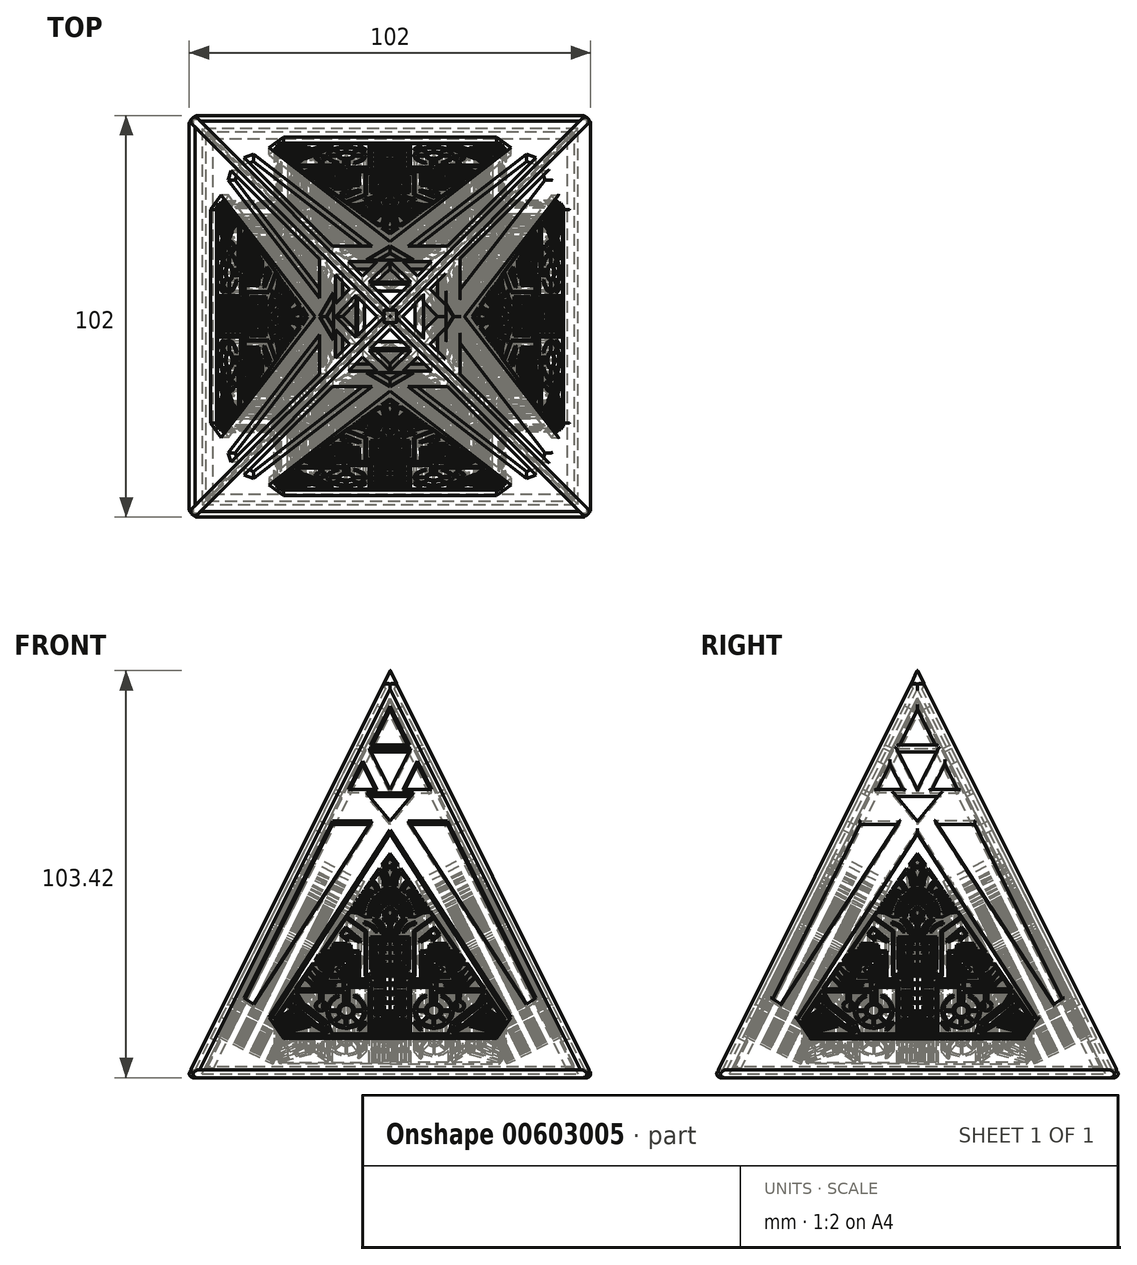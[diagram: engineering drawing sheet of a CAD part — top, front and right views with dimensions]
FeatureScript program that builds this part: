
annotation { "Feature Type Name" : "Feature", "Feature Type Description" : "" }
export const myFeature = defineFeature(function(context is Context, id is Id, definition is map)
    precondition{}
    {
        {
            var Q0;
            Q0=qCreatedBy(makeId("Front.planeOp"),FACE);
            var sketch = newSketch(context, id + "F0", { "sketchPlane" : qUnion([Q0])});
            skLineSegment(sketch, "E0", {"start": v(-50, 0) * mm, "end": v(50, 0) * mm});
            skLineSegment(sketch, "E1", {"start": v(50, 0) * mm, "end": v(0, 100) * mm});
            skLineSegment(sketch, "E2", {"start": v(0, 100) * mm, "end": v(-50, 0) * mm});
            skLineSegment(sketch, "E3", {"start": v(0, 0) * mm, "end": v(0, 112.42) * mm, "construction": true});
            skSolve(sketch);
        }
        {
            var Q0;
            Q0=qCreatedBy(makeId("Right.planeOp"),FACE);
            cPlane(context, id + "F1", {"entities" : qUnion([Q0]), "cplaneType" : CPlaneType.OFFSET, "offset" : 50 * mm, "width" : 150 * mm, "height" : 150 * mm});
        }
        {
            var Q0;
            Q0=qCreatedBy(id+"F1.planeOp",FACE);
            var Q1;
            Q1=sQuery(id+"F0.wireOp",EDGE,"E1");
            cPlane(context, id + "F2", {"entities" : qUnion([Q0, Q1]), "cplaneType" : CPlaneType.LINE_ANGLE, "offset" : 25 * mm, "angle" : 0 * degree, "width" : 150 * mm, "height" : 150 * mm});
        }
        {
            var Q0;
            Q0=qCreatedBy(id+"F2.planeOp",FACE);
            var sketch = newSketch(context, id + "F3", { "sketchPlane" : qUnion([Q0])});
            skPoint(sketch, "E4.0", {"position": v(0, -22.36) * mm});
            skPoint(sketch, "E5.0", {"position": v(0, 89.44) * mm});
            skLineSegment(sketch, "E6", {"start": v(50, -22.36) * mm, "end": v(-50, -22.36) * mm});
            skLineSegment(sketch, "E7", {"start": v(-50, -22.36) * mm, "end": v(0, 89.44) * mm});
            skLineSegment(sketch, "E8", {"start": v(50, -22.36) * mm, "end": v(0, 89.44) * mm});
            skLineSegment(sketch, "E9", {"start": v(35.98, 49.44) * mm, "end": v(-47.97, 49.44) * mm, "construction": true});
            skLineSegment(sketch, "E10", {"start": v(46.71, -22.36) * mm, "end": v(-5.35, 94.05) * mm, "construction": true});
            skLineSegment(sketch, "E11", {"start": v(89.5, -12.36) * mm, "end": v(-110.17, -12.36) * mm, "construction": true});
            skLineSegment(sketch, "E12", {"start": v(0, 89.44) * mm, "end": v(0, 132.78) * mm, "construction": true});
            skLineSegment(sketch, "E13", {"start": v(-1.46, 49.44) * mm, "end": v(40, -22.36) * mm, "construction": true});
            skCircle(sketch, "E14", {"center": v(50, -22.36) * mm, "radius": 25 * mm, "construction": true});
            skLineSegment(sketch, "E15.MirrorCS", {"start": v(-46.71, -22.36) * mm, "end": v(5.35, 94.05) * mm, "construction": true});
            skLineSegment(sketch, "E16.MirrorCS", {"start": v(1.46, 49.44) * mm, "end": v(-40, -22.36) * mm, "construction": true});
            skLineSegment(sketch, "E17", {"start": v(-14.6, 49.44) * mm, "end": v(-4.6, 49.44) * mm});
            skCircle(sketch, "E18.MirrorC", {"center": v(-50, -22.36) * mm, "radius": 25 * mm, "construction": true});
            skLineSegment(sketch, "E19", {"start": v(-4.6, 49.44) * mm, "end": v(-34.66, -2.62) * mm});
            skLineSegment(sketch, "E20", {"start": v(-34.66, -2.62) * mm, "end": v(-37.05, -0.76) * mm});
            skLineSegment(sketch, "E21", {"start": v(-37.05, -0.76) * mm, "end": v(-14.6, 49.44) * mm});
            skLineSegment(sketch, "E22.MirrorCS", {"start": v(4.6, 49.44) * mm, "end": v(34.66, -2.62) * mm});
            skLineSegment(sketch, "E23.MirrorCS", {"start": v(37.05, -0.76) * mm, "end": v(14.6, 49.44) * mm});
            skLineSegment(sketch, "E24.MirrorCS", {"start": v(34.66, -2.62) * mm, "end": v(37.05, -0.76) * mm});
            skLineSegment(sketch, "E25.MirrorCS", {"start": v(14.6, 49.44) * mm, "end": v(4.6, 49.44) * mm});
            skLineSegment(sketch, "E26", {"start": v(0, 46.92) * mm, "end": v(30.77, -6.38) * mm});
            skLineSegment(sketch, "E27", {"start": v(-27.09, -12.36) * mm, "end": v(-30.77, -6.38) * mm});
            skLineSegment(sketch, "E28", {"start": v(-30.77, -6.38) * mm, "end": v(0, 46.92) * mm});
            skLineSegment(sketch, "E29", {"start": v(30.77, -6.38) * mm, "end": v(27.09, -12.36) * mm});
            skLineSegment(sketch, "E30", {"start": v(27.09, -12.36) * mm, "end": v(-27.09, -12.36) * mm});
            skLineSegment(sketch, "E31", {"start": v(23.46, 57.44) * mm, "end": v(-27.6, 57.44) * mm, "construction": true});
            skLineSegment(sketch, "E32", {"start": v(6, 57.44) * mm, "end": v(0, 49.44) * mm});
            skLineSegment(sketch, "E33", {"start": v(0, 49.44) * mm, "end": v(-6, 57.44) * mm});
            skLineSegment(sketch, "E34", {"start": v(-6, 57.44) * mm, "end": v(6, 57.44) * mm});
            skLineSegment(sketch, "E35", {"start": v(12.53, 58.44) * mm, "end": v(-20.65, 58.44) * mm, "construction": true});
            skLineSegment(sketch, "E36", {"start": v(0, 82.1) * mm, "end": v(4.92, 71.1) * mm});
            skLineSegment(sketch, "E37", {"start": v(4.92, 71.1) * mm, "end": v(-4.92, 71.1) * mm});
            skLineSegment(sketch, "E38", {"start": v(-4.92, 71.1) * mm, "end": v(0, 82.1) * mm});
            skLineSegment(sketch, "E39", {"start": v(14.36, 70.1) * mm, "end": v(-15.5, 70.1) * mm, "construction": true});
            skLineSegment(sketch, "E40", {"start": v(5.37, 70.1) * mm, "end": v(0, 58.44) * mm});
            skLineSegment(sketch, "E41", {"start": v(0, 58.44) * mm, "end": v(-5.37, 70.1) * mm});
            skLineSegment(sketch, "E42", {"start": v(-5.37, 70.1) * mm, "end": v(5.37, 70.1) * mm});
            skLineSegment(sketch, "E43", {"start": v(10.58, 58.44) * mm, "end": v(7, 66.46) * mm});
            skLineSegment(sketch, "E44", {"start": v(7, 66.46) * mm, "end": v(3.3, 58.44) * mm});
            skLineSegment(sketch, "E45", {"start": v(3.3, 58.44) * mm, "end": v(10.58, 58.44) * mm});
            skLineSegment(sketch, "E46.MirrorCS", {"start": v(-7, 66.46) * mm, "end": v(-3.3, 58.44) * mm});
            skLineSegment(sketch, "E47.MirrorCS", {"start": v(-3.3, 58.44) * mm, "end": v(-10.58, 58.44) * mm});
            skLineSegment(sketch, "E48.MirrorCS", {"start": v(-10.58, 58.44) * mm, "end": v(-7, 66.46) * mm});
            skSolve(sketch);
        }
        {
            var Q0;
            Q0=makeQuery(id+"F3.imprint","IMPRINT",FACE,{"disambiguationData":[TD([[makeQuery(id+"F3.imprint","IMPRINT",EDGE,{"derivedFrom":sQuery(id+"F3.wireOp",EDGE,"E6")}),-1.0]])]});
            extrude(context, id + "F4", {"entities" : qUnion([Q0]), "depth" : 2 * mm, "offsetDistance" : 25 * mm});
        }
        {
            var Q0;
            Q0=makeQuery(id+"F4.opExtrude","SWEPT_BODY",BODY,{"disambiguationData":[OSD([sQuery(id+"F3.wireOp",EDGE,"E6"),sQuery(id+"F3.wireOp",EDGE,"E7"),sQuery(id+"F3.wireOp",EDGE,"E8")])]});
            var Q1;
            Q1=sQuery(id+"F0.wireOp",EDGE,"E3");
            circularPattern(context, id + "F5", {"entities" : qUnion([Q0]), "axis" : qUnion([Q1]), "angle" : 360 * degree, "instanceCount" : 4, "equalSpace" : true});
        }
        {
            var Q0;
            Q0=qCreatedBy(makeId("Right.planeOp"),FACE);
            var sketch = newSketch(context, id + "F6", { "sketchPlane" : qUnion([Q0])});
            skPoint(sketch, "E49.0", {"position": v(0, 100) * mm});
            skLineSegment(sketch, "E50.0", {"start": v(50, 0) * mm, "end": v(0, 100) * mm, "construction": true});
            skLineSegment(sketch, "E51", {"start": v(0, 100) * mm, "end": v(3.76, 100) * mm});
            skLineSegment(sketch, "E52", {"start": v(3.76, 100) * mm, "end": v(2.28, 95.44) * mm});
            skLineSegment(sketch, "E53", {"start": v(2.28, 95.44) * mm, "end": v(0, 100) * mm});
            skLineSegment(sketch, "E54", {"start": v(0, 100) * mm, "end": v(0, 104.73) * mm, "construction": true});
            skLineSegment(sketch, "E55.MirrorCS", {"start": v(0, 100) * mm, "end": v(-3.76, 100) * mm});
            skLineSegment(sketch, "E56.MirrorCS", {"start": v(-3.76, 100) * mm, "end": v(-2.28, 95.44) * mm});
            skLineSegment(sketch, "E57.MirrorCS", {"start": v(-2.28, 95.44) * mm, "end": v(0, 100) * mm});
            skSolve(sketch);
        }
        {
            var Q0;
            Q0 = qSketchRegion(id + "F6", true);
            extrude(context, id + "F7", {"entities" : qUnion([Q0]), "operationType" : NewBodyOperationType.REMOVE, "endBound" : BoundingType.SYMMETRIC, "oppositeDirection" : true, "depth" : 25 * mm, "offsetDistance" : 25 * mm});
        }
        {
            var Q0;
            Q0=qCreatedBy(makeId("Front.planeOp"),FACE);
            var sketch = newSketch(context, id + "F8", { "sketchPlane" : qUnion([Q0])});
            skPoint(sketch, "E58.0", {"position": v(0, 100) * mm});
            skLineSegment(sketch, "E59.0", {"start": v(50, 0) * mm, "end": v(0, 100) * mm, "construction": true});
            skLineSegment(sketch, "E60", {"start": v(0, 100) * mm, "end": v(1.68, 96.63) * mm});
            skLineSegment(sketch, "E61", {"start": v(1.68, 96.63) * mm, "end": v(3.16, 99.58) * mm});
            skLineSegment(sketch, "E62", {"start": v(3.16, 99.58) * mm, "end": v(0, 100) * mm});
            skLineSegment(sketch, "E63", {"start": v(0, 100) * mm, "end": v(0, 101.09) * mm, "construction": true});
            skLineSegment(sketch, "E64.MirrorCS", {"start": v(-3.16, 99.58) * mm, "end": v(0, 100) * mm});
            skLineSegment(sketch, "E65.MirrorCS", {"start": v(0, 100) * mm, "end": v(-1.68, 96.63) * mm});
            skLineSegment(sketch, "E66.MirrorCS", {"start": v(-1.68, 96.63) * mm, "end": v(-3.16, 99.58) * mm});
            skSolve(sketch);
        }
        {
            var Q0;
            Q0=makeQuery(id+"F8.imprint","IMPRINT",FACE,{"disambiguationData":[TD([[makeQuery(id+"F8.imprint","IMPRINT",EDGE,{"derivedFrom":sQuery(id+"F8.wireOp",EDGE,"E60")}),1.0]])]});
            var Q1;
            Q1=makeQuery(id+"F8.imprint","IMPRINT",FACE,{"disambiguationData":[TD([[makeQuery(id+"F8.imprint","IMPRINT",EDGE,{"derivedFrom":sQuery(id+"F8.wireOp",EDGE,"E64.MirrorCS")}),-1.0]])]});
            extrude(context, id + "F9", {"entities" : qUnion([Q0, Q1]), "operationType" : NewBodyOperationType.REMOVE, "endBound" : BoundingType.SYMMETRIC, "oppositeDirection" : true, "depth" : 25 * mm, "offsetDistance" : 25 * mm});
        }
        {
            var Q0;
            Q0=qCreatedBy(makeId("Top.planeOp"),FACE);
            var sketch = newSketch(context, id + "F10", { "sketchPlane" : qUnion([Q0])});
            skLineSegment(sketch, "E67.0", {"start": v(50, 50) * mm, "end": v(-50, 50) * mm});
            skLineSegment(sketch, "E68.0", {"start": v(50, -50) * mm, "end": v(50, 50) * mm});
            skLineSegment(sketch, "E69.0", {"start": v(-50, -50) * mm, "end": v(50, -50) * mm});
            skLineSegment(sketch, "E70.0", {"start": v(-50, 50) * mm, "end": v(-50, -50) * mm});
            skSolve(sketch);
        }
        {
            var Q0;
            Q0 = qSketchRegion(id + "F10", true);
            extrude(context, id + "F11", {"entities" : qUnion([Q0]), "operationType" : NewBodyOperationType.ADD, "oppositeDirection" : true, "depth" : 1 * mm, "offsetDistance" : 25 * mm});
        }
        {
            var Q0;
            Q0=qCreatedBy(id+"F2.planeOp",FACE);
            cPlane(context, id + "F12", {"entities" : qUnion([Q0]), "cplaneType" : CPlaneType.OFFSET, "offset" : 2 * mm, "width" : 150 * mm, "height" : 150 * mm});
        }
        {
            var Q0;
            Q0=qCreatedBy(id+"F12.planeOp",FACE);
            var sketch = newSketch(context, id + "F13", { "sketchPlane" : qUnion([Q0])});
            skLineSegment(sketch, "E71.0", {"start": v(50, -22.36) * mm, "end": v(0, 89.44) * mm, "construction": true});
            skLineSegment(sketch, "E72.0", {"start": v(-50, -22.36) * mm, "end": v(0, 89.44) * mm, "construction": true});
            skLineSegment(sketch, "E73.0", {"start": v(50, -22.36) * mm, "end": v(-50, -22.36) * mm, "construction": true});
            skLineSegment(sketch, "E74", {"start": v(46.47, -19.36) * mm, "end": v(-46.47, -19.36) * mm});
            skLineSegment(sketch, "E75", {"start": v(-46.47, -19.36) * mm, "end": v(0, 84.54) * mm});
            skLineSegment(sketch, "E76", {"start": v(0, 84.54) * mm, "end": v(46.47, -19.36) * mm});
            skSolve(sketch);
        }
        {
            var Q0;
            Q0 = qSketchRegion(id + "F13", true);
            extrude(context, id + "F14", {"entities" : qUnion([Q0]), "depth" : 2 * mm, "offsetDistance" : 25 * mm});
        }
        {
            var Q0;
            Q0=makeQuery(id+"F14.opExtrude","SWEPT_BODY",BODY,{"disambiguationData":[OSD([sQuery(id+"F13.wireOp",EDGE,"E74"),sQuery(id+"F13.wireOp",EDGE,"E75"),sQuery(id+"F13.wireOp",EDGE,"E76")])]});
            var Q1;
            Q1=sQuery(id+"F0.wireOp",EDGE,"E3");
            circularPattern(context, id + "F15", {"operationType" : NewBodyOperationType.ADD, "entities" : qUnion([Q0]), "axis" : qUnion([Q1]), "angle" : 360 * degree, "instanceCount" : 4, "equalSpace" : true});
        }
        {
            var Q0;
            Q0=qCreatedBy(id+"F2.planeOp",FACE);
            var sketch = newSketch(context, id + "F16", { "sketchPlane" : qUnion([Q0])});
            skLineSegment(sketch, "E77.0", {"start": v(-50, -22.36) * mm, "end": v(0, 89.44) * mm, "construction": true});
            skLineSegment(sketch, "E78", {"start": v(0.5, 88.12) * mm, "end": v(-48.68, -21.86) * mm});
            skArc(sketch, "E79", {"start": v(-50, -22.36) * mm, "mid": v(-49.23, -22.38) * mm, "end": v(-48.68, -21.86) * mm});
            skArc(sketch, "E80", {"start": v(0.5, 88.12) * mm, "mid": v(0.53, 88.89) * mm, "end": v(0, 89.44) * mm});
            skLineSegment(sketch, "E81", {"start": v(0, 89.44) * mm, "end": v(-50, -22.36) * mm});
            skSolve(sketch);
        }
        {
            var Q0;
            Q0 = qSketchRegion(id + "F16", true);
            var Q1;
            Q1=sQuery(id+"F16.wireOp",EDGE,"E81");
            revolve(context, id + "F17", {"entities" : qUnion([Q0]), "axis" : qUnion([Q1]), "revolveType" : RevolveType.FULL});
        }
        {
            var Q0;
            Q0=makeQuery(id+"F17.opRevolve","SWEPT_BODY",BODY,{"disambiguationData":[OSD([sQuery(id+"F16.wireOp",EDGE,"E78"),sQuery(id+"F16.wireOp",EDGE,"E79"),sQuery(id+"F16.wireOp",EDGE,"E80"),sQuery(id+"F16.wireOp",EDGE,"E81")])]});
            var Q1;
            Q1=sQuery(id+"F0.wireOp",EDGE,"E3");
            circularPattern(context, id + "F18", {"operationType" : NewBodyOperationType.ADD, "entities" : qUnion([Q0]), "axis" : qUnion([Q1]), "angle" : 360 * degree, "instanceCount" : 4, "equalSpace" : true});
        }
        {
            var Q0;
            Q0=qCreatedBy(id+"F2.planeOp",FACE);
            var sketch = newSketch(context, id + "F19", { "sketchPlane" : qUnion([Q0])});
            skLineSegment(sketch, "E82.0", {"start": v(50, -22.36) * mm, "end": v(-50, -22.36) * mm, "construction": true});
            skLineSegment(sketch, "E83", {"start": v(49, -21.36) * mm, "end": v(-49, -21.36) * mm});
            skArc(sketch, "E84", {"start": v(-49, -21.36) * mm, "mid": v(-49.7, -21.65) * mm, "end": v(-50, -22.36) * mm});
            skArc(sketch, "E85", {"start": v(50, -22.36) * mm, "mid": v(49.7, -21.65) * mm, "end": v(49, -21.36) * mm});
            skLineSegment(sketch, "E86", {"start": v(-50, -22.36) * mm, "end": v(50, -22.36) * mm});
            skSolve(sketch);
        }
        {
            var Q0;
            Q0 = qSketchRegion(id + "F19", true);
            var Q1;
            Q1=sQuery(id+"F19.wireOp",EDGE,"E86");
            revolve(context, id + "F20", {"entities" : qUnion([Q0]), "axis" : qUnion([Q1]), "revolveType" : RevolveType.FULL});
        }
        {
            var Q0;
            Q0=makeQuery(id+"F20.opRevolve","SWEPT_BODY",BODY,{"disambiguationData":[OSD([sQuery(id+"F19.wireOp",EDGE,"E83"),sQuery(id+"F19.wireOp",EDGE,"E84"),sQuery(id+"F19.wireOp",EDGE,"E85"),sQuery(id+"F19.wireOp",EDGE,"E86")])]});
            var Q1;
            Q1=sQuery(id+"F0.wireOp",EDGE,"E3");
            circularPattern(context, id + "F21", {"operationType" : NewBodyOperationType.ADD, "entities" : qUnion([Q0]), "axis" : qUnion([Q1]), "angle" : 360 * degree, "instanceCount" : 4, "equalSpace" : true});
        }
        {
            var Q0;
            Q0=qCreatedBy(makeId("Top.planeOp"),FACE);
            cPlane(context, id + "F22", {"entities" : qUnion([Q0]), "cplaneType" : CPlaneType.OFFSET, "offset" : 99 * mm, "width" : 150 * mm, "height" : 150 * mm});
        }
        {
            var Q0;
            Q0=qCreatedBy(id+"F22.planeOp",FACE);
            var sketch = newSketch(context, id + "F23", { "sketchPlane" : qUnion([Q0])});
            skLineSegment(sketch, "E87.bottom", {"start": v(-1.6, 1.66) * mm, "end": v(1.72, 1.66) * mm});
            skLineSegment(sketch, "E87.top", {"start": v(-1.6, -1.66) * mm, "end": v(1.72, -1.66) * mm});
            skLineSegment(sketch, "E87.left", {"start": v(-1.6, 1.66) * mm, "end": v(-1.6, -1.66) * mm});
            skLineSegment(sketch, "E87.right", {"start": v(1.72, 1.66) * mm, "end": v(1.72, -1.66) * mm});
            skSolve(sketch);
        }
        {
            var Q0;
            Q0=makeQuery(id+"F23.imprint","IMPRINT",FACE,{"disambiguationData":[TD([[makeQuery(id+"F23.imprint","IMPRINT",EDGE,{"derivedFrom":sQuery(id+"F23.wireOp",EDGE,"E87.bottom")}),-1.0]])]});
            extrude(context, id + "F24", {"entities" : qUnion([Q0]), "operationType" : NewBodyOperationType.ADD, "depth" : 25 * mm, "offsetDistance" : 25 * mm, "hasDraft" : true, "draftAngle" : 25 * degree, "draftPullDirection" : true});
        }
        {
            var Q0;
            Q0=makeQuery(id+"F24.opExtrude","SWEPT_EDGE",EDGE,{"disambiguationData":[OSD([sQuery(id+"F23.wireOp",EDGE,"E87.top"),sQuery(id+"F23.wireOp",EDGE,"E87.left")])]});
            var Q1;
            Q1=makeQuery(id+"F24.opExtrude","CAP_EDGE",EDGE,{"disambiguationData":[OSD([sQuery(id+"F23.wireOp",EDGE,"E87.top")])],"isStart":true});
            var Q2;
            Q2=makeQuery(id+"F24.opExtrude","SWEPT_EDGE",EDGE,{"disambiguationData":[OSD([sQuery(id+"F23.wireOp",EDGE,"E87.top"),sQuery(id+"F23.wireOp",EDGE,"E87.right")])]});
            var Q3;
            Q3=makeQuery(id+"F24.opExtrude","SWEPT_EDGE",EDGE,{"disambiguationData":[OSD([sQuery(id+"F23.wireOp",EDGE,"E87.bottom"),sQuery(id+"F23.wireOp",EDGE,"E87.right")])]});
            var Q4;
            Q4=makeQuery(id+"F24.opExtrude","CAP_EDGE",EDGE,{"disambiguationData":[OSD([sQuery(id+"F23.wireOp",EDGE,"E87.right")])],"isStart":true});
            var Q5;
            {var subQ0=sQuery(id+"F23.wireOp",EDGE,"E87.top");var subQ1=sQuery(id+"F23.wireOp",EDGE,"E87.left");Q5=makeQuery(id+"F24.boolean.opBoolean","SPLIT",EDGE,{"disambiguationData":[TD([makeQuery(id+"F18.opPattern","COPY",FACE,{"derivedFrom":makeQuery(id+"F17.opRevolve","SWEPT_FACE",FACE,{"disambiguationData":[OSD([sQuery(id+"F16.wireOp",EDGE,"E78")])]}),"instanceName":"2"}),makeQuery(id+"F24.opExtrude","CAP_FACE",FACE,{"disambiguationData":[OSD([sQuery(id+"F23.wireOp",EDGE,"E87.bottom"),subQ0,subQ1,sQuery(id+"F23.wireOp",EDGE,"E87.right")])],"isStart":true}),makeQuery(id+"F24.opExtrude","SWEPT_FACE",FACE,{"disambiguationData":[OSD([subQ0])]}),makeQuery(id+"F24.opExtrude","SWEPT_FACE",FACE,{"disambiguationData":[OSD([subQ1])]})])],"derivedFrom":makeQuery(id+"F24.opExtrude","CAP_EDGE",EDGE,{"disambiguationData":[OSD([subQ1])],"isStart":true})});}
            var Q6;
            {var subQ0=makeQuery(id+"F17.opRevolve","SWEPT_FACE",FACE,{"disambiguationData":[OSD([sQuery(id+"F16.wireOp",EDGE,"E78")])]});var subQ1=sQuery(id+"F23.wireOp",EDGE,"E87.left");Q6=makeQuery(id+"F24.boolean.opBoolean","SPLIT",EDGE,{"disambiguationData":[TD([makeQuery(id+"F18.opPattern","COPY",FACE,{"derivedFrom":subQ0,"instanceName":"1"}),makeQuery(id+"F18.opPattern","COPY",FACE,{"derivedFrom":subQ0,"instanceName":"2"}),makeQuery(id+"F24.opExtrude","CAP_FACE",FACE,{"disambiguationData":[OSD([sQuery(id+"F23.wireOp",EDGE,"E87.bottom"),sQuery(id+"F23.wireOp",EDGE,"E87.top"),subQ1,sQuery(id+"F23.wireOp",EDGE,"E87.right")])],"isStart":true}),makeQuery(id+"F24.opExtrude","SWEPT_FACE",FACE,{"disambiguationData":[OSD([subQ1])]})])],"derivedFrom":makeQuery(id+"F24.opExtrude","CAP_EDGE",EDGE,{"disambiguationData":[OSD([subQ1])],"isStart":true})});}
            var Q7;
            {var subQ0=sQuery(id+"F23.wireOp",EDGE,"E87.bottom");var subQ1=sQuery(id+"F23.wireOp",EDGE,"E87.left");Q7=makeQuery(id+"F24.boolean.opBoolean","SPLIT",EDGE,{"disambiguationData":[TD([makeQuery(id+"F18.opPattern","COPY",FACE,{"derivedFrom":makeQuery(id+"F17.opRevolve","SWEPT_FACE",FACE,{"disambiguationData":[OSD([sQuery(id+"F16.wireOp",EDGE,"E78")])]}),"instanceName":"1"}),makeQuery(id+"F24.opExtrude","SWEPT_FACE",FACE,{"disambiguationData":[OSD([subQ0])]}),makeQuery(id+"F24.opExtrude","CAP_FACE",FACE,{"disambiguationData":[OSD([subQ0,sQuery(id+"F23.wireOp",EDGE,"E87.top"),subQ1,sQuery(id+"F23.wireOp",EDGE,"E87.right")])],"isStart":true}),makeQuery(id+"F24.opExtrude","SWEPT_FACE",FACE,{"disambiguationData":[OSD([subQ1])]})])],"derivedFrom":makeQuery(id+"F24.opExtrude","CAP_EDGE",EDGE,{"disambiguationData":[OSD([subQ1])],"isStart":true})});}
            var Q8;
            Q8=makeQuery(id+"F24.opExtrude","SWEPT_EDGE",EDGE,{"disambiguationData":[OSD([sQuery(id+"F23.wireOp",EDGE,"E87.bottom"),sQuery(id+"F23.wireOp",EDGE,"E87.left")])]});
            var Q9;
            Q9=makeQuery(id+"F24.opExtrude","CAP_EDGE",EDGE,{"disambiguationData":[OSD([sQuery(id+"F23.wireOp",EDGE,"E87.bottom")])],"isStart":true});
            fillet(context, id + "F25", {"entities" : qUnion([Q0, Q1, Q2, Q3, Q4, Q5, Q6, Q7, Q8, Q9]), "radius" : .1 * mm, "tangentPropagation" : true, "allowEdgeOverflow" : false});
        }
        {
            var Q0;
            Q0=makeQuery(id+"F14.opExtrude","CAP_FACE",FACE,{"disambiguationData":[OSD([sQuery(id+"F13.wireOp",EDGE,"E74"),sQuery(id+"F13.wireOp",EDGE,"E75"),sQuery(id+"F13.wireOp",EDGE,"E76")])],"isStart":true});
            var sketch = newSketch(context, id + "F26", { "sketchPlane" : qUnion([Q0])});
            skLineSegment(sketch, "E88", {"start": v(0, 47.8) * mm, "end": v(0, -17.25) * mm, "construction": true});
            skLineSegment(sketch, "E89.0", {"start": v(30.77, -6.38) * mm, "end": v(0, 46.92) * mm, "construction": true});
            skLineSegment(sketch, "E90.0", {"start": v(27.09, -12.36) * mm, "end": v(30.77, -6.38) * mm, "construction": true});
            skLineSegment(sketch, "E91.0", {"start": v(-27.09, -12.36) * mm, "end": v(27.09, -12.36) * mm, "construction": true});
            skCircle(sketch, "E92", {"center": v(11.12, -3.94) * mm, "radius": 1.62 * mm});
            skArc(sketch, "E93", {"start": v(8.97, -4.1) * mm, "mid": v(9.14, -4.8) * mm, "end": v(9.54, -5.4) * mm});
            skArc(sketch, "E94", {"start": v(8.98, 0.55) * mm, "mid": v(11.12, -8.92) * mm, "end": v(13.26, 0.55) * mm});
            skArc(sketch, "E95", {"start": v(9.32, 0.06) * mm, "mid": v(7.5, -1.47) * mm, "end": v(6.74, -3.71) * mm});
            skLineSegment(sketch, "E96", {"start": v(8.98, 0.55) * mm, "end": v(9.32, 0.06) * mm});
            skLineSegment(sketch, "E97", {"start": v(12.93, 0.06) * mm, "end": v(13.26, 0.55) * mm});
            skLineSegment(sketch, "E98", {"start": v(6.74, -3.71) * mm, "end": v(8.98, -3.71) * mm});
            skLineSegment(sketch, "E99", {"start": v(6.73, -4.1) * mm, "end": v(8.97, -4.1) * mm});
            skLineSegment(sketch, "E100", {"start": v(13.26, -3.66) * mm, "end": v(15.5, -3.66) * mm});
            skLineSegment(sketch, "E101", {"start": v(13.27, -4.1) * mm, "end": v(15.5, -4.1) * mm});
            skLineSegment(sketch, "E102", {"start": v(9.54, -5.4) * mm, "end": v(8.04, -7.07) * mm});
            skLineSegment(sketch, "E103", {"start": v(9.82, -5.67) * mm, "end": v(8.33, -7.33) * mm});
            skLineSegment(sketch, "E104", {"start": v(10.94, -6.1) * mm, "end": v(10.94, -8.33) * mm});
            skLineSegment(sketch, "E105", {"start": v(11.36, -6.09) * mm, "end": v(11.36, -8.33) * mm});
            skLineSegment(sketch, "E106", {"start": v(12.43, -5.65) * mm, "end": v(13.98, -7.28) * mm});
            skLineSegment(sketch, "E107", {"start": v(12.77, -5.33) * mm, "end": v(14.35, -6.92) * mm});
            skArc(sketch, "E108.trimOffspring", {"start": v(6.73, -4.1) * mm, "mid": v(7.1, -5.71) * mm, "end": v(8.04, -7.07) * mm});
            skArc(sketch, "E109.trimOffspring", {"start": v(9.82, -5.67) * mm, "mid": v(10.35, -5.96) * mm, "end": v(10.94, -6.1) * mm});
            skArc(sketch, "E110.trimOffspring", {"start": v(8.33, -7.33) * mm, "mid": v(9.55, -8.04) * mm, "end": v(10.94, -8.33) * mm});
            skArc(sketch, "E111.trimOffspring", {"start": v(11.36, -8.33) * mm, "mid": v(12.76, -8.02) * mm, "end": v(13.98, -7.28) * mm});
            skArc(sketch, "E112.trimOffspring", {"start": v(11.36, -6.09) * mm, "mid": v(11.93, -5.94) * mm, "end": v(12.43, -5.65) * mm});
            skArc(sketch, "E113.trimOffspring", {"start": v(12.77, -5.33) * mm, "mid": v(13.12, -4.76) * mm, "end": v(13.27, -4.1) * mm});
            skArc(sketch, "E114.trimOffspring", {"start": v(14.35, -6.92) * mm, "mid": v(15.18, -5.61) * mm, "end": v(15.5, -4.1) * mm});
            skArc(sketch, "E115.trimOffspring", {"start": v(15.5, -3.66) * mm, "mid": v(14.73, -1.44) * mm, "end": v(12.93, 0.06) * mm});
            skArc(sketch, "E116.trimOffspring", {"start": v(13.26, -3.66) * mm, "mid": v(12.8, -2.58) * mm, "end": v(11.84, -1.91) * mm});
            skLineSegment(sketch, "E117", {"start": v(0, -11.13) * mm, "end": v(27.85, -11.13) * mm});
            skLineSegment(sketch, "E118", {"start": v(27.85, -11.13) * mm, "end": v(28.3, -10.39) * mm});
            skLineSegment(sketch, "E119", {"start": v(28.3, -10.39) * mm, "end": v(21.26, -8.04) * mm});
            skLineSegment(sketch, "E120", {"start": v(21.26, -8.04) * mm, "end": v(21.39, -7.66) * mm});
            skLineSegment(sketch, "E121", {"start": v(21.39, -7.66) * mm, "end": v(28.52, -10.04) * mm});
            skLineSegment(sketch, "E122", {"start": v(28.52, -10.04) * mm, "end": v(28.75, -9.66) * mm});
            skLineSegment(sketch, "E123", {"start": v(28.75, -9.66) * mm, "end": v(22.67, -6.78) * mm});
            skLineSegment(sketch, "E124", {"start": v(22.67, -6.78) * mm, "end": v(22.76, -6.58) * mm});
            skLineSegment(sketch, "E125", {"start": v(22.76, -6.58) * mm, "end": v(28.7, -9.16) * mm});
            skLineSegment(sketch, "E126", {"start": v(28.7, -9.16) * mm, "end": v(28.97, -8.55) * mm});
            skLineSegment(sketch, "E127", {"start": v(28.97, -8.55) * mm, "end": v(23.78, -5.73) * mm});
            skLineSegment(sketch, "E128", {"start": v(23.78, -5.73) * mm, "end": v(23.91, -5.5) * mm});
            skLineSegment(sketch, "E129", {"start": v(23.91, -5.5) * mm, "end": v(28.87, -8.2) * mm});
            skLineSegment(sketch, "E130", {"start": v(28.87, -8.2) * mm, "end": v(29.44, -7.27) * mm});
            skLineSegment(sketch, "E131", {"start": v(29.44, -7.27) * mm, "end": v(25.07, -4.57) * mm});
            skLineSegment(sketch, "E132", {"start": v(25.07, -4.57) * mm, "end": v(25.07, -4.38) * mm});
            skLineSegment(sketch, "E133", {"start": v(25.07, -4.38) * mm, "end": v(29.18, -6.91) * mm});
            skLineSegment(sketch, "E134", {"start": v(29.18, -6.91) * mm, "end": v(29.4, -6.56) * mm});
            skLineSegment(sketch, "E135", {"start": v(29.4, -6.56) * mm, "end": v(24.27, 1.83) * mm});
            skLineSegment(sketch, "E136", {"start": v(24.27, 1.83) * mm, "end": v(11.53, 1.55) * mm});
            skLineSegment(sketch, "E137", {"start": v(11.53, 1.55) * mm, "end": v(11.53, -1.57) * mm});
            skLineSegment(sketch, "E138", {"start": v(11.53, -1.57) * mm, "end": v(11.53, -1.82) * mm});
            skLineSegment(sketch, "E139", {"start": v(11.84, -1.91) * mm, "end": v(11.84, 1.14) * mm});
            skLineSegment(sketch, "E140", {"start": v(11.84, 1.14) * mm, "end": v(23.89, 1.43) * mm});
            skLineSegment(sketch, "E141", {"start": v(24.42, 0.56) * mm, "end": v(24.67, 0.15) * mm});
            skLineSegment(sketch, "E142", {"start": v(28.5, -6.11) * mm, "end": v(25.16, -3.84) * mm});
            skLineSegment(sketch, "E143", {"start": v(25.16, -3.84) * mm, "end": v(24.47, -4.53) * mm});
            skLineSegment(sketch, "E144", {"start": v(24.47, -4.53) * mm, "end": v(28.98, -7.38) * mm});
            skLineSegment(sketch, "E145", {"start": v(28.98, -7.38) * mm, "end": v(28.87, -7.66) * mm});
            skLineSegment(sketch, "E146", {"start": v(28.87, -7.66) * mm, "end": v(23.87, -5.03) * mm});
            skLineSegment(sketch, "E147", {"start": v(23.87, -5.03) * mm, "end": v(23.16, -5.74) * mm});
            skLineSegment(sketch, "E148", {"start": v(23.16, -5.74) * mm, "end": v(28.09, -8.49) * mm});
            skLineSegment(sketch, "E149", {"start": v(28.09, -8.49) * mm, "end": v(22.7, -6.12) * mm});
            skLineSegment(sketch, "E150", {"start": v(22.7, -6.12) * mm, "end": v(22.05, -6.75) * mm});
            skLineSegment(sketch, "E151", {"start": v(22.05, -6.75) * mm, "end": v(26, -8.82) * mm});
            skLineSegment(sketch, "E152", {"start": v(26, -8.82) * mm, "end": v(21.54, -7.27) * mm});
            skLineSegment(sketch, "E153", {"start": v(21.54, -7.27) * mm, "end": v(20.2, -8.36) * mm});
            skLineSegment(sketch, "E154", {"start": v(20.2, -8.36) * mm, "end": v(27.53, -10.57) * mm});
            skLineSegment(sketch, "E155", {"start": v(27.53, -10.57) * mm, "end": v(15.81, -10.57) * mm});
            skLineSegment(sketch, "E156", {"start": v(0, -10.57) * mm, "end": v(0, -11.13) * mm});
            skArc(sketch, "E157.trimOffspring", {"start": v(11.53, -1.82) * mm, "mid": v(9.84, -2.2) * mm, "end": v(8.98, -3.71) * mm});
            skLineSegment(sketch, "E158", {"start": v(23.89, 1.43) * mm, "end": v(21.88, -2.28) * mm});
            skLineSegment(sketch, "E159", {"start": v(21.88, -2.28) * mm, "end": v(21.39, -2.28) * mm});
            skLineSegment(sketch, "E160", {"start": v(21.39, -2.28) * mm, "end": v(15.2, -7.77) * mm});
            skLineSegment(sketch, "E161", {"start": v(15.2, -7.77) * mm, "end": v(15.49, -8.09) * mm});
            skLineSegment(sketch, "E162", {"start": v(15.49, -8.09) * mm, "end": v(14.72, -10.57) * mm});
            skLineSegment(sketch, "E163", {"start": v(15.34, -10.14) * mm, "end": v(15.97, -8.1) * mm});
            skLineSegment(sketch, "E164", {"start": v(15.97, -8.1) * mm, "end": v(16.85, -7.55) * mm});
            skLineSegment(sketch, "E165", {"start": v(16.85, -7.55) * mm, "end": v(22.59, -2.55) * mm});
            skLineSegment(sketch, "E166", {"start": v(22.59, -2.55) * mm, "end": v(22.34, -2.27) * mm});
            skLineSegment(sketch, "E167", {"start": v(22.34, -2.27) * mm, "end": v(23.98, 0.6) * mm});
            skLineSegment(sketch, "E168", {"start": v(23.98, 0.6) * mm, "end": v(23.63, -2.2) * mm});
            skLineSegment(sketch, "E169", {"start": v(23.63, -2.2) * mm, "end": v(23.17, -2.42) * mm});
            skLineSegment(sketch, "E170", {"start": v(23.17, -2.42) * mm, "end": v(17.36, -7.46) * mm});
            skLineSegment(sketch, "E171", {"start": v(17.36, -7.46) * mm, "end": v(17.36, -8.08) * mm});
            skLineSegment(sketch, "E172", {"start": v(17.36, -8.08) * mm, "end": v(15.34, -10.14) * mm});
            skLineSegment(sketch, "E173", {"start": v(15.81, -10.57) * mm, "end": v(19.67, -8) * mm});
            skLineSegment(sketch, "E174", {"start": v(19.67, -8) * mm, "end": v(20.18, -8) * mm});
            skLineSegment(sketch, "E175", {"start": v(20.18, -8) * mm, "end": v(26.03, -2.59) * mm});
            skLineSegment(sketch, "E176", {"start": v(26.03, -2.59) * mm, "end": v(25.73, -2.3) * mm});
            skLineSegment(sketch, "E177", {"start": v(25.73, -2.3) * mm, "end": v(25.16, -0.66) * mm});
            skLineSegment(sketch, "E178", {"start": v(24.42, 0.56) * mm, "end": v(24.05, -2.22) * mm});
            skLineSegment(sketch, "E179", {"start": v(24.05, -2.22) * mm, "end": v(24.35, -2.47) * mm});
            skLineSegment(sketch, "E180", {"start": v(24.35, -2.47) * mm, "end": v(18.36, -7.96) * mm});
            skLineSegment(sketch, "E181", {"start": v(18.36, -7.96) * mm, "end": v(17.77, -7.96) * mm});
            skLineSegment(sketch, "E182", {"start": v(17.77, -7.96) * mm, "end": v(16.57, -9.44) * mm});
            skLineSegment(sketch, "E183", {"start": v(16.57, -9.44) * mm, "end": v(19.14, -7.86) * mm});
            skLineSegment(sketch, "E184", {"start": v(19.14, -7.86) * mm, "end": v(19.27, -7.42) * mm});
            skLineSegment(sketch, "E185", {"start": v(19.27, -7.42) * mm, "end": v(25.02, -2.36) * mm});
            skLineSegment(sketch, "E186", {"start": v(25.02, -2.36) * mm, "end": v(25.28, -2.2) * mm});
            skLineSegment(sketch, "E187", {"start": v(25.28, -2.2) * mm, "end": v(24.67, 0.15) * mm});
            skLineSegment(sketch, "E188.trimOffspring", {"start": v(25.16, -0.66) * mm, "end": v(28.5, -6.11) * mm});
            skLineSegment(sketch, "E189.trimOffspring", {"start": v(14.72, -10.57) * mm, "end": v(5.26, -10.57) * mm});
            skLineSegment(sketch, "E190", {"start": v(21.54, -2.64) * mm, "end": v(16.17, -7.4) * mm});
            skLineSegment(sketch, "E191", {"start": v(16.17, -7.4) * mm, "end": v(16.17, -7.57) * mm});
            skLineSegment(sketch, "E192", {"start": v(16.17, -7.57) * mm, "end": v(21.97, -2.72) * mm});
            skLineSegment(sketch, "E193", {"start": v(21.97, -2.72) * mm, "end": v(21.54, -2.64) * mm});
            skLineSegment(sketch, "E194", {"start": v(23.3, -2.67) * mm, "end": v(17.94, -7.33) * mm});
            skLineSegment(sketch, "E195", {"start": v(17.94, -7.33) * mm, "end": v(18.15, -7.55) * mm});
            skLineSegment(sketch, "E196", {"start": v(18.15, -7.55) * mm, "end": v(23.68, -2.74) * mm});
            skLineSegment(sketch, "E197", {"start": v(23.68, -2.74) * mm, "end": v(23.3, -2.65) * mm});
            skLineSegment(sketch, "E198", {"start": v(25.14, -2.59) * mm, "end": v(19.96, -7.34) * mm});
            skLineSegment(sketch, "E199", {"start": v(19.96, -7.34) * mm, "end": v(20.26, -7.5) * mm});
            skLineSegment(sketch, "E200", {"start": v(20.26, -7.5) * mm, "end": v(25.44, -2.72) * mm});
            skLineSegment(sketch, "E201", {"start": v(25.44, -2.72) * mm, "end": v(25.14, -2.59) * mm});
            skLineSegment(sketch, "E202", {"start": v(5.95, -7.13) * mm, "end": v(6.09, -7.7) * mm});
            skLineSegment(sketch, "E203", {"start": v(6.09, -7.7) * mm, "end": v(7.42, -9.24) * mm});
            skLineSegment(sketch, "E204", {"start": v(7.42, -9.24) * mm, "end": v(7.94, -9.59) * mm});
            skLineSegment(sketch, "E205", {"start": v(7.94, -9.59) * mm, "end": v(8.15, -9.27) * mm});
            skLineSegment(sketch, "E206", {"start": v(8.15, -9.27) * mm, "end": v(7, -7.7) * mm});
            skLineSegment(sketch, "E207", {"start": v(7, -7.7) * mm, "end": v(6.54, -7.24) * mm});
            skLineSegment(sketch, "E208", {"start": v(6.54, -7.24) * mm, "end": v(5.95, -7.13) * mm});
            skLineSegment(sketch, "E209", {"start": v(0.73, -5.95) * mm, "end": v(0.73, -10.05) * mm});
            skLineSegment(sketch, "E210", {"start": v(0.73, -10.05) * mm, "end": v(1.42, -10.05) * mm});
            skLineSegment(sketch, "E211", {"start": v(1.42, -10.05) * mm, "end": v(1.42, -5.95) * mm});
            skLineSegment(sketch, "E212", {"start": v(1.42, -5.95) * mm, "end": v(0.73, -5.95) * mm});
            skLineSegment(sketch, "E213", {"start": v(0.38, -5.6) * mm, "end": v(0.38, -10.36) * mm});
            skLineSegment(sketch, "E214", {"start": v(0.38, -10.36) * mm, "end": v(1.88, -10.36) * mm});
            skLineSegment(sketch, "E215", {"start": v(1.88, -10.36) * mm, "end": v(1.88, -5.64) * mm});
            skLineSegment(sketch, "E216", {"start": v(1.88, -5.64) * mm, "end": v(0.38, -5.6) * mm});
            skLineSegment(sketch, "E217", {"start": v(2.62, -5.89) * mm, "end": v(2.62, -10.32) * mm});
            skLineSegment(sketch, "E218", {"start": v(2.62, -10.32) * mm, "end": v(4.08, -10.32) * mm});
            skLineSegment(sketch, "E219", {"start": v(4.08, -10.32) * mm, "end": v(4.08, -6.24) * mm});
            skLineSegment(sketch, "E220", {"start": v(4.08, -6.24) * mm, "end": v(2.62, -5.89) * mm});
            skLineSegment(sketch, "E221", {"start": v(2.99, -6.4) * mm, "end": v(2.99, -10) * mm});
            skLineSegment(sketch, "E222", {"start": v(2.99, -10) * mm, "end": v(3.69, -10) * mm});
            skLineSegment(sketch, "E223", {"start": v(3.69, -10) * mm, "end": v(3.69, -6.61) * mm});
            skLineSegment(sketch, "E224", {"start": v(3.69, -6.61) * mm, "end": v(2.99, -6.4) * mm});
            skLineSegment(sketch, "E225", {"start": v(0, -5.15) * mm, "end": v(4.08, -5.15) * mm});
            skLineSegment(sketch, "E226", {"start": v(4.08, -5.15) * mm, "end": v(4.08, -3.62) * mm});
            skLineSegment(sketch, "E227", {"start": v(4.08, -3.62) * mm, "end": v(1.33, -3.62) * mm});
            skLineSegment(sketch, "E228", {"start": v(1.33, -3.62) * mm, "end": v(1.33, -2.6) * mm});
            skLineSegment(sketch, "E229", {"start": v(1.33, -2.6) * mm, "end": v(4.08, -2.6) * mm});
            skLineSegment(sketch, "E230", {"start": v(4.08, -2.6) * mm, "end": v(4.08, -1) * mm});
            skLineSegment(sketch, "E231", {"start": v(4.08, -1) * mm, "end": v(1.3, -1) * mm});
            skLineSegment(sketch, "E232", {"start": v(1.3, -1) * mm, "end": v(1.3, 0) * mm});
            skLineSegment(sketch, "E233", {"start": v(1.3, 0) * mm, "end": v(4.08, 0) * mm});
            skLineSegment(sketch, "E234", {"start": v(4.08, 0) * mm, "end": v(4.08, 1.66) * mm});
            skLineSegment(sketch, "E235", {"start": v(4.08, 1.66) * mm, "end": v(1.31, 1.66) * mm});
            skLineSegment(sketch, "E236", {"start": v(1.31, 1.66) * mm, "end": v(1.31, 2.85) * mm});
            skLineSegment(sketch, "E237", {"start": v(1.31, 2.85) * mm, "end": v(4.08, 2.85) * mm});
            skLineSegment(sketch, "E238", {"start": v(4.08, 2.85) * mm, "end": v(4.08, 4.31) * mm});
            skLineSegment(sketch, "E239", {"start": v(4.08, 4.31) * mm, "end": v(1.37, 4.31) * mm});
            skLineSegment(sketch, "E240", {"start": v(1.37, 4.31) * mm, "end": v(1.37, 5.32) * mm});
            skLineSegment(sketch, "E241", {"start": v(1.37, 5.32) * mm, "end": v(4.8, 5.32) * mm});
            skLineSegment(sketch, "E242", {"start": v(4.8, 5.32) * mm, "end": v(5, 5.71) * mm});
            skLineSegment(sketch, "E243", {"start": v(5.03, 6.41) * mm, "end": v(4.76, 6.93) * mm});
            skLineSegment(sketch, "E244", {"start": v(4.76, 6.93) * mm, "end": v(0, 6.93) * mm});
            skLineSegment(sketch, "E245", {"start": v(0, 6.93) * mm, "end": v(0, 6.32) * mm});
            skLineSegment(sketch, "E246", {"start": v(0, 6.32) * mm, "end": v(4.41, 6.32) * mm});
            skLineSegment(sketch, "E247", {"start": v(4.41, 6.32) * mm, "end": v(4.41, 5.87) * mm});
            skLineSegment(sketch, "E248", {"start": v(4.41, 5.87) * mm, "end": v(0, 5.87) * mm});
            skLineSegment(sketch, "E249", {"start": v(0, 5.87) * mm, "end": v(0, 3.95) * mm});
            skLineSegment(sketch, "E250", {"start": v(0, 3.95) * mm, "end": v(3.52, 3.95) * mm});
            skLineSegment(sketch, "E251", {"start": v(3.52, 3.95) * mm, "end": v(3.52, 3.31) * mm});
            skLineSegment(sketch, "E252", {"start": v(3.52, 3.31) * mm, "end": v(0, 3.31) * mm});
            skLineSegment(sketch, "E253", {"start": v(0, 3.31) * mm, "end": v(0, 1.33) * mm});
            skLineSegment(sketch, "E254", {"start": v(0, 1.33) * mm, "end": v(3.54, 1.33) * mm});
            skLineSegment(sketch, "E255", {"start": v(3.54, 1.33) * mm, "end": v(3.6, 0.7) * mm});
            skLineSegment(sketch, "E256", {"start": v(3.6, 0.7) * mm, "end": v(0, 0.7) * mm});
            skLineSegment(sketch, "E257", {"start": v(0, 0.7) * mm, "end": v(0, -1.45) * mm});
            skLineSegment(sketch, "E258", {"start": v(0, -1.45) * mm, "end": v(3.57, -1.45) * mm});
            skLineSegment(sketch, "E259", {"start": v(3.57, -1.45) * mm, "end": v(3.57, -1.94) * mm});
            skLineSegment(sketch, "E260", {"start": v(3.57, -1.94) * mm, "end": v(0, -1.94) * mm});
            skLineSegment(sketch, "E261", {"start": v(0, -1.94) * mm, "end": v(0, -4.04) * mm});
            skLineSegment(sketch, "E262", {"start": v(0, -4.04) * mm, "end": v(3.66, -4.04) * mm});
            skLineSegment(sketch, "E263", {"start": v(3.66, -4.04) * mm, "end": v(3.66, -4.51) * mm});
            skLineSegment(sketch, "E264", {"start": v(3.66, -4.51) * mm, "end": v(0, -4.51) * mm});
            skLineSegment(sketch, "E265", {"start": v(0, -4.51) * mm, "end": v(0, -5.15) * mm});
            skLineSegment(sketch, "E266", {"start": v(5.26, -10.57) * mm, "end": v(5.26, 2.61) * mm});
            skLineSegment(sketch, "E267", {"start": v(5.26, 2.61) * mm, "end": v(10.35, 2.61) * mm});
            skLineSegment(sketch, "E268", {"start": v(10.35, 2.61) * mm, "end": v(10.35, -1.93) * mm});
            skLineSegment(sketch, "E269", {"start": v(10.8, -1.8) * mm, "end": v(10.8, 3.08) * mm});
            skLineSegment(sketch, "E270", {"start": v(10.8, 3.08) * mm, "end": v(5.26, 3.08) * mm});
            skLineSegment(sketch, "E271", {"start": v(5.26, 3.08) * mm, "end": v(5.26, 3.85) * mm});
            skLineSegment(sketch, "E272", {"start": v(5.26, 3.85) * mm, "end": v(10.74, 3.85) * mm});
            skLineSegment(sketch, "E273", {"start": v(10.74, 3.85) * mm, "end": v(10.74, 10.22) * mm});
            skLineSegment(sketch, "E274", {"start": v(10.74, 10.22) * mm, "end": v(19.08, 10.22) * mm});
            skLineSegment(sketch, "E275", {"start": v(19.08, 10.22) * mm, "end": v(18.09, 11.89) * mm});
            skLineSegment(sketch, "E276", {"start": v(18.09, 11.89) * mm, "end": v(9.1, 11.89) * mm});
            skLineSegment(sketch, "E277", {"start": v(9.1, 11.89) * mm, "end": v(9.1, 5.62) * mm});
            skLineSegment(sketch, "E278", {"start": v(9.1, 5.62) * mm, "end": v(8.22, 5.62) * mm});
            skLineSegment(sketch, "E279", {"start": v(8.22, 5.62) * mm, "end": v(8.22, 12.58) * mm});
            skLineSegment(sketch, "E280", {"start": v(8.22, 12.58) * mm, "end": v(17.56, 12.58) * mm});
            skLineSegment(sketch, "E281", {"start": v(17.56, 12.58) * mm, "end": v(10.43, 24.17) * mm});
            skLineSegment(sketch, "E282", {"start": v(10.2, 23.9) * mm, "end": v(10.93, 22.77) * mm});
            skLineSegment(sketch, "E283", {"start": v(10.93, 22.77) * mm, "end": v(6, 18.66) * mm});
            skLineSegment(sketch, "E284", {"start": v(6, 18.66) * mm, "end": v(6, 6.41) * mm});
            skLineSegment(sketch, "E285", {"start": v(6, 6.41) * mm, "end": v(5.03, 6.41) * mm});
            skLineSegment(sketch, "E286", {"start": v(5, 5.71) * mm, "end": v(5.75, 5.71) * mm});
            skLineSegment(sketch, "E287", {"start": v(5.75, 5.71) * mm, "end": v(4.7, 4.16) * mm});
            skLineSegment(sketch, "E288", {"start": v(4.7, 4.16) * mm, "end": v(4.7, -10.57) * mm});
            skLineSegment(sketch, "E289.trimOffspring", {"start": v(4.7, -10.57) * mm, "end": v(0, -10.57) * mm});
            skPoint(sketch, "E290.orphan", {"position": v(5.19, 6.1) * mm});
            skLineSegment(sketch, "E291", {"start": v(5.64, 4.72) * mm, "end": v(5.42, 4.39) * mm});
            skLineSegment(sketch, "E292", {"start": v(5.42, 4.39) * mm, "end": v(10.37, 4.39) * mm});
            skLineSegment(sketch, "E293", {"start": v(10.37, 4.39) * mm, "end": v(10.37, 10.47) * mm});
            skLineSegment(sketch, "E294", {"start": v(10.37, 10.47) * mm, "end": v(18.57, 10.47) * mm});
            skLineSegment(sketch, "E295", {"start": v(18.57, 10.47) * mm, "end": v(18.3, 10.88) * mm});
            skLineSegment(sketch, "E296", {"start": v(18.3, 10.88) * mm, "end": v(9.91, 10.88) * mm});
            skLineSegment(sketch, "E297", {"start": v(9.91, 10.88) * mm, "end": v(9.91, 4.7) * mm});
            skLineSegment(sketch, "E298", {"start": v(9.91, 4.7) * mm, "end": v(5.64, 4.72) * mm});
            skLineSegment(sketch, "E299", {"start": v(5.79, 5.1) * mm, "end": v(9.63, 5.1) * mm});
            skLineSegment(sketch, "E300", {"start": v(9.63, 5.1) * mm, "end": v(9.63, 11.12) * mm});
            skLineSegment(sketch, "E301", {"start": v(9.63, 11.12) * mm, "end": v(18.07, 11.12) * mm});
            skLineSegment(sketch, "E302", {"start": v(18.07, 11.12) * mm, "end": v(17.87, 11.53) * mm});
            skLineSegment(sketch, "E303", {"start": v(17.87, 11.53) * mm, "end": v(9.46, 11.53) * mm});
            skLineSegment(sketch, "E304", {"start": v(9.46, 11.53) * mm, "end": v(9.46, 5.36) * mm});
            skLineSegment(sketch, "E305", {"start": v(9.46, 5.36) * mm, "end": v(7.77, 5.36) * mm});
            skLineSegment(sketch, "E306", {"start": v(7.77, 5.36) * mm, "end": v(7.77, 13.01) * mm});
            skLineSegment(sketch, "E307", {"start": v(7.77, 13.01) * mm, "end": v(16.8, 13.01) * mm});
            skLineSegment(sketch, "E308", {"start": v(16.8, 13.01) * mm, "end": v(11.2, 22.31) * mm});
            skLineSegment(sketch, "E309", {"start": v(11.2, 22.31) * mm, "end": v(6.33, 18.38) * mm});
            skLineSegment(sketch, "E310", {"start": v(6.33, 18.38) * mm, "end": v(6.33, 5.98) * mm});
            skLineSegment(sketch, "E311", {"start": v(6.33, 5.98) * mm, "end": v(5.79, 5.1) * mm});
            skLineSegment(sketch, "E312", {"start": v(11.53, 9.3) * mm, "end": v(11.53, 1.96) * mm});
            skLineSegment(sketch, "E313", {"start": v(11.53, 1.96) * mm, "end": v(24.14, 2.17) * mm});
            skLineSegment(sketch, "E314", {"start": v(24.14, 2.17) * mm, "end": v(19.7, 9.42) * mm});
            skLineSegment(sketch, "E315", {"start": v(19.7, 9.42) * mm, "end": v(11.53, 9.3) * mm});
            skLineSegment(sketch, "E316", {"start": v(11.8, 9.03) * mm, "end": v(17.98, 9.13) * mm});
            skLineSegment(sketch, "E317", {"start": v(17.98, 9.13) * mm, "end": v(17.68, 8.78) * mm});
            skLineSegment(sketch, "E318", {"start": v(18.39, 9.16) * mm, "end": v(19.53, 9.16) * mm});
            skLineSegment(sketch, "E319", {"start": v(19.53, 9.16) * mm, "end": v(19.78, 8.67) * mm});
            skLineSegment(sketch, "E320", {"start": v(19.78, 8.67) * mm, "end": v(18.56, 7.15) * mm});
            skLineSegment(sketch, "E321", {"start": v(18.63, 6.76) * mm, "end": v(19.83, 8.26) * mm});
            skLineSegment(sketch, "E322", {"start": v(19.83, 8.26) * mm, "end": v(20.6, 7.25) * mm});
            skLineSegment(sketch, "E323", {"start": v(20.6, 7.25) * mm, "end": v(19.29, 5.65) * mm});
            skLineSegment(sketch, "E324", {"start": v(11.8, 9.03) * mm, "end": v(11.86, 5.88) * mm});
            skLineSegment(sketch, "E325", {"start": v(11.86, 5.88) * mm, "end": v(12.66, 5.88) * mm});
            skLineSegment(sketch, "E326", {"start": v(12.66, 5.88) * mm, "end": v(12.66, 7.13) * mm});
            skLineSegment(sketch, "E327", {"start": v(16.29, 3.54) * mm, "end": v(15.92, 4.36) * mm});
            skLineSegment(sketch, "E328", {"start": v(15.92, 4.36) * mm, "end": v(11.91, 4.36) * mm});
            skLineSegment(sketch, "E329", {"start": v(11.91, 4.36) * mm, "end": v(11.91, 2.21) * mm});
            skLineSegment(sketch, "E330", {"start": v(11.91, 2.21) * mm, "end": v(23.54, 2.43) * mm});
            skLineSegment(sketch, "E331", {"start": v(23.54, 2.43) * mm, "end": v(21.78, 5.32) * mm});
            skLineSegment(sketch, "E332", {"start": v(21.78, 5.32) * mm, "end": v(20.21, 3.7) * mm});
            skLineSegment(sketch, "E333", {"start": v(19.85, 3.95) * mm, "end": v(21.48, 5.69) * mm});
            skLineSegment(sketch, "E334", {"start": v(21.48, 5.69) * mm, "end": v(20.8, 6.85) * mm});
            skLineSegment(sketch, "E335", {"start": v(20.8, 6.85) * mm, "end": v(19.5, 5.43) * mm});
            skLineSegment(sketch, "E336", {"start": v(18.39, 9.16) * mm, "end": v(18, 8.56) * mm});
            skLineSegment(sketch, "E337.bottom", {"start": v(11.83, 5.56) * mm, "end": v(12.6, 5.56) * mm});
            skLineSegment(sketch, "E337.top", {"start": v(11.83, 5.09) * mm, "end": v(12.6, 5.09) * mm});
            skLineSegment(sketch, "E337.left", {"start": v(11.83, 5.56) * mm, "end": v(11.83, 5.09) * mm});
            skLineSegment(sketch, "E337.right", {"start": v(12.6, 5.56) * mm, "end": v(12.6, 5.09) * mm});
            skLineSegment(sketch, "E338.bottom", {"start": v(13.14, 5.99) * mm, "end": v(15.22, 5.99) * mm});
            skLineSegment(sketch, "E338.top", {"start": v(13.14, 5.54) * mm, "end": v(15.22, 5.54) * mm});
            skLineSegment(sketch, "E338.left", {"start": v(13.14, 5.99) * mm, "end": v(13.14, 5.54) * mm});
            skLineSegment(sketch, "E338.right", {"start": v(15.22, 5.99) * mm, "end": v(15.22, 5.54) * mm});
            skLineSegment(sketch, "E339", {"start": v(13.1, 7.13) * mm, "end": v(13.1, 6.33) * mm});
            skLineSegment(sketch, "E340", {"start": v(13.1, 6.33) * mm, "end": v(15.07, 6.33) * mm});
            skLineSegment(sketch, "E341", {"start": v(15.07, 6.33) * mm, "end": v(14.2, 8.2) * mm});
            skLineSegment(sketch, "E342", {"start": v(14.2, 8.2) * mm, "end": v(14.72, 8.82) * mm});
            skLineSegment(sketch, "E343", {"start": v(14.72, 8.2) * mm, "end": v(16.6, 3.5) * mm});
            skArc(sketch, "E344", {"start": v(14.72, 8.82) * mm, "mid": v(16.2, 8.28) * mm, "end": v(17.68, 8.78) * mm});
            skArc(sketch, "E345", {"start": v(14.85, 8.37) * mm, "mid": v(14.74, 8.32) * mm, "end": v(14.72, 8.2) * mm});
            skArc(sketch, "E346", {"start": v(14.85, 8.37) * mm, "mid": v(16.3, 7.96) * mm, "end": v(17.68, 8.53) * mm});
            skArc(sketch, "E347", {"start": v(15.72, 7.32) * mm, "mid": v(17.12, 7.47) * mm, "end": v(18, 8.56) * mm});
            skArc(sketch, "E348", {"start": v(15.24, 7.73) * mm, "mid": v(16.63, 7.61) * mm, "end": v(17.68, 8.53) * mm});
            skArc(sketch, "E349", {"start": v(15.24, 7.73) * mm, "mid": v(16.43, 6.3) * mm, "end": v(18.21, 6.87) * mm});
            skArc(sketch, "E350", {"start": v(15.72, 7.32) * mm, "mid": v(16.91, 6.53) * mm, "end": v(18.21, 7.12) * mm});
            skArc(sketch, "E351", {"start": v(15.97, 6.06) * mm, "mid": v(17.26, 5.87) * mm, "end": v(18.37, 6.54) * mm});
            skArc(sketch, "E352", {"start": v(16.3, 5.66) * mm, "mid": v(17.6, 5.7) * mm, "end": v(18.64, 6.47) * mm});
            skArc(sketch, "E353", {"start": v(15.97, 6.06) * mm, "mid": v(17.22, 4.76) * mm, "end": v(18.93, 5.28) * mm});
            skArc(sketch, "E354", {"start": v(16.3, 5.66) * mm, "mid": v(17.8, 5.3) * mm, "end": v(19.29, 5.65) * mm});
            skArc(sketch, "E355", {"start": v(17.2, 4.05) * mm, "mid": v(18.48, 4.15) * mm, "end": v(19.47, 4.97) * mm});
            skArc(sketch, "E356", {"start": v(16.71, 4.4) * mm, "mid": v(18, 4.32) * mm, "end": v(19.1, 5) * mm});
            skArc(sketch, "E357", {"start": v(16.71, 4.4) * mm, "mid": v(17.87, 3.04) * mm, "end": v(19.54, 3.62) * mm});
            skArc(sketch, "E358", {"start": v(17.2, 4.05) * mm, "mid": v(18.35, 3.4) * mm, "end": v(19.5, 4.05) * mm});
            skArc(sketch, "E359", {"start": v(16.84, 2.86) * mm, "mid": v(18.54, 2.48) * mm, "end": v(20.05, 3.33) * mm});
            skArc(sketch, "E360", {"start": v(16.88, 3.13) * mm, "mid": v(18.34, 2.67) * mm, "end": v(19.69, 3.4) * mm});
            skArc(sketch, "E361", {"start": v(13.76, 3.4) * mm, "mid": v(15.18, 2.48) * mm, "end": v(16.84, 2.86) * mm});
            skArc(sketch, "E362", {"start": v(14.12, 3.46) * mm, "mid": v(15.43, 2.73) * mm, "end": v(16.88, 3.13) * mm});
            skArc(sketch, "E363", {"start": v(14.12, 3.46) * mm, "mid": v(15.37, 3) * mm, "end": v(16.6, 3.5) * mm});
            skArc(sketch, "E364", {"start": v(14.12, 4.05) * mm, "mid": v(15.1, 3.36) * mm, "end": v(16.29, 3.54) * mm});
            skLineSegment(sketch, "E365", {"start": v(13.76, 3.4) * mm, "end": v(14.12, 4.05) * mm});
            skArc(sketch, "E366", {"start": v(13.1, 7.13) * mm, "mid": v(12.88, 8.36) * mm, "end": v(12.66, 7.13) * mm});
            skLineSegment(sketch, "E367", {"start": v(18.21, 7.12) * mm, "end": v(18.56, 7.15) * mm});
            skLineSegment(sketch, "E368", {"start": v(18.63, 6.76) * mm, "end": v(18.64, 6.47) * mm});
            skLineSegment(sketch, "E369", {"start": v(18.21, 6.87) * mm, "end": v(18.37, 6.54) * mm});
            skLineSegment(sketch, "E370", {"start": v(18.93, 5.28) * mm, "end": v(19.1, 5) * mm});
            skLineSegment(sketch, "E371", {"start": v(19.5, 5.43) * mm, "end": v(19.47, 4.97) * mm});
            skLineSegment(sketch, "E372", {"start": v(19.5, 4.05) * mm, "end": v(19.85, 3.95) * mm});
            skLineSegment(sketch, "E373", {"start": v(19.54, 3.62) * mm, "end": v(19.69, 3.4) * mm});
            skLineSegment(sketch, "E374", {"start": v(20.21, 3.7) * mm, "end": v(20.05, 3.33) * mm});
            skLineSegment(sketch, "E375", {"start": v(17.07, -1.21) * mm, "end": v(17.07, 0.93) * mm});
            skLineSegment(sketch, "E376", {"start": v(17.07, 0.93) * mm, "end": v(17.88, 0.91) * mm});
            skLineSegment(sketch, "E377", {"start": v(17.88, 0.91) * mm, "end": v(17.84, -1.18) * mm});
            skLineSegment(sketch, "E378", {"start": v(17.32, 0.68) * mm, "end": v(17.32, -1.5) * mm});
            skLineSegment(sketch, "E379", {"start": v(17.66, -1.5) * mm, "end": v(17.66, 0.7) * mm});
            skLineSegment(sketch, "E380", {"start": v(17.66, 0.7) * mm, "end": v(17.32, 0.68) * mm});
            skArc(sketch, "E381", {"start": v(17.07, -1.21) * mm, "mid": v(16.61, -1.46) * mm, "end": v(16.27, -1.84) * mm});
            skArc(sketch, "E382", {"start": v(16.38, -3.53) * mm, "mid": v(16.76, -2.66) * mm, "end": v(16.27, -1.84) * mm});
            skArc(sketch, "E383", {"start": v(17.32, -1.5) * mm, "mid": v(17.08, -1.57) * mm, "end": v(16.86, -1.68) * mm});
            skArc(sketch, "E384", {"start": v(16.92, -3.64) * mm, "mid": v(17.19, -2.65) * mm, "end": v(16.86, -1.68) * mm});
            skArc(sketch, "E385.trimOffspring", {"start": v(16.92, -3.64) * mm, "mid": v(18.58, -3.02) * mm, "end": v(17.66, -1.5) * mm});
            skArc(sketch, "E386.trimOffspring", {"start": v(16.38, -3.53) * mm, "mid": v(18.77, -3.39) * mm, "end": v(17.84, -1.18) * mm});
            skLineSegment(sketch, "E387", {"start": v(0, 16.6) * mm, "end": v(0, 17.1) * mm});
            skLineSegment(sketch, "E388", {"start": v(0, 17.1) * mm, "end": v(4.99, 17) * mm});
            skLineSegment(sketch, "E389", {"start": v(4.99, 17) * mm, "end": v(4.99, 7.84) * mm});
            skLineSegment(sketch, "E390", {"start": v(4.99, 7.84) * mm, "end": v(0, 7.84) * mm});
            skLineSegment(sketch, "E391", {"start": v(0, 7.84) * mm, "end": v(0, 8.3) * mm});
            skLineSegment(sketch, "E392", {"start": v(0, 8.3) * mm, "end": v(4.56, 8.3) * mm});
            skLineSegment(sketch, "E393", {"start": v(4.56, 8.3) * mm, "end": v(4.56, 16.6) * mm});
            skLineSegment(sketch, "E394", {"start": v(4.56, 16.6) * mm, "end": v(0, 16.6) * mm});
            skLineSegment(sketch, "E395", {"start": v(0, 15.86) * mm, "end": v(4, 15.86) * mm});
            skLineSegment(sketch, "E396", {"start": v(4, 15.86) * mm, "end": v(4, 9.15) * mm});
            skLineSegment(sketch, "E397", {"start": v(4, 9.15) * mm, "end": v(0, 9.15) * mm});
            skLineSegment(sketch, "E398", {"start": v(0, 9.15) * mm, "end": v(0, 10.88) * mm});
            skLineSegment(sketch, "E399", {"start": v(0, 10.88) * mm, "end": v(2.3, 10.88) * mm});
            skLineSegment(sketch, "E400", {"start": v(2.3, 10.88) * mm, "end": v(2.3, 11.52) * mm});
            skLineSegment(sketch, "E401", {"start": v(2.3, 11.52) * mm, "end": v(0, 11.52) * mm});
            skLineSegment(sketch, "E402", {"start": v(0, 11.52) * mm, "end": v(0, 13.48) * mm});
            skLineSegment(sketch, "E403", {"start": v(0, 13.48) * mm, "end": v(2.38, 13.46) * mm});
            skLineSegment(sketch, "E404", {"start": v(2.38, 13.46) * mm, "end": v(2.4, 13.97) * mm});
            skLineSegment(sketch, "E405", {"start": v(2.4, 13.97) * mm, "end": v(0, 14.03) * mm});
            skLineSegment(sketch, "E406", {"start": v(0, 14.03) * mm, "end": v(0, 15.86) * mm});
            skLineSegment(sketch, "E407", {"start": v(1.25, 15.4) * mm, "end": v(1.03, 14.6) * mm});
            skLineSegment(sketch, "E408", {"start": v(1.03, 14.6) * mm, "end": v(2.8, 14.55) * mm});
            skLineSegment(sketch, "E409", {"start": v(2.8, 14.55) * mm, "end": v(2.8, 12.87) * mm});
            skLineSegment(sketch, "E410", {"start": v(2.8, 12.87) * mm, "end": v(1.34, 12.88) * mm});
            skLineSegment(sketch, "E411", {"start": v(1.34, 12.88) * mm, "end": v(1.3, 12.12) * mm});
            skLineSegment(sketch, "E412", {"start": v(1.3, 12.12) * mm, "end": v(2.82, 12.04) * mm});
            skLineSegment(sketch, "E413", {"start": v(2.82, 12.04) * mm, "end": v(2.86, 10.42) * mm});
            skLineSegment(sketch, "E414", {"start": v(2.86, 10.42) * mm, "end": v(1.31, 10.32) * mm});
            skLineSegment(sketch, "E415", {"start": v(1.31, 10.32) * mm, "end": v(1.33, 9.68) * mm});
            skLineSegment(sketch, "E416", {"start": v(1.33, 9.68) * mm, "end": v(3.42, 9.7) * mm});
            skLineSegment(sketch, "E417", {"start": v(3.42, 9.7) * mm, "end": v(3.57, 15.45) * mm});
            skLineSegment(sketch, "E418", {"start": v(3.57, 15.45) * mm, "end": v(1.25, 15.4) * mm});
            skLineSegment(sketch, "E419.bottom", {"start": v(10.91, 15.1) * mm, "end": v(14.36, 15.1) * mm});
            skLineSegment(sketch, "E419.top", {"start": v(10.91, 14.35) * mm, "end": v(14.36, 14.35) * mm});
            skLineSegment(sketch, "E419.left", {"start": v(10.91, 15.1) * mm, "end": v(10.91, 14.35) * mm});
            skLineSegment(sketch, "E419.right", {"start": v(14.36, 15.1) * mm, "end": v(14.36, 14.35) * mm});
            skLineSegment(sketch, "E420.bottom", {"start": v(13.9, 14.15) * mm, "end": v(14.9, 14.15) * mm});
            skLineSegment(sketch, "E420.top", {"start": v(13.9, 13.46) * mm, "end": v(14.9, 13.46) * mm});
            skLineSegment(sketch, "E420.left", {"start": v(13.9, 14.15) * mm, "end": v(13.9, 13.46) * mm});
            skLineSegment(sketch, "E420.right", {"start": v(14.9, 14.15) * mm, "end": v(14.9, 13.46) * mm});
            skLineSegment(sketch, "E421.bottom", {"start": v(12.43, 14.16) * mm, "end": v(13.55, 14.16) * mm});
            skLineSegment(sketch, "E421.top", {"start": v(12.43, 13.46) * mm, "end": v(13.55, 13.46) * mm});
            skLineSegment(sketch, "E421.left", {"start": v(12.43, 14.16) * mm, "end": v(12.43, 13.46) * mm});
            skLineSegment(sketch, "E421.right", {"start": v(13.55, 14.16) * mm, "end": v(13.55, 13.46) * mm});
            skLineSegment(sketch, "E422.bottom", {"start": v(11, 14) * mm, "end": v(12.02, 14) * mm});
            skLineSegment(sketch, "E422.top", {"start": v(11, 13.4) * mm, "end": v(12.02, 13.4) * mm});
            skLineSegment(sketch, "E422.left", {"start": v(11, 14) * mm, "end": v(11, 13.4) * mm});
            skLineSegment(sketch, "E422.right", {"start": v(12.02, 14) * mm, "end": v(12.02, 13.4) * mm});
            skLineSegment(sketch, "E423.bottom", {"start": v(9.96, 14.79) * mm, "end": v(10.54, 14.79) * mm});
            skLineSegment(sketch, "E423.top", {"start": v(9.96, 13.32) * mm, "end": v(10.54, 13.32) * mm});
            skLineSegment(sketch, "E423.left", {"start": v(9.96, 14.79) * mm, "end": v(9.96, 13.32) * mm});
            skLineSegment(sketch, "E423.right", {"start": v(10.54, 14.79) * mm, "end": v(10.54, 13.32) * mm});
            skLineSegment(sketch, "E424", {"start": v(0, 40.73) * mm, "end": v(2.2, 37.4) * mm});
            skLineSegment(sketch, "E425", {"start": v(2.2, 37.4) * mm, "end": v(0.72, 37.21) * mm});
            skLineSegment(sketch, "E426", {"start": v(0.72, 37.21) * mm, "end": v(0.72, 36.54) * mm});
            skLineSegment(sketch, "E427", {"start": v(0.72, 36.54) * mm, "end": v(1.84, 36.5) * mm});
            skLineSegment(sketch, "E428", {"start": v(1.84, 36.5) * mm, "end": v(0.8, 33.87) * mm});
            skLineSegment(sketch, "E429", {"start": v(0.8, 33.87) * mm, "end": v(0.72, 31.9) * mm});
            skLineSegment(sketch, "E430", {"start": v(0.72, 31.9) * mm, "end": v(1.15, 31.98) * mm});
            skLineSegment(sketch, "E431", {"start": v(1.15, 31.98) * mm, "end": v(1.38, 34.17) * mm});
            skLineSegment(sketch, "E432", {"start": v(1.38, 34.17) * mm, "end": v(2.78, 36.52) * mm});
            skLineSegment(sketch, "E433", {"start": v(2.78, 36.52) * mm, "end": v(4.9, 33.1) * mm});
            skArc(sketch, "E434", {"start": v(4.9, 33.1) * mm, "mid": v(3.73, 31.75) * mm, "end": v(3.22, 30.04) * mm});
            skArc(sketch, "E435", {"start": v(5.09, 32.8) * mm, "mid": v(3.85, 31.63) * mm, "end": v(3.22, 30.04) * mm});
            skLineSegment(sketch, "E436", {"start": v(5.09, 32.8) * mm, "end": v(6.5, 30.53) * mm});
            skLineSegment(sketch, "E437", {"start": v(6.5, 30.53) * mm, "end": v(4.18, 29.27) * mm});
            skLineSegment(sketch, "E438", {"start": v(4.18, 29.27) * mm, "end": v(4.27, 29.05) * mm});
            skLineSegment(sketch, "E439", {"start": v(4.27, 29.05) * mm, "end": v(6.65, 30.22) * mm});
            skLineSegment(sketch, "E440", {"start": v(6.65, 30.22) * mm, "end": v(7.18, 29.39) * mm});
            skLineSegment(sketch, "E441", {"start": v(7.18, 29.39) * mm, "end": v(4.91, 28.3) * mm});
            skLineSegment(sketch, "E442", {"start": v(4.91, 28.3) * mm, "end": v(5.05, 28.04) * mm});
            skLineSegment(sketch, "E443", {"start": v(5.05, 28.04) * mm, "end": v(7.33, 29.05) * mm});
            skLineSegment(sketch, "E444", {"start": v(7.33, 29.05) * mm, "end": v(7.83, 28.26) * mm});
            skLineSegment(sketch, "E445", {"start": v(7.83, 28.26) * mm, "end": v(5.49, 27.25) * mm});
            skLineSegment(sketch, "E446", {"start": v(5.49, 27.25) * mm, "end": v(5.6, 26.93) * mm});
            skLineSegment(sketch, "E447", {"start": v(5.6, 26.93) * mm, "end": v(8.05, 27.92) * mm});
            skLineSegment(sketch, "E448", {"start": v(8.05, 27.92) * mm, "end": v(8.52, 27.16) * mm});
            skLineSegment(sketch, "E449", {"start": v(8.52, 27.16) * mm, "end": v(5.96, 26.04) * mm});
            skLineSegment(sketch, "E450", {"start": v(5.96, 26.04) * mm, "end": v(6.05, 25.83) * mm});
            skLineSegment(sketch, "E451", {"start": v(6.05, 25.83) * mm, "end": v(8.75, 26.76) * mm});
            skLineSegment(sketch, "E452", {"start": v(8.75, 26.76) * mm, "end": v(9.26, 25.9) * mm});
            skLineSegment(sketch, "E453", {"start": v(9.26, 25.9) * mm, "end": v(6.42, 24.93) * mm});
            skLineSegment(sketch, "E454", {"start": v(6.42, 24.93) * mm, "end": v(6.42, 24.67) * mm});
            skLineSegment(sketch, "E455", {"start": v(6.42, 24.67) * mm, "end": v(9.5, 25.5) * mm});
            skLineSegment(sketch, "E456", {"start": v(9.5, 25.5) * mm, "end": v(10.01, 24.7) * mm});
            skLineSegment(sketch, "E457", {"start": v(10.01, 24.7) * mm, "end": v(6.71, 23.82) * mm});
            skLineSegment(sketch, "E458", {"start": v(6.71, 23.82) * mm, "end": v(6.8, 23.6) * mm});
            skLineSegment(sketch, "E459", {"start": v(6.8, 23.6) * mm, "end": v(10.34, 24.35) * mm});
            skLineSegment(sketch, "E460", {"start": v(10.34, 24.35) * mm, "end": v(10.43, 24.17) * mm});
            skLineSegment(sketch, "E461", {"start": v(10.2, 23.9) * mm, "end": v(8.1, 23.63) * mm});
            skLineSegment(sketch, "E462", {"start": v(8.1, 23.63) * mm, "end": v(6.39, 22.7) * mm});
            skLineSegment(sketch, "E463", {"start": v(6.39, 22.7) * mm, "end": v(4.62, 22.7) * mm});
            skArc(sketch, "E464", {"start": v(4.62, 22.7) * mm, "mid": v(3.58, 26.79) * mm, "end": v(0, 29) * mm});
            skLineSegment(sketch, "E465", {"start": v(0, 29) * mm, "end": v(0, 30.76) * mm});
            skArc(sketch, "E466", {"start": v(2.68, 29.86) * mm, "mid": v(1.45, 30.64) * mm, "end": v(0, 30.76) * mm});
            skArc(sketch, "E467", {"start": v(4.27, 33.04) * mm, "mid": v(3.1, 31.63) * mm, "end": v(2.68, 29.86) * mm});
            skLineSegment(sketch, "E468", {"start": v(0.74, 30.22) * mm, "end": v(0.74, 29.43) * mm});
            skArc(sketch, "E469", {"start": v(5, 23.26) * mm, "mid": v(3.87, 27.04) * mm, "end": v(0.74, 29.43) * mm});
            skLineSegment(sketch, "E470", {"start": v(5, 23.26) * mm, "end": v(5.5, 23.26) * mm});
            skArc(sketch, "E471", {"start": v(5.5, 23.26) * mm, "mid": v(4.3, 27.56) * mm, "end": v(0.74, 30.22) * mm});
            skLineSegment(sketch, "E472", {"start": v(4.27, 33.04) * mm, "end": v(2.7, 35.4) * mm});
            skLineSegment(sketch, "E473", {"start": v(2.7, 35.4) * mm, "end": v(1.95, 33.82) * mm});
            skLineSegment(sketch, "E474", {"start": v(1.95, 33.82) * mm, "end": v(1.65, 31.45) * mm});
            skLineSegment(sketch, "E475", {"start": v(1.65, 31.45) * mm, "end": v(0.37, 31.45) * mm});
            skLineSegment(sketch, "E476", {"start": v(0.37, 31.45) * mm, "end": v(0.37, 33.76) * mm});
            skLineSegment(sketch, "E477", {"start": v(0.37, 33.76) * mm, "end": v(1.13, 35.85) * mm});
            skLineSegment(sketch, "E478", {"start": v(1.13, 35.85) * mm, "end": v(0.32, 36.14) * mm});
            skLineSegment(sketch, "E479", {"start": v(0.32, 36.14) * mm, "end": v(0.32, 37.67) * mm});
            skLineSegment(sketch, "E480", {"start": v(0.32, 37.67) * mm, "end": v(1.37, 37.73) * mm});
            skLineSegment(sketch, "E481", {"start": v(1.37, 37.73) * mm, "end": v(0, 39.27) * mm});
            skLineSegment(sketch, "E482", {"start": v(0, 39.27) * mm, "end": v(0, 40.73) * mm});
            skArc(sketch, "E483", {"start": v(4.82, 32.05) * mm, "mid": v(3.84, 30.93) * mm, "end": v(3.58, 29.47) * mm});
            skLineSegment(sketch, "E484", {"start": v(4.82, 32.05) * mm, "end": v(5.8, 30.65) * mm});
            skLineSegment(sketch, "E485", {"start": v(5.8, 30.65) * mm, "end": v(3.58, 29.47) * mm});
            skLineSegment(sketch, "E486", {"start": v(4.4, 28.7) * mm, "end": v(6.53, 29.84) * mm});
            skLineSegment(sketch, "E487", {"start": v(6.53, 29.84) * mm, "end": v(6.66, 29.54) * mm});
            skLineSegment(sketch, "E488", {"start": v(6.66, 29.54) * mm, "end": v(4.46, 28.4) * mm});
            skLineSegment(sketch, "E489", {"start": v(4.46, 28.4) * mm, "end": v(4.4, 28.7) * mm});
            skLineSegment(sketch, "E490", {"start": v(7.1, 28.58) * mm, "end": v(5.16, 27.55) * mm});
            skLineSegment(sketch, "E491", {"start": v(5.16, 27.55) * mm, "end": v(5.23, 27.4) * mm});
            skLineSegment(sketch, "E492", {"start": v(5.23, 27.4) * mm, "end": v(7.2, 28.4) * mm});
            skLineSegment(sketch, "E493", {"start": v(7.2, 28.4) * mm, "end": v(7.1, 28.58) * mm});
            skLineSegment(sketch, "E494", {"start": v(7.68, 27.39) * mm, "end": v(5.66, 26.5) * mm});
            skLineSegment(sketch, "E495", {"start": v(5.66, 26.5) * mm, "end": v(5.65, 26.34) * mm});
            skLineSegment(sketch, "E496", {"start": v(5.65, 26.34) * mm, "end": v(7.8, 27.23) * mm});
            skLineSegment(sketch, "E497", {"start": v(7.8, 27.23) * mm, "end": v(7.68, 27.39) * mm});
            skLineSegment(sketch, "E498", {"start": v(8.49, 26.28) * mm, "end": v(5.96, 25.47) * mm});
            skLineSegment(sketch, "E499", {"start": v(5.96, 25.47) * mm, "end": v(6.03, 25.2) * mm});
            skLineSegment(sketch, "E500", {"start": v(6.03, 25.2) * mm, "end": v(8.62, 26.1) * mm});
            skLineSegment(sketch, "E501", {"start": v(8.62, 26.1) * mm, "end": v(8.49, 26.28) * mm});
            skLineSegment(sketch, "E502", {"start": v(9.26, 25.14) * mm, "end": v(6.3, 24.34) * mm});
            skLineSegment(sketch, "E503", {"start": v(6.3, 24.34) * mm, "end": v(6.4, 23.98) * mm});
            skLineSegment(sketch, "E504", {"start": v(6.4, 23.98) * mm, "end": v(9.49, 24.87) * mm});
            skLineSegment(sketch, "E505", {"start": v(9.49, 24.87) * mm, "end": v(9.26, 25.14) * mm});
            skLineSegment(sketch, "E506", {"start": v(0, 28.18) * mm, "end": v(0, 27.76) * mm});
            skLineSegment(sketch, "E507", {"start": v(0, 26.95) * mm, "end": v(0, 26.45) * mm});
            skLineSegment(sketch, "E508", {"start": v(3, 23.3) * mm, "end": v(3.53, 23.3) * mm});
            skLineSegment(sketch, "E509", {"start": v(2.66, 22.89) * mm, "end": v(3.85, 22.89) * mm});
            skArc(sketch, "E510", {"start": v(3.85, 22.89) * mm, "mid": v(3.03, 26.34) * mm, "end": v(0, 28.18) * mm});
            skArc(sketch, "E511", {"start": v(3.53, 23.3) * mm, "mid": v(2.63, 26.21) * mm, "end": v(0, 27.76) * mm});
            skArc(sketch, "E512", {"start": v(3, 23.3) * mm, "mid": v(2.18, 25.69) * mm, "end": v(0, 26.95) * mm});
            skArc(sketch, "E513", {"start": v(2.66, 22.89) * mm, "mid": v(1.92, 25.12) * mm, "end": v(0, 26.45) * mm});
            skLineSegment(sketch, "E514", {"start": v(0, 17.55) * mm, "end": v(0.37, 17.55) * mm});
            skLineSegment(sketch, "E515", {"start": v(0.37, 17.55) * mm, "end": v(0.37, 20.57) * mm});
            skLineSegment(sketch, "E516", {"start": v(0.37, 20.57) * mm, "end": v(0.6, 20.55) * mm});
            skLineSegment(sketch, "E517", {"start": v(0.6, 20.55) * mm, "end": v(0.61, 21.55) * mm});
            skLineSegment(sketch, "E518", {"start": v(0.61, 21.55) * mm, "end": v(1.64, 21.61) * mm});
            skLineSegment(sketch, "E519", {"start": v(1.64, 21.61) * mm, "end": v(1.64, 22.48) * mm});
            skLineSegment(sketch, "E520", {"start": v(1.64, 22.48) * mm, "end": v(0.53, 22.51) * mm});
            skLineSegment(sketch, "E521", {"start": v(0.53, 22.51) * mm, "end": v(0.53, 22.81) * mm});
            skLineSegment(sketch, "E522", {"start": v(0.53, 22.81) * mm, "end": v(1.7, 22.81) * mm});
            skLineSegment(sketch, "E523", {"start": v(1.7, 22.81) * mm, "end": v(1.7, 23.72) * mm});
            skLineSegment(sketch, "E524", {"start": v(1.7, 23.72) * mm, "end": v(1.27, 24.62) * mm});
            skLineSegment(sketch, "E525", {"start": v(1.27, 24.62) * mm, "end": v(0.75, 24.62) * mm});
            skLineSegment(sketch, "E526", {"start": v(0.75, 24.62) * mm, "end": v(0.42, 25.45) * mm});
            skLineSegment(sketch, "E527", {"start": v(0.42, 25.45) * mm, "end": v(0, 25.77) * mm});
            skLineSegment(sketch, "E528", {"start": v(0, 25.77) * mm, "end": v(0, 25.13) * mm});
            skLineSegment(sketch, "E529", {"start": v(0, 25.13) * mm, "end": v(0.2, 24.9) * mm});
            skLineSegment(sketch, "E530", {"start": v(0.2, 24.9) * mm, "end": v(0.4, 24.39) * mm});
            skLineSegment(sketch, "E531", {"start": v(0.4, 24.39) * mm, "end": v(0.86, 24.16) * mm});
            skLineSegment(sketch, "E532", {"start": v(0.86, 24.16) * mm, "end": v(1.21, 23.34) * mm});
            skLineSegment(sketch, "E533", {"start": v(1.21, 23.34) * mm, "end": v(0.24, 23.25) * mm});
            skLineSegment(sketch, "E534", {"start": v(0.24, 23.25) * mm, "end": v(0.24, 22.26) * mm});
            skLineSegment(sketch, "E535", {"start": v(0.24, 22.26) * mm, "end": v(1.41, 22.26) * mm});
            skLineSegment(sketch, "E536", {"start": v(1.41, 22.26) * mm, "end": v(1.44, 21.86) * mm});
            skLineSegment(sketch, "E537", {"start": v(1.44, 21.86) * mm, "end": v(0, 21.86) * mm});
            skLineSegment(sketch, "E538", {"start": v(0, 21.86) * mm, "end": v(0, 17.55) * mm});
            skArc(sketch, "E539", {"start": v(2.87, 21.88) * mm, "mid": v(1.5, 20.03) * mm, "end": v(0.8, 17.82) * mm});
            skLineSegment(sketch, "E540", {"start": v(2.87, 21.88) * mm, "end": v(4.4, 21.88) * mm});
            skArc(sketch, "E541", {"start": v(4.4, 21.88) * mm, "mid": v(3, 20.02) * mm, "end": v(2.14, 17.86) * mm});
            skLineSegment(sketch, "E542", {"start": v(0.8, 17.82) * mm, "end": v(2.14, 17.86) * mm});
            skArc(sketch, "E543", {"start": v(2.95, 21.58) * mm, "mid": v(1.9, 20.05) * mm, "end": v(1.35, 18.28) * mm});
            skLineSegment(sketch, "E544", {"start": v(2.95, 21.58) * mm, "end": v(3.74, 21.58) * mm});
            skArc(sketch, "E545", {"start": v(3.74, 21.58) * mm, "mid": v(2.6, 20.06) * mm, "end": v(1.92, 18.28) * mm});
            skLineSegment(sketch, "E546", {"start": v(1.92, 18.28) * mm, "end": v(1.35, 18.28) * mm});
            skArc(sketch, "E547", {"start": v(6.97, 21.76) * mm, "mid": v(4.18, 20.6) * mm, "end": v(2.74, 17.94) * mm});
            skLineSegment(sketch, "E548", {"start": v(6.97, 21.76) * mm, "end": v(6.97, 20.2) * mm});
            skArc(sketch, "E549", {"start": v(6.95, 20.18) * mm, "mid": v(5.05, 19.52) * mm, "end": v(3.88, 17.89) * mm});
            skLineSegment(sketch, "E550", {"start": v(3.88, 17.89) * mm, "end": v(2.74, 17.94) * mm});
            skArc(sketch, "E551", {"start": v(6.54, 21.32) * mm, "mid": v(4.42, 20.3) * mm, "end": v(3.11, 18.36) * mm});
            skLineSegment(sketch, "E552", {"start": v(3.11, 18.36) * mm, "end": v(3.78, 18.36) * mm});
            skArc(sketch, "E553", {"start": v(6.5, 20.58) * mm, "mid": v(4.83, 19.84) * mm, "end": v(3.78, 18.36) * mm});
            skLineSegment(sketch, "E554", {"start": v(6.54, 21.32) * mm, "end": v(6.5, 20.58) * mm});
            skLineSegment(sketch, "E555", {"start": v(7.37, 16.14) * mm, "end": v(7.76, 15.39) * mm});
            skLineSegment(sketch, "E556", {"start": v(7.76, 15.39) * mm, "end": v(10.61, 17.1) * mm});
            skLineSegment(sketch, "E557", {"start": v(10.61, 17.1) * mm, "end": v(10.76, 15.8) * mm});
            skLineSegment(sketch, "E558", {"start": v(10.76, 15.8) * mm, "end": v(12.71, 17.66) * mm});
            skLineSegment(sketch, "E559", {"start": v(12.71, 17.66) * mm, "end": v(11.3, 19.89) * mm});
            skLineSegment(sketch, "E560", {"start": v(11.3, 19.89) * mm, "end": v(7.37, 16.14) * mm});
            skLineSegment(sketch, "E561", {"start": v(8.02, 16.37) * mm, "end": v(8.23, 16.14) * mm});
            skLineSegment(sketch, "E562", {"start": v(8.23, 16.14) * mm, "end": v(10.85, 17.64) * mm});
            skLineSegment(sketch, "E563", {"start": v(10.85, 17.64) * mm, "end": v(11, 16.59) * mm});
            skLineSegment(sketch, "E564", {"start": v(11, 16.59) * mm, "end": v(12.22, 17.7) * mm});
            skLineSegment(sketch, "E565", {"start": v(12.22, 17.7) * mm, "end": v(11.34, 19.2) * mm});
            skLineSegment(sketch, "E566", {"start": v(11.34, 19.2) * mm, "end": v(8.02, 16.37) * mm});
            skSolve(sketch);
        }
        {
            var Q0;
            Q0=makeQuery(id+"F26.imprint","IMPRINT",FACE,{"disambiguationData":[TD([[makeQuery(id+"F26.imprint","IMPRINT",EDGE,{"derivedFrom":sQuery(id+"F26.wireOp",EDGE,"E387")}),-1.0]])]});
            var Q1;
            Q1=makeQuery(id+"F26.imprint","IMPRINT",FACE,{"disambiguationData":[TD([[makeQuery(id+"F26.imprint","IMPRINT",EDGE,{"derivedFrom":sQuery(id+"F26.wireOp",EDGE,"E506")}),1.0]])]});
            var Q2;
            Q2=makeQuery(id+"F26.imprint","IMPRINT",FACE,{"disambiguationData":[TD([[makeQuery(id+"F26.imprint","IMPRINT",EDGE,{"derivedFrom":sQuery(id+"F26.wireOp",EDGE,"E514")}),1.0]])]});
            var Q3;
            Q3=makeQuery(id+"F26.imprint","IMPRINT",FACE,{"disambiguationData":[TD([[makeQuery(id+"F26.imprint","IMPRINT",EDGE,{"derivedFrom":sQuery(id+"F26.wireOp",EDGE,"E209")}),-1.0]])]});
            var Q4;
            Q4=makeQuery(id+"F26.imprint","IMPRINT",FACE,{"disambiguationData":[TD([[makeQuery(id+"F26.imprint","IMPRINT",EDGE,{"derivedFrom":sQuery(id+"F26.wireOp",EDGE,"E217")}),1.0]])]});
            var Q5;
            Q5=makeQuery(id+"F26.imprint","IMPRINT",FACE,{"disambiguationData":[TD([[makeQuery(id+"F26.imprint","IMPRINT",EDGE,{"derivedFrom":sQuery(id+"F26.wireOp",EDGE,"E395")}),-1.0]])]});
            var Q6;
            Q6=makeQuery(id+"F26.imprint","IMPRINT",FACE,{"disambiguationData":[TD([[makeQuery(id+"F26.imprint","IMPRINT",EDGE,{"derivedFrom":sQuery(id+"F26.wireOp",EDGE,"E539")}),1.0]])]});
            var Q7;
            Q7=makeQuery(id+"F26.imprint","IMPRINT",FACE,{"disambiguationData":[TD([[makeQuery(id+"F26.imprint","IMPRINT",EDGE,{"derivedFrom":sQuery(id+"F26.wireOp",EDGE,"E312")}),1.0]])]});
            var Q8;
            Q8=makeQuery(id+"F26.imprint","IMPRINT",FACE,{"disambiguationData":[TD([[makeQuery(id+"F26.imprint","IMPRINT",EDGE,{"derivedFrom":sQuery(id+"F26.wireOp",EDGE,"E92")}),-1.0]])]});
            var Q9;
            Q9=makeQuery(id+"F26.imprint","IMPRINT",FACE,{"disambiguationData":[TD([[makeQuery(id+"F26.imprint","IMPRINT",EDGE,{"derivedFrom":sQuery(id+"F26.wireOp",EDGE,"E555")}),1.0]])]});
            var Q10;
            Q10=makeQuery(id+"F26.imprint","IMPRINT",FACE,{"disambiguationData":[TD([[makeQuery(id+"F26.imprint","IMPRINT",EDGE,{"derivedFrom":sQuery(id+"F26.wireOp",EDGE,"E423.bottom")}),-1.0]])]});
            var Q11;
            Q11=makeQuery(id+"F26.imprint","IMPRINT",FACE,{"disambiguationData":[TD([[makeQuery(id+"F26.imprint","IMPRINT",EDGE,{"derivedFrom":sQuery(id+"F26.wireOp",EDGE,"E419.bottom")}),-1.0]])]});
            var Q12;
            Q12=makeQuery(id+"F26.imprint","IMPRINT",FACE,{"disambiguationData":[TD([[makeQuery(id+"F26.imprint","IMPRINT",EDGE,{"derivedFrom":sQuery(id+"F26.wireOp",EDGE,"E422.bottom")}),-1.0]])]});
            var Q13;
            Q13=makeQuery(id+"F26.imprint","IMPRINT",FACE,{"disambiguationData":[TD([[makeQuery(id+"F26.imprint","IMPRINT",EDGE,{"derivedFrom":sQuery(id+"F26.wireOp",EDGE,"E421.bottom")}),-1.0]])]});
            var Q14;
            Q14=makeQuery(id+"F26.imprint","IMPRINT",FACE,{"disambiguationData":[TD([[makeQuery(id+"F26.imprint","IMPRINT",EDGE,{"derivedFrom":sQuery(id+"F26.wireOp",EDGE,"E420.bottom")}),-1.0]])]});
            var Q15;
            Q15=makeQuery(id+"F26.imprint","IMPRINT",FACE,{"disambiguationData":[TD([[makeQuery(id+"F26.imprint","IMPRINT",EDGE,{"derivedFrom":sQuery(id+"F26.wireOp",EDGE,"E551")}),1.0]])]});
            var Q16;
            Q16=makeQuery(id+"F26.imprint","IMPRINT",FACE,{"disambiguationData":[TD([[makeQuery(id+"F26.imprint","IMPRINT",EDGE,{"derivedFrom":sQuery(id+"F26.wireOp",EDGE,"E375")}),-1.0]])]});
            var Q17;
            Q17=makeQuery(id+"F26.imprint","IMPRINT",FACE,{"disambiguationData":[TD([[makeQuery(id+"F26.imprint","IMPRINT",EDGE,{"derivedFrom":sQuery(id+"F26.wireOp",EDGE,"E202")}),1.0]])]});
            extrude(context, id + "F27", {"entities" : qUnion([Q0, Q1, Q2, Q3, Q4, Q5, Q6, Q7, Q8, Q9, Q10, Q11, Q12, Q13, Q14, Q15, Q16, Q17]), "depth" : 1 * mm, "offsetDistance" : 25 * mm, "hasSecondDirection" : true, "secondDirectionOppositeDirection" : true, "secondDirectionDepth" : 15 * mm});
        }
        {
            var Q0;
            Q0=makeQuery(id+"F27.opExtrude","CAP_FACE",FACE,{"disambiguationData":[OSD([sQuery(id+"F26.wireOp",EDGE,"E92"),sQuery(id+"F26.wireOp",EDGE,"E93"),sQuery(id+"F26.wireOp",EDGE,"E94"),sQuery(id+"F26.wireOp",EDGE,"E95"),sQuery(id+"F26.wireOp",EDGE,"E96"),sQuery(id+"F26.wireOp",EDGE,"E97"),sQuery(id+"F26.wireOp",EDGE,"E98"),sQuery(id+"F26.wireOp",EDGE,"E99"),sQuery(id+"F26.wireOp",EDGE,"E100"),sQuery(id+"F26.wireOp",EDGE,"E101"),sQuery(id+"F26.wireOp",EDGE,"E102"),sQuery(id+"F26.wireOp",EDGE,"E103"),sQuery(id+"F26.wireOp",EDGE,"E104"),sQuery(id+"F26.wireOp",EDGE,"E105"),sQuery(id+"F26.wireOp",EDGE,"E106"),sQuery(id+"F26.wireOp",EDGE,"E107"),sQuery(id+"F26.wireOp",EDGE,"E108.trimOffspring"),sQuery(id+"F26.wireOp",EDGE,"E109.trimOffspring"),sQuery(id+"F26.wireOp",EDGE,"E110.trimOffspring"),sQuery(id+"F26.wireOp",EDGE,"E111.trimOffspring"),sQuery(id+"F26.wireOp",EDGE,"E112.trimOffspring"),sQuery(id+"F26.wireOp",EDGE,"E113.trimOffspring"),sQuery(id+"F26.wireOp",EDGE,"E114.trimOffspring"),sQuery(id+"F26.wireOp",EDGE,"E115.trimOffspring"),sQuery(id+"F26.wireOp",EDGE,"E116.trimOffspring"),sQuery(id+"F26.wireOp",EDGE,"E117"),sQuery(id+"F26.wireOp",EDGE,"E118"),sQuery(id+"F26.wireOp",EDGE,"E119"),sQuery(id+"F26.wireOp",EDGE,"E120"),sQuery(id+"F26.wireOp",EDGE,"E121"),sQuery(id+"F26.wireOp",EDGE,"E122"),sQuery(id+"F26.wireOp",EDGE,"E123"),sQuery(id+"F26.wireOp",EDGE,"E124"),sQuery(id+"F26.wireOp",EDGE,"E125"),sQuery(id+"F26.wireOp",EDGE,"E126"),sQuery(id+"F26.wireOp",EDGE,"E127"),sQuery(id+"F26.wireOp",EDGE,"E128"),sQuery(id+"F26.wireOp",EDGE,"E129"),sQuery(id+"F26.wireOp",EDGE,"E130"),sQuery(id+"F26.wireOp",EDGE,"E131"),sQuery(id+"F26.wireOp",EDGE,"E132"),sQuery(id+"F26.wireOp",EDGE,"E133"),sQuery(id+"F26.wireOp",EDGE,"E134"),sQuery(id+"F26.wireOp",EDGE,"E135"),sQuery(id+"F26.wireOp",EDGE,"E136"),sQuery(id+"F26.wireOp",EDGE,"E137"),sQuery(id+"F26.wireOp",EDGE,"E138"),sQuery(id+"F26.wireOp",EDGE,"E139"),sQuery(id+"F26.wireOp",EDGE,"E140"),sQuery(id+"F26.wireOp",EDGE,"E141"),sQuery(id+"F26.wireOp",EDGE,"E142"),sQuery(id+"F26.wireOp",EDGE,"E143"),sQuery(id+"F26.wireOp",EDGE,"E144"),sQuery(id+"F26.wireOp",EDGE,"E145"),sQuery(id+"F26.wireOp",EDGE,"E146"),sQuery(id+"F26.wireOp",EDGE,"E147"),sQuery(id+"F26.wireOp",EDGE,"E148"),sQuery(id+"F26.wireOp",EDGE,"E149"),sQuery(id+"F26.wireOp",EDGE,"E150"),sQuery(id+"F26.wireOp",EDGE,"E151"),sQuery(id+"F26.wireOp",EDGE,"E152"),sQuery(id+"F26.wireOp",EDGE,"E153"),sQuery(id+"F26.wireOp",EDGE,"E154"),sQuery(id+"F26.wireOp",EDGE,"E155"),sQuery(id+"F26.wireOp",EDGE,"E156"),sQuery(id+"F26.wireOp",EDGE,"E157.trimOffspring"),sQuery(id+"F26.wireOp",EDGE,"E158"),sQuery(id+"F26.wireOp",EDGE,"E159"),sQuery(id+"F26.wireOp",EDGE,"E160"),sQuery(id+"F26.wireOp",EDGE,"E161"),sQuery(id+"F26.wireOp",EDGE,"E162"),sQuery(id+"F26.wireOp",EDGE,"E163"),sQuery(id+"F26.wireOp",EDGE,"E164"),sQuery(id+"F26.wireOp",EDGE,"E165"),sQuery(id+"F26.wireOp",EDGE,"E166"),sQuery(id+"F26.wireOp",EDGE,"E167"),sQuery(id+"F26.wireOp",EDGE,"E168"),sQuery(id+"F26.wireOp",EDGE,"E169"),sQuery(id+"F26.wireOp",EDGE,"E170"),sQuery(id+"F26.wireOp",EDGE,"E171"),sQuery(id+"F26.wireOp",EDGE,"E172"),sQuery(id+"F26.wireOp",EDGE,"E173"),sQuery(id+"F26.wireOp",EDGE,"E174"),sQuery(id+"F26.wireOp",EDGE,"E175"),sQuery(id+"F26.wireOp",EDGE,"E176"),sQuery(id+"F26.wireOp",EDGE,"E177"),sQuery(id+"F26.wireOp",EDGE,"E178"),sQuery(id+"F26.wireOp",EDGE,"E179"),sQuery(id+"F26.wireOp",EDGE,"E180"),sQuery(id+"F26.wireOp",EDGE,"E181"),sQuery(id+"F26.wireOp",EDGE,"E182"),sQuery(id+"F26.wireOp",EDGE,"E183"),sQuery(id+"F26.wireOp",EDGE,"E184"),sQuery(id+"F26.wireOp",EDGE,"E185"),sQuery(id+"F26.wireOp",EDGE,"E186"),sQuery(id+"F26.wireOp",EDGE,"E187"),sQuery(id+"F26.wireOp",EDGE,"E188.trimOffspring"),sQuery(id+"F26.wireOp",EDGE,"E189.trimOffspring"),sQuery(id+"F26.wireOp",EDGE,"E190"),sQuery(id+"F26.wireOp",EDGE,"E191"),sQuery(id+"F26.wireOp",EDGE,"E192"),sQuery(id+"F26.wireOp",EDGE,"E193"),sQuery(id+"F26.wireOp",EDGE,"E198"),sQuery(id+"F26.wireOp",EDGE,"E199"),sQuery(id+"F26.wireOp",EDGE,"E200"),sQuery(id+"F26.wireOp",EDGE,"E201"),sQuery(id+"F26.wireOp",EDGE,"E225"),sQuery(id+"F26.wireOp",EDGE,"E226"),sQuery(id+"F26.wireOp",EDGE,"E227"),sQuery(id+"F26.wireOp",EDGE,"E228"),sQuery(id+"F26.wireOp",EDGE,"E229"),sQuery(id+"F26.wireOp",EDGE,"E230"),sQuery(id+"F26.wireOp",EDGE,"E231"),sQuery(id+"F26.wireOp",EDGE,"E232"),sQuery(id+"F26.wireOp",EDGE,"E233"),sQuery(id+"F26.wireOp",EDGE,"E234"),sQuery(id+"F26.wireOp",EDGE,"E235"),sQuery(id+"F26.wireOp",EDGE,"E236"),sQuery(id+"F26.wireOp",EDGE,"E237"),sQuery(id+"F26.wireOp",EDGE,"E238"),sQuery(id+"F26.wireOp",EDGE,"E239"),sQuery(id+"F26.wireOp",EDGE,"E240"),sQuery(id+"F26.wireOp",EDGE,"E241"),sQuery(id+"F26.wireOp",EDGE,"E242"),sQuery(id+"F26.wireOp",EDGE,"E243"),sQuery(id+"F26.wireOp",EDGE,"E244"),sQuery(id+"F26.wireOp",EDGE,"E245"),sQuery(id+"F26.wireOp",EDGE,"E246"),sQuery(id+"F26.wireOp",EDGE,"E247"),sQuery(id+"F26.wireOp",EDGE,"E248"),sQuery(id+"F26.wireOp",EDGE,"E249"),sQuery(id+"F26.wireOp",EDGE,"E250"),sQuery(id+"F26.wireOp",EDGE,"E251"),sQuery(id+"F26.wireOp",EDGE,"E252"),sQuery(id+"F26.wireOp",EDGE,"E253"),sQuery(id+"F26.wireOp",EDGE,"E254"),sQuery(id+"F26.wireOp",EDGE,"E255"),sQuery(id+"F26.wireOp",EDGE,"E256"),sQuery(id+"F26.wireOp",EDGE,"E257"),sQuery(id+"F26.wireOp",EDGE,"E258"),sQuery(id+"F26.wireOp",EDGE,"E259"),sQuery(id+"F26.wireOp",EDGE,"E260"),sQuery(id+"F26.wireOp",EDGE,"E261"),sQuery(id+"F26.wireOp",EDGE,"E262"),sQuery(id+"F26.wireOp",EDGE,"E263"),sQuery(id+"F26.wireOp",EDGE,"E264"),sQuery(id+"F26.wireOp",EDGE,"E265"),sQuery(id+"F26.wireOp",EDGE,"E266"),sQuery(id+"F26.wireOp",EDGE,"E267"),sQuery(id+"F26.wireOp",EDGE,"E268"),sQuery(id+"F26.wireOp",EDGE,"E269"),sQuery(id+"F26.wireOp",EDGE,"E270"),sQuery(id+"F26.wireOp",EDGE,"E271"),sQuery(id+"F26.wireOp",EDGE,"E272"),sQuery(id+"F26.wireOp",EDGE,"E273"),sQuery(id+"F26.wireOp",EDGE,"E274"),sQuery(id+"F26.wireOp",EDGE,"E275"),sQuery(id+"F26.wireOp",EDGE,"E276"),sQuery(id+"F26.wireOp",EDGE,"E277"),sQuery(id+"F26.wireOp",EDGE,"E278"),sQuery(id+"F26.wireOp",EDGE,"E279"),sQuery(id+"F26.wireOp",EDGE,"E280"),sQuery(id+"F26.wireOp",EDGE,"E281"),sQuery(id+"F26.wireOp",EDGE,"E282"),sQuery(id+"F26.wireOp",EDGE,"E283"),sQuery(id+"F26.wireOp",EDGE,"E284"),sQuery(id+"F26.wireOp",EDGE,"E285"),sQuery(id+"F26.wireOp",EDGE,"E286"),sQuery(id+"F26.wireOp",EDGE,"E287"),sQuery(id+"F26.wireOp",EDGE,"E288"),sQuery(id+"F26.wireOp",EDGE,"E289.trimOffspring"),sQuery(id+"F26.wireOp",EDGE,"E291"),sQuery(id+"F26.wireOp",EDGE,"E292"),sQuery(id+"F26.wireOp",EDGE,"E293"),sQuery(id+"F26.wireOp",EDGE,"E294"),sQuery(id+"F26.wireOp",EDGE,"E295"),sQuery(id+"F26.wireOp",EDGE,"E296"),sQuery(id+"F26.wireOp",EDGE,"E297"),sQuery(id+"F26.wireOp",EDGE,"E298"),sQuery(id+"F26.wireOp",EDGE,"E299"),sQuery(id+"F26.wireOp",EDGE,"E300"),sQuery(id+"F26.wireOp",EDGE,"E301"),sQuery(id+"F26.wireOp",EDGE,"E302"),sQuery(id+"F26.wireOp",EDGE,"E303"),sQuery(id+"F26.wireOp",EDGE,"E304"),sQuery(id+"F26.wireOp",EDGE,"E305"),sQuery(id+"F26.wireOp",EDGE,"E306"),sQuery(id+"F26.wireOp",EDGE,"E307"),sQuery(id+"F26.wireOp",EDGE,"E308"),sQuery(id+"F26.wireOp",EDGE,"E309"),sQuery(id+"F26.wireOp",EDGE,"E310"),sQuery(id+"F26.wireOp",EDGE,"E311"),sQuery(id+"F26.wireOp",EDGE,"E424"),sQuery(id+"F26.wireOp",EDGE,"E425"),sQuery(id+"F26.wireOp",EDGE,"E426"),sQuery(id+"F26.wireOp",EDGE,"E427"),sQuery(id+"F26.wireOp",EDGE,"E428"),sQuery(id+"F26.wireOp",EDGE,"E429"),sQuery(id+"F26.wireOp",EDGE,"E430"),sQuery(id+"F26.wireOp",EDGE,"E431"),sQuery(id+"F26.wireOp",EDGE,"E432"),sQuery(id+"F26.wireOp",EDGE,"E433"),sQuery(id+"F26.wireOp",EDGE,"E434"),sQuery(id+"F26.wireOp",EDGE,"E435"),sQuery(id+"F26.wireOp",EDGE,"E436"),sQuery(id+"F26.wireOp",EDGE,"E437"),sQuery(id+"F26.wireOp",EDGE,"E438"),sQuery(id+"F26.wireOp",EDGE,"E439"),sQuery(id+"F26.wireOp",EDGE,"E440"),sQuery(id+"F26.wireOp",EDGE,"E441"),sQuery(id+"F26.wireOp",EDGE,"E442"),sQuery(id+"F26.wireOp",EDGE,"E443"),sQuery(id+"F26.wireOp",EDGE,"E444"),sQuery(id+"F26.wireOp",EDGE,"E445"),sQuery(id+"F26.wireOp",EDGE,"E446"),sQuery(id+"F26.wireOp",EDGE,"E447"),sQuery(id+"F26.wireOp",EDGE,"E448"),sQuery(id+"F26.wireOp",EDGE,"E449"),sQuery(id+"F26.wireOp",EDGE,"E450"),sQuery(id+"F26.wireOp",EDGE,"E451"),sQuery(id+"F26.wireOp",EDGE,"E452"),sQuery(id+"F26.wireOp",EDGE,"E453"),sQuery(id+"F26.wireOp",EDGE,"E454"),sQuery(id+"F26.wireOp",EDGE,"E455"),sQuery(id+"F26.wireOp",EDGE,"E456"),sQuery(id+"F26.wireOp",EDGE,"E457"),sQuery(id+"F26.wireOp",EDGE,"E458"),sQuery(id+"F26.wireOp",EDGE,"E459"),sQuery(id+"F26.wireOp",EDGE,"E460"),sQuery(id+"F26.wireOp",EDGE,"E461"),sQuery(id+"F26.wireOp",EDGE,"E462"),sQuery(id+"F26.wireOp",EDGE,"E463"),sQuery(id+"F26.wireOp",EDGE,"E464"),sQuery(id+"F26.wireOp",EDGE,"E465"),sQuery(id+"F26.wireOp",EDGE,"E466"),sQuery(id+"F26.wireOp",EDGE,"E467"),sQuery(id+"F26.wireOp",EDGE,"E468"),sQuery(id+"F26.wireOp",EDGE,"E469"),sQuery(id+"F26.wireOp",EDGE,"E470"),sQuery(id+"F26.wireOp",EDGE,"E471"),sQuery(id+"F26.wireOp",EDGE,"E472"),sQuery(id+"F26.wireOp",EDGE,"E473"),sQuery(id+"F26.wireOp",EDGE,"E474"),sQuery(id+"F26.wireOp",EDGE,"E475"),sQuery(id+"F26.wireOp",EDGE,"E476"),sQuery(id+"F26.wireOp",EDGE,"E477"),sQuery(id+"F26.wireOp",EDGE,"E478"),sQuery(id+"F26.wireOp",EDGE,"E479"),sQuery(id+"F26.wireOp",EDGE,"E480"),sQuery(id+"F26.wireOp",EDGE,"E481"),sQuery(id+"F26.wireOp",EDGE,"E482"),sQuery(id+"F26.wireOp",EDGE,"E483"),sQuery(id+"F26.wireOp",EDGE,"E484"),sQuery(id+"F26.wireOp",EDGE,"E485"),sQuery(id+"F26.wireOp",EDGE,"E486"),sQuery(id+"F26.wireOp",EDGE,"E487"),sQuery(id+"F26.wireOp",EDGE,"E488"),sQuery(id+"F26.wireOp",EDGE,"E489"),sQuery(id+"F26.wireOp",EDGE,"E490"),sQuery(id+"F26.wireOp",EDGE,"E491"),sQuery(id+"F26.wireOp",EDGE,"E492"),sQuery(id+"F26.wireOp",EDGE,"E493"),sQuery(id+"F26.wireOp",EDGE,"E494"),sQuery(id+"F26.wireOp",EDGE,"E495"),sQuery(id+"F26.wireOp",EDGE,"E496"),sQuery(id+"F26.wireOp",EDGE,"E497"),sQuery(id+"F26.wireOp",EDGE,"E498"),sQuery(id+"F26.wireOp",EDGE,"E499"),sQuery(id+"F26.wireOp",EDGE,"E500"),sQuery(id+"F26.wireOp",EDGE,"E501"),sQuery(id+"F26.wireOp",EDGE,"E502"),sQuery(id+"F26.wireOp",EDGE,"E503"),sQuery(id+"F26.wireOp",EDGE,"E504"),sQuery(id+"F26.wireOp",EDGE,"E505")])],"isStart":true});
            var sketch = newSketch(context, id + "F28", { "sketchPlane" : qUnion([Q0])});
            skLineSegment(sketch, "E567", {"start": v(-5.23, 27.4) * mm, "end": v(-0.95, 24.2) * mm});
            skLineSegment(sketch, "E568", {"start": v(-1.32, 23.84) * mm, "end": v(-5.23, 26.84) * mm});
            skLineSegment(sketch, "E569", {"start": v(-5.23, 26.84) * mm, "end": v(-5.16, 27.55) * mm});
            skLineSegment(sketch, "E570", {"start": v(-4.93, 20.32) * mm, "end": v(-0.53, 21.43) * mm});
            skLineSegment(sketch, "E571", {"start": v(-0.53, 21.43) * mm, "end": v(-1.32, 23.84) * mm});
            skLineSegment(sketch, "E572", {"start": v(-0.95, 24.2) * mm, "end": v(0, 21.43) * mm});
            skLineSegment(sketch, "E573", {"start": v(0, 21.43) * mm, "end": v(-4.34, 19.94) * mm});
            skLineSegment(sketch, "E574", {"start": v(-4.34, 19.94) * mm, "end": v(-0.53, 15.36) * mm});
            skLineSegment(sketch, "E575", {"start": v(-0.53, 15.36) * mm, "end": v(-3.98, 16.8) * mm});
            skLineSegment(sketch, "E576", {"start": v(-3.98, 16.8) * mm, "end": v(-4.66, 19.76) * mm});
            skLineSegment(sketch, "E577", {"start": v(-4.66, 19.76) * mm, "end": v(-10.32, 13.6) * mm});
            skLineSegment(sketch, "E578", {"start": v(-10.32, 13.6) * mm, "end": v(-14.27, 13.6) * mm});
            skLineSegment(sketch, "E579", {"start": v(-14.27, 13.6) * mm, "end": v(-13, 8) * mm});
            skLineSegment(sketch, "E580", {"start": v(-13, 8) * mm, "end": v(-13, 1.17) * mm});
            skLineSegment(sketch, "E581", {"start": v(-13, 1.17) * mm, "end": v(-6.9, -8.05) * mm});
            skLineSegment(sketch, "E582", {"start": v(-6.9, -8.05) * mm, "end": v(-7.4, -8.56) * mm});
            skLineSegment(sketch, "E583", {"start": v(-7.4, -8.56) * mm, "end": v(-13.26, 0) * mm});
            skLineSegment(sketch, "E584", {"start": v(-13.26, 0) * mm, "end": v(-16.62, -1.93) * mm});
            skLineSegment(sketch, "E585", {"start": v(-16.62, -1.93) * mm, "end": v(-17.29, 0) * mm});
            skLineSegment(sketch, "E586", {"start": v(-17.29, 0) * mm, "end": v(-13.6, 0.37) * mm});
            skLineSegment(sketch, "E587", {"start": v(-13.6, 0.37) * mm, "end": v(-13.54, 7.9) * mm});
            skLineSegment(sketch, "E588", {"start": v(-13.54, 7.9) * mm, "end": v(-14.75, 14.03) * mm});
            skLineSegment(sketch, "E589", {"start": v(-14.75, 14.03) * mm, "end": v(-13.57, 15.3) * mm});
            skLineSegment(sketch, "E590", {"start": v(-13.57, 15.3) * mm, "end": v(-10.06, 13.89) * mm});
            skLineSegment(sketch, "E591", {"start": v(-10.06, 13.89) * mm, "end": v(-4.93, 20.32) * mm});
            skSolve(sketch);
        }
        {
            var Q0;
            Q0 = qSketchRegion(id + "F28", true);
            extrude(context, id + "F29", {"entities" : qUnion([Q0]), "operationType" : NewBodyOperationType.ADD, "oppositeDirection" : true, "depth" : 2 * mm, "offsetDistance" : 25 * mm});
        }
        {
            var Q0;
            {var subQ0=sQuery(id+"F28.wireOp",EDGE,"E577");Q0=makeQuery(id+"F29.boolean.opBoolean","MERGE",FACE,{"derivedFrom":[makeQuery(id+"F27.opExtrude","CAP_FACE",FACE,{"disambiguationData":[OSD([sQuery(id+"F26.wireOp",EDGE,"E92"),sQuery(id+"F26.wireOp",EDGE,"E93"),sQuery(id+"F26.wireOp",EDGE,"E94"),sQuery(id+"F26.wireOp",EDGE,"E95"),sQuery(id+"F26.wireOp",EDGE,"E96"),sQuery(id+"F26.wireOp",EDGE,"E97"),sQuery(id+"F26.wireOp",EDGE,"E98"),sQuery(id+"F26.wireOp",EDGE,"E99"),sQuery(id+"F26.wireOp",EDGE,"E100"),sQuery(id+"F26.wireOp",EDGE,"E101"),sQuery(id+"F26.wireOp",EDGE,"E102"),sQuery(id+"F26.wireOp",EDGE,"E103"),sQuery(id+"F26.wireOp",EDGE,"E104"),sQuery(id+"F26.wireOp",EDGE,"E105"),sQuery(id+"F26.wireOp",EDGE,"E106"),sQuery(id+"F26.wireOp",EDGE,"E107"),sQuery(id+"F26.wireOp",EDGE,"E108.trimOffspring"),sQuery(id+"F26.wireOp",EDGE,"E109.trimOffspring"),sQuery(id+"F26.wireOp",EDGE,"E110.trimOffspring"),sQuery(id+"F26.wireOp",EDGE,"E111.trimOffspring"),sQuery(id+"F26.wireOp",EDGE,"E112.trimOffspring"),sQuery(id+"F26.wireOp",EDGE,"E113.trimOffspring"),sQuery(id+"F26.wireOp",EDGE,"E114.trimOffspring"),sQuery(id+"F26.wireOp",EDGE,"E115.trimOffspring"),sQuery(id+"F26.wireOp",EDGE,"E116.trimOffspring"),sQuery(id+"F26.wireOp",EDGE,"E117"),sQuery(id+"F26.wireOp",EDGE,"E118"),sQuery(id+"F26.wireOp",EDGE,"E119"),sQuery(id+"F26.wireOp",EDGE,"E120"),sQuery(id+"F26.wireOp",EDGE,"E121"),sQuery(id+"F26.wireOp",EDGE,"E122"),sQuery(id+"F26.wireOp",EDGE,"E123"),sQuery(id+"F26.wireOp",EDGE,"E124"),sQuery(id+"F26.wireOp",EDGE,"E125"),sQuery(id+"F26.wireOp",EDGE,"E126"),sQuery(id+"F26.wireOp",EDGE,"E127"),sQuery(id+"F26.wireOp",EDGE,"E128"),sQuery(id+"F26.wireOp",EDGE,"E129"),sQuery(id+"F26.wireOp",EDGE,"E130"),sQuery(id+"F26.wireOp",EDGE,"E131"),sQuery(id+"F26.wireOp",EDGE,"E132"),sQuery(id+"F26.wireOp",EDGE,"E133"),sQuery(id+"F26.wireOp",EDGE,"E134"),sQuery(id+"F26.wireOp",EDGE,"E135"),sQuery(id+"F26.wireOp",EDGE,"E136"),sQuery(id+"F26.wireOp",EDGE,"E137"),sQuery(id+"F26.wireOp",EDGE,"E138"),sQuery(id+"F26.wireOp",EDGE,"E139"),sQuery(id+"F26.wireOp",EDGE,"E140"),sQuery(id+"F26.wireOp",EDGE,"E141"),sQuery(id+"F26.wireOp",EDGE,"E142"),sQuery(id+"F26.wireOp",EDGE,"E143"),sQuery(id+"F26.wireOp",EDGE,"E144"),sQuery(id+"F26.wireOp",EDGE,"E145"),sQuery(id+"F26.wireOp",EDGE,"E146"),sQuery(id+"F26.wireOp",EDGE,"E147"),sQuery(id+"F26.wireOp",EDGE,"E148"),sQuery(id+"F26.wireOp",EDGE,"E149"),sQuery(id+"F26.wireOp",EDGE,"E150"),sQuery(id+"F26.wireOp",EDGE,"E151"),sQuery(id+"F26.wireOp",EDGE,"E152"),sQuery(id+"F26.wireOp",EDGE,"E153"),sQuery(id+"F26.wireOp",EDGE,"E154"),sQuery(id+"F26.wireOp",EDGE,"E155"),sQuery(id+"F26.wireOp",EDGE,"E156"),sQuery(id+"F26.wireOp",EDGE,"E157.trimOffspring"),sQuery(id+"F26.wireOp",EDGE,"E158"),sQuery(id+"F26.wireOp",EDGE,"E159"),sQuery(id+"F26.wireOp",EDGE,"E160"),sQuery(id+"F26.wireOp",EDGE,"E161"),sQuery(id+"F26.wireOp",EDGE,"E162"),sQuery(id+"F26.wireOp",EDGE,"E163"),sQuery(id+"F26.wireOp",EDGE,"E164"),sQuery(id+"F26.wireOp",EDGE,"E165"),sQuery(id+"F26.wireOp",EDGE,"E166"),sQuery(id+"F26.wireOp",EDGE,"E167"),sQuery(id+"F26.wireOp",EDGE,"E168"),sQuery(id+"F26.wireOp",EDGE,"E169"),sQuery(id+"F26.wireOp",EDGE,"E170"),sQuery(id+"F26.wireOp",EDGE,"E171"),sQuery(id+"F26.wireOp",EDGE,"E172"),sQuery(id+"F26.wireOp",EDGE,"E173"),sQuery(id+"F26.wireOp",EDGE,"E174"),sQuery(id+"F26.wireOp",EDGE,"E175"),sQuery(id+"F26.wireOp",EDGE,"E176"),sQuery(id+"F26.wireOp",EDGE,"E177"),sQuery(id+"F26.wireOp",EDGE,"E178"),sQuery(id+"F26.wireOp",EDGE,"E179"),sQuery(id+"F26.wireOp",EDGE,"E180"),sQuery(id+"F26.wireOp",EDGE,"E181"),sQuery(id+"F26.wireOp",EDGE,"E182"),sQuery(id+"F26.wireOp",EDGE,"E183"),sQuery(id+"F26.wireOp",EDGE,"E184"),sQuery(id+"F26.wireOp",EDGE,"E185"),sQuery(id+"F26.wireOp",EDGE,"E186"),sQuery(id+"F26.wireOp",EDGE,"E187"),sQuery(id+"F26.wireOp",EDGE,"E188.trimOffspring"),sQuery(id+"F26.wireOp",EDGE,"E189.trimOffspring"),sQuery(id+"F26.wireOp",EDGE,"E190"),sQuery(id+"F26.wireOp",EDGE,"E191"),sQuery(id+"F26.wireOp",EDGE,"E192"),sQuery(id+"F26.wireOp",EDGE,"E193"),sQuery(id+"F26.wireOp",EDGE,"E198"),sQuery(id+"F26.wireOp",EDGE,"E199"),sQuery(id+"F26.wireOp",EDGE,"E200"),sQuery(id+"F26.wireOp",EDGE,"E201"),sQuery(id+"F26.wireOp",EDGE,"E225"),sQuery(id+"F26.wireOp",EDGE,"E226"),sQuery(id+"F26.wireOp",EDGE,"E227"),sQuery(id+"F26.wireOp",EDGE,"E228"),sQuery(id+"F26.wireOp",EDGE,"E229"),sQuery(id+"F26.wireOp",EDGE,"E230"),sQuery(id+"F26.wireOp",EDGE,"E231"),sQuery(id+"F26.wireOp",EDGE,"E232"),sQuery(id+"F26.wireOp",EDGE,"E233"),sQuery(id+"F26.wireOp",EDGE,"E234"),sQuery(id+"F26.wireOp",EDGE,"E235"),sQuery(id+"F26.wireOp",EDGE,"E236"),sQuery(id+"F26.wireOp",EDGE,"E237"),sQuery(id+"F26.wireOp",EDGE,"E238"),sQuery(id+"F26.wireOp",EDGE,"E239"),sQuery(id+"F26.wireOp",EDGE,"E240"),sQuery(id+"F26.wireOp",EDGE,"E241"),sQuery(id+"F26.wireOp",EDGE,"E242"),sQuery(id+"F26.wireOp",EDGE,"E243"),sQuery(id+"F26.wireOp",EDGE,"E244"),sQuery(id+"F26.wireOp",EDGE,"E245"),sQuery(id+"F26.wireOp",EDGE,"E246"),sQuery(id+"F26.wireOp",EDGE,"E247"),sQuery(id+"F26.wireOp",EDGE,"E248"),sQuery(id+"F26.wireOp",EDGE,"E249"),sQuery(id+"F26.wireOp",EDGE,"E250"),sQuery(id+"F26.wireOp",EDGE,"E251"),sQuery(id+"F26.wireOp",EDGE,"E252"),sQuery(id+"F26.wireOp",EDGE,"E253"),sQuery(id+"F26.wireOp",EDGE,"E254"),sQuery(id+"F26.wireOp",EDGE,"E255"),sQuery(id+"F26.wireOp",EDGE,"E256"),sQuery(id+"F26.wireOp",EDGE,"E257"),sQuery(id+"F26.wireOp",EDGE,"E258"),sQuery(id+"F26.wireOp",EDGE,"E259"),sQuery(id+"F26.wireOp",EDGE,"E260"),sQuery(id+"F26.wireOp",EDGE,"E261"),sQuery(id+"F26.wireOp",EDGE,"E262"),sQuery(id+"F26.wireOp",EDGE,"E263"),sQuery(id+"F26.wireOp",EDGE,"E264"),sQuery(id+"F26.wireOp",EDGE,"E265"),sQuery(id+"F26.wireOp",EDGE,"E266"),sQuery(id+"F26.wireOp",EDGE,"E267"),sQuery(id+"F26.wireOp",EDGE,"E268"),sQuery(id+"F26.wireOp",EDGE,"E269"),sQuery(id+"F26.wireOp",EDGE,"E270"),sQuery(id+"F26.wireOp",EDGE,"E271"),sQuery(id+"F26.wireOp",EDGE,"E272"),sQuery(id+"F26.wireOp",EDGE,"E273"),sQuery(id+"F26.wireOp",EDGE,"E274"),sQuery(id+"F26.wireOp",EDGE,"E275"),sQuery(id+"F26.wireOp",EDGE,"E276"),sQuery(id+"F26.wireOp",EDGE,"E277"),sQuery(id+"F26.wireOp",EDGE,"E278"),sQuery(id+"F26.wireOp",EDGE,"E279"),sQuery(id+"F26.wireOp",EDGE,"E280"),sQuery(id+"F26.wireOp",EDGE,"E281"),sQuery(id+"F26.wireOp",EDGE,"E282"),sQuery(id+"F26.wireOp",EDGE,"E283"),sQuery(id+"F26.wireOp",EDGE,"E284"),sQuery(id+"F26.wireOp",EDGE,"E285"),sQuery(id+"F26.wireOp",EDGE,"E286"),sQuery(id+"F26.wireOp",EDGE,"E287"),sQuery(id+"F26.wireOp",EDGE,"E288"),sQuery(id+"F26.wireOp",EDGE,"E289.trimOffspring"),sQuery(id+"F26.wireOp",EDGE,"E291"),sQuery(id+"F26.wireOp",EDGE,"E292"),sQuery(id+"F26.wireOp",EDGE,"E293"),sQuery(id+"F26.wireOp",EDGE,"E294"),sQuery(id+"F26.wireOp",EDGE,"E295"),sQuery(id+"F26.wireOp",EDGE,"E296"),sQuery(id+"F26.wireOp",EDGE,"E297"),sQuery(id+"F26.wireOp",EDGE,"E298"),sQuery(id+"F26.wireOp",EDGE,"E299"),sQuery(id+"F26.wireOp",EDGE,"E300"),sQuery(id+"F26.wireOp",EDGE,"E301"),sQuery(id+"F26.wireOp",EDGE,"E302"),sQuery(id+"F26.wireOp",EDGE,"E303"),sQuery(id+"F26.wireOp",EDGE,"E304"),sQuery(id+"F26.wireOp",EDGE,"E305"),sQuery(id+"F26.wireOp",EDGE,"E306"),sQuery(id+"F26.wireOp",EDGE,"E307"),sQuery(id+"F26.wireOp",EDGE,"E308"),sQuery(id+"F26.wireOp",EDGE,"E309"),sQuery(id+"F26.wireOp",EDGE,"E310"),sQuery(id+"F26.wireOp",EDGE,"E311"),sQuery(id+"F26.wireOp",EDGE,"E424"),sQuery(id+"F26.wireOp",EDGE,"E425"),sQuery(id+"F26.wireOp",EDGE,"E426"),sQuery(id+"F26.wireOp",EDGE,"E427"),sQuery(id+"F26.wireOp",EDGE,"E428"),sQuery(id+"F26.wireOp",EDGE,"E429"),sQuery(id+"F26.wireOp",EDGE,"E430"),sQuery(id+"F26.wireOp",EDGE,"E431"),sQuery(id+"F26.wireOp",EDGE,"E432"),sQuery(id+"F26.wireOp",EDGE,"E433"),sQuery(id+"F26.wireOp",EDGE,"E434"),sQuery(id+"F26.wireOp",EDGE,"E435"),sQuery(id+"F26.wireOp",EDGE,"E436"),sQuery(id+"F26.wireOp",EDGE,"E437"),sQuery(id+"F26.wireOp",EDGE,"E438"),sQuery(id+"F26.wireOp",EDGE,"E439"),sQuery(id+"F26.wireOp",EDGE,"E440"),sQuery(id+"F26.wireOp",EDGE,"E441"),sQuery(id+"F26.wireOp",EDGE,"E442"),sQuery(id+"F26.wireOp",EDGE,"E443"),sQuery(id+"F26.wireOp",EDGE,"E444"),sQuery(id+"F26.wireOp",EDGE,"E445"),sQuery(id+"F26.wireOp",EDGE,"E446"),sQuery(id+"F26.wireOp",EDGE,"E447"),sQuery(id+"F26.wireOp",EDGE,"E448"),sQuery(id+"F26.wireOp",EDGE,"E449"),sQuery(id+"F26.wireOp",EDGE,"E450"),sQuery(id+"F26.wireOp",EDGE,"E451"),sQuery(id+"F26.wireOp",EDGE,"E452"),sQuery(id+"F26.wireOp",EDGE,"E453"),sQuery(id+"F26.wireOp",EDGE,"E454"),sQuery(id+"F26.wireOp",EDGE,"E455"),sQuery(id+"F26.wireOp",EDGE,"E456"),sQuery(id+"F26.wireOp",EDGE,"E457"),sQuery(id+"F26.wireOp",EDGE,"E458"),sQuery(id+"F26.wireOp",EDGE,"E459"),sQuery(id+"F26.wireOp",EDGE,"E460"),sQuery(id+"F26.wireOp",EDGE,"E461"),sQuery(id+"F26.wireOp",EDGE,"E462"),sQuery(id+"F26.wireOp",EDGE,"E463"),sQuery(id+"F26.wireOp",EDGE,"E464"),sQuery(id+"F26.wireOp",EDGE,"E465"),sQuery(id+"F26.wireOp",EDGE,"E466"),sQuery(id+"F26.wireOp",EDGE,"E467"),sQuery(id+"F26.wireOp",EDGE,"E468"),sQuery(id+"F26.wireOp",EDGE,"E469"),sQuery(id+"F26.wireOp",EDGE,"E470"),sQuery(id+"F26.wireOp",EDGE,"E471"),sQuery(id+"F26.wireOp",EDGE,"E472"),sQuery(id+"F26.wireOp",EDGE,"E473"),sQuery(id+"F26.wireOp",EDGE,"E474"),sQuery(id+"F26.wireOp",EDGE,"E475"),sQuery(id+"F26.wireOp",EDGE,"E476"),sQuery(id+"F26.wireOp",EDGE,"E477"),sQuery(id+"F26.wireOp",EDGE,"E478"),sQuery(id+"F26.wireOp",EDGE,"E479"),sQuery(id+"F26.wireOp",EDGE,"E480"),sQuery(id+"F26.wireOp",EDGE,"E481"),sQuery(id+"F26.wireOp",EDGE,"E482"),sQuery(id+"F26.wireOp",EDGE,"E483"),sQuery(id+"F26.wireOp",EDGE,"E484"),sQuery(id+"F26.wireOp",EDGE,"E485"),sQuery(id+"F26.wireOp",EDGE,"E486"),sQuery(id+"F26.wireOp",EDGE,"E487"),sQuery(id+"F26.wireOp",EDGE,"E488"),sQuery(id+"F26.wireOp",EDGE,"E489"),sQuery(id+"F26.wireOp",EDGE,"E490"),sQuery(id+"F26.wireOp",EDGE,"E491"),sQuery(id+"F26.wireOp",EDGE,"E492"),sQuery(id+"F26.wireOp",EDGE,"E493"),sQuery(id+"F26.wireOp",EDGE,"E494"),sQuery(id+"F26.wireOp",EDGE,"E495"),sQuery(id+"F26.wireOp",EDGE,"E496"),sQuery(id+"F26.wireOp",EDGE,"E497"),sQuery(id+"F26.wireOp",EDGE,"E498"),sQuery(id+"F26.wireOp",EDGE,"E499"),sQuery(id+"F26.wireOp",EDGE,"E500"),sQuery(id+"F26.wireOp",EDGE,"E501"),sQuery(id+"F26.wireOp",EDGE,"E502"),sQuery(id+"F26.wireOp",EDGE,"E503"),sQuery(id+"F26.wireOp",EDGE,"E504"),sQuery(id+"F26.wireOp",EDGE,"E505")])],"isStart":true}),makeQuery(id+"F27.opExtrude","CAP_FACE",FACE,{"disambiguationData":[OSD([sQuery(id+"F26.wireOp",EDGE,"E202"),sQuery(id+"F26.wireOp",EDGE,"E203"),sQuery(id+"F26.wireOp",EDGE,"E204"),sQuery(id+"F26.wireOp",EDGE,"E205"),sQuery(id+"F26.wireOp",EDGE,"E206"),sQuery(id+"F26.wireOp",EDGE,"E207"),sQuery(id+"F26.wireOp",EDGE,"E208")])],"isStart":true}),makeQuery(id+"F27.opExtrude","CAP_FACE",FACE,{"disambiguationData":[OSD([sQuery(id+"F26.wireOp",EDGE,"E312"),sQuery(id+"F26.wireOp",EDGE,"E313"),sQuery(id+"F26.wireOp",EDGE,"E314"),sQuery(id+"F26.wireOp",EDGE,"E315"),sQuery(id+"F26.wireOp",EDGE,"E316"),sQuery(id+"F26.wireOp",EDGE,"E317"),sQuery(id+"F26.wireOp",EDGE,"E318"),sQuery(id+"F26.wireOp",EDGE,"E319"),sQuery(id+"F26.wireOp",EDGE,"E320"),sQuery(id+"F26.wireOp",EDGE,"E321"),sQuery(id+"F26.wireOp",EDGE,"E322"),sQuery(id+"F26.wireOp",EDGE,"E323"),sQuery(id+"F26.wireOp",EDGE,"E324"),sQuery(id+"F26.wireOp",EDGE,"E325"),sQuery(id+"F26.wireOp",EDGE,"E326"),sQuery(id+"F26.wireOp",EDGE,"E327"),sQuery(id+"F26.wireOp",EDGE,"E328"),sQuery(id+"F26.wireOp",EDGE,"E329"),sQuery(id+"F26.wireOp",EDGE,"E330"),sQuery(id+"F26.wireOp",EDGE,"E331"),sQuery(id+"F26.wireOp",EDGE,"E332"),sQuery(id+"F26.wireOp",EDGE,"E333"),sQuery(id+"F26.wireOp",EDGE,"E334"),sQuery(id+"F26.wireOp",EDGE,"E335"),sQuery(id+"F26.wireOp",EDGE,"E336"),sQuery(id+"F26.wireOp",EDGE,"E337.bottom"),sQuery(id+"F26.wireOp",EDGE,"E337.top"),sQuery(id+"F26.wireOp",EDGE,"E337.left"),sQuery(id+"F26.wireOp",EDGE,"E337.right"),sQuery(id+"F26.wireOp",EDGE,"E338.bottom"),sQuery(id+"F26.wireOp",EDGE,"E338.top"),sQuery(id+"F26.wireOp",EDGE,"E338.left"),sQuery(id+"F26.wireOp",EDGE,"E338.right"),sQuery(id+"F26.wireOp",EDGE,"E339"),sQuery(id+"F26.wireOp",EDGE,"E340"),sQuery(id+"F26.wireOp",EDGE,"E341"),sQuery(id+"F26.wireOp",EDGE,"E342"),sQuery(id+"F26.wireOp",EDGE,"E343"),sQuery(id+"F26.wireOp",EDGE,"E344"),sQuery(id+"F26.wireOp",EDGE,"E345"),sQuery(id+"F26.wireOp",EDGE,"E346"),sQuery(id+"F26.wireOp",EDGE,"E347"),sQuery(id+"F26.wireOp",EDGE,"E348"),sQuery(id+"F26.wireOp",EDGE,"E349"),sQuery(id+"F26.wireOp",EDGE,"E350"),sQuery(id+"F26.wireOp",EDGE,"E351"),sQuery(id+"F26.wireOp",EDGE,"E352"),sQuery(id+"F26.wireOp",EDGE,"E353"),sQuery(id+"F26.wireOp",EDGE,"E354"),sQuery(id+"F26.wireOp",EDGE,"E355"),sQuery(id+"F26.wireOp",EDGE,"E356"),sQuery(id+"F26.wireOp",EDGE,"E357"),sQuery(id+"F26.wireOp",EDGE,"E358"),sQuery(id+"F26.wireOp",EDGE,"E359"),sQuery(id+"F26.wireOp",EDGE,"E360"),sQuery(id+"F26.wireOp",EDGE,"E361"),sQuery(id+"F26.wireOp",EDGE,"E362"),sQuery(id+"F26.wireOp",EDGE,"E363"),sQuery(id+"F26.wireOp",EDGE,"E364"),sQuery(id+"F26.wireOp",EDGE,"E365"),sQuery(id+"F26.wireOp",EDGE,"E366"),sQuery(id+"F26.wireOp",EDGE,"E367"),sQuery(id+"F26.wireOp",EDGE,"E368"),sQuery(id+"F26.wireOp",EDGE,"E369"),sQuery(id+"F26.wireOp",EDGE,"E370"),sQuery(id+"F26.wireOp",EDGE,"E371"),sQuery(id+"F26.wireOp",EDGE,"E372"),sQuery(id+"F26.wireOp",EDGE,"E373"),sQuery(id+"F26.wireOp",EDGE,"E374")])],"isStart":true}),makeQuery(id+"F27.opExtrude","CAP_FACE",FACE,{"disambiguationData":[OSD([sQuery(id+"F26.wireOp",EDGE,"E375"),sQuery(id+"F26.wireOp",EDGE,"E376"),sQuery(id+"F26.wireOp",EDGE,"E377"),sQuery(id+"F26.wireOp",EDGE,"E378"),sQuery(id+"F26.wireOp",EDGE,"E379"),sQuery(id+"F26.wireOp",EDGE,"E380"),sQuery(id+"F26.wireOp",EDGE,"E381"),sQuery(id+"F26.wireOp",EDGE,"E382"),sQuery(id+"F26.wireOp",EDGE,"E383"),sQuery(id+"F26.wireOp",EDGE,"E384"),sQuery(id+"F26.wireOp",EDGE,"E385.trimOffspring"),sQuery(id+"F26.wireOp",EDGE,"E386.trimOffspring")])],"isStart":true}),makeQuery(id+"F27.opExtrude","CAP_FACE",FACE,{"disambiguationData":[OSD([sQuery(id+"F26.wireOp",EDGE,"E387"),sQuery(id+"F26.wireOp",EDGE,"E388"),sQuery(id+"F26.wireOp",EDGE,"E389"),sQuery(id+"F26.wireOp",EDGE,"E390"),sQuery(id+"F26.wireOp",EDGE,"E391"),sQuery(id+"F26.wireOp",EDGE,"E392"),sQuery(id+"F26.wireOp",EDGE,"E393"),sQuery(id+"F26.wireOp",EDGE,"E394")])],"isStart":true}),makeQuery(id+"F27.opExtrude","CAP_FACE",FACE,{"disambiguationData":[OSD([sQuery(id+"F26.wireOp",EDGE,"E395"),sQuery(id+"F26.wireOp",EDGE,"E396"),sQuery(id+"F26.wireOp",EDGE,"E397"),sQuery(id+"F26.wireOp",EDGE,"E398"),sQuery(id+"F26.wireOp",EDGE,"E399"),sQuery(id+"F26.wireOp",EDGE,"E400"),sQuery(id+"F26.wireOp",EDGE,"E401"),sQuery(id+"F26.wireOp",EDGE,"E402"),sQuery(id+"F26.wireOp",EDGE,"E403"),sQuery(id+"F26.wireOp",EDGE,"E404"),sQuery(id+"F26.wireOp",EDGE,"E405"),sQuery(id+"F26.wireOp",EDGE,"E406"),sQuery(id+"F26.wireOp",EDGE,"E407"),sQuery(id+"F26.wireOp",EDGE,"E408"),sQuery(id+"F26.wireOp",EDGE,"E409"),sQuery(id+"F26.wireOp",EDGE,"E410"),sQuery(id+"F26.wireOp",EDGE,"E411"),sQuery(id+"F26.wireOp",EDGE,"E412"),sQuery(id+"F26.wireOp",EDGE,"E413"),sQuery(id+"F26.wireOp",EDGE,"E414"),sQuery(id+"F26.wireOp",EDGE,"E415"),sQuery(id+"F26.wireOp",EDGE,"E416"),sQuery(id+"F26.wireOp",EDGE,"E417"),sQuery(id+"F26.wireOp",EDGE,"E418")])],"isStart":true}),makeQuery(id+"F27.opExtrude","CAP_FACE",FACE,{"disambiguationData":[OSD([sQuery(id+"F26.wireOp",EDGE,"E419.bottom"),sQuery(id+"F26.wireOp",EDGE,"E419.top"),sQuery(id+"F26.wireOp",EDGE,"E419.left"),sQuery(id+"F26.wireOp",EDGE,"E419.right")])],"isStart":true}),makeQuery(id+"F27.opExtrude","CAP_FACE",FACE,{"disambiguationData":[OSD([sQuery(id+"F26.wireOp",EDGE,"E420.bottom"),sQuery(id+"F26.wireOp",EDGE,"E420.top"),sQuery(id+"F26.wireOp",EDGE,"E420.left"),sQuery(id+"F26.wireOp",EDGE,"E420.right")])],"isStart":true}),makeQuery(id+"F27.opExtrude","CAP_FACE",FACE,{"disambiguationData":[OSD([sQuery(id+"F26.wireOp",EDGE,"E421.bottom"),sQuery(id+"F26.wireOp",EDGE,"E421.top"),sQuery(id+"F26.wireOp",EDGE,"E421.left"),sQuery(id+"F26.wireOp",EDGE,"E421.right")])],"isStart":true}),makeQuery(id+"F27.opExtrude","CAP_FACE",FACE,{"disambiguationData":[OSD([sQuery(id+"F26.wireOp",EDGE,"E422.bottom"),sQuery(id+"F26.wireOp",EDGE,"E422.top"),sQuery(id+"F26.wireOp",EDGE,"E422.left"),sQuery(id+"F26.wireOp",EDGE,"E422.right")])],"isStart":true}),makeQuery(id+"F27.opExtrude","CAP_FACE",FACE,{"disambiguationData":[OSD([sQuery(id+"F26.wireOp",EDGE,"E423.bottom"),sQuery(id+"F26.wireOp",EDGE,"E423.top"),sQuery(id+"F26.wireOp",EDGE,"E423.left"),sQuery(id+"F26.wireOp",EDGE,"E423.right")])],"isStart":true}),makeQuery(id+"F27.opExtrude","CAP_FACE",FACE,{"disambiguationData":[OSD([sQuery(id+"F26.wireOp",EDGE,"E506"),sQuery(id+"F26.wireOp",EDGE,"E507"),sQuery(id+"F26.wireOp",EDGE,"E508"),sQuery(id+"F26.wireOp",EDGE,"E509"),sQuery(id+"F26.wireOp",EDGE,"E510"),sQuery(id+"F26.wireOp",EDGE,"E511"),sQuery(id+"F26.wireOp",EDGE,"E512"),sQuery(id+"F26.wireOp",EDGE,"E513")])],"isStart":true}),makeQuery(id+"F27.opExtrude","CAP_FACE",FACE,{"disambiguationData":[OSD([sQuery(id+"F26.wireOp",EDGE,"E514"),sQuery(id+"F26.wireOp",EDGE,"E515"),sQuery(id+"F26.wireOp",EDGE,"E516"),sQuery(id+"F26.wireOp",EDGE,"E517"),sQuery(id+"F26.wireOp",EDGE,"E518"),sQuery(id+"F26.wireOp",EDGE,"E519"),sQuery(id+"F26.wireOp",EDGE,"E520"),sQuery(id+"F26.wireOp",EDGE,"E521"),sQuery(id+"F26.wireOp",EDGE,"E522"),sQuery(id+"F26.wireOp",EDGE,"E523"),sQuery(id+"F26.wireOp",EDGE,"E524"),sQuery(id+"F26.wireOp",EDGE,"E525"),sQuery(id+"F26.wireOp",EDGE,"E526"),sQuery(id+"F26.wireOp",EDGE,"E527"),sQuery(id+"F26.wireOp",EDGE,"E528"),sQuery(id+"F26.wireOp",EDGE,"E529"),sQuery(id+"F26.wireOp",EDGE,"E530"),sQuery(id+"F26.wireOp",EDGE,"E531"),sQuery(id+"F26.wireOp",EDGE,"E532"),sQuery(id+"F26.wireOp",EDGE,"E533"),sQuery(id+"F26.wireOp",EDGE,"E534"),sQuery(id+"F26.wireOp",EDGE,"E535"),sQuery(id+"F26.wireOp",EDGE,"E536"),sQuery(id+"F26.wireOp",EDGE,"E537"),sQuery(id+"F26.wireOp",EDGE,"E538")])],"isStart":true}),makeQuery(id+"F27.opExtrude","CAP_FACE",FACE,{"disambiguationData":[OSD([sQuery(id+"F26.wireOp",EDGE,"E539"),sQuery(id+"F26.wireOp",EDGE,"E540"),sQuery(id+"F26.wireOp",EDGE,"E541"),sQuery(id+"F26.wireOp",EDGE,"E542"),sQuery(id+"F26.wireOp",EDGE,"E543"),sQuery(id+"F26.wireOp",EDGE,"E544"),sQuery(id+"F26.wireOp",EDGE,"E545"),sQuery(id+"F26.wireOp",EDGE,"E546")])],"isStart":true}),makeQuery(id+"F27.opExtrude","CAP_FACE",FACE,{"disambiguationData":[OSD([sQuery(id+"F26.wireOp",EDGE,"E551"),sQuery(id+"F26.wireOp",EDGE,"E552"),sQuery(id+"F26.wireOp",EDGE,"E553"),sQuery(id+"F26.wireOp",EDGE,"E554")])],"isStart":true}),makeQuery(id+"F27.opExtrude","CAP_FACE",FACE,{"disambiguationData":[OSD([sQuery(id+"F26.wireOp",EDGE,"E555"),sQuery(id+"F26.wireOp",EDGE,"E556"),sQuery(id+"F26.wireOp",EDGE,"E557"),sQuery(id+"F26.wireOp",EDGE,"E558"),sQuery(id+"F26.wireOp",EDGE,"E559"),sQuery(id+"F26.wireOp",EDGE,"E560"),sQuery(id+"F26.wireOp",EDGE,"E561"),sQuery(id+"F26.wireOp",EDGE,"E562"),sQuery(id+"F26.wireOp",EDGE,"E563"),sQuery(id+"F26.wireOp",EDGE,"E564"),sQuery(id+"F26.wireOp",EDGE,"E565"),sQuery(id+"F26.wireOp",EDGE,"E566")])],"isStart":true}),makeQuery(id+"F29.opExtrude","CAP_FACE",FACE,{"disambiguationData":[OSD([sQuery(id+"F28.wireOp",EDGE,"E567"),sQuery(id+"F28.wireOp",EDGE,"E568"),sQuery(id+"F28.wireOp",EDGE,"E569"),sQuery(id+"F28.wireOp",EDGE,"E570"),sQuery(id+"F28.wireOp",EDGE,"E571"),sQuery(id+"F28.wireOp",EDGE,"E572"),sQuery(id+"F28.wireOp",EDGE,"E573"),sQuery(id+"F28.wireOp",EDGE,"E574"),sQuery(id+"F28.wireOp",EDGE,"E575"),sQuery(id+"F28.wireOp",EDGE,"E576"),subQ0,sQuery(id+"F28.wireOp",EDGE,"E591")])],"isStart":true}),makeQuery(id+"F29.opExtrude","CAP_FACE",FACE,{"disambiguationData":[OSD([subQ0,sQuery(id+"F28.wireOp",EDGE,"E578"),sQuery(id+"F28.wireOp",EDGE,"E579"),sQuery(id+"F28.wireOp",EDGE,"E580"),sQuery(id+"F28.wireOp",EDGE,"E581"),sQuery(id+"F28.wireOp",EDGE,"E582"),sQuery(id+"F28.wireOp",EDGE,"E583"),sQuery(id+"F28.wireOp",EDGE,"E584"),sQuery(id+"F28.wireOp",EDGE,"E585"),sQuery(id+"F28.wireOp",EDGE,"E586"),sQuery(id+"F28.wireOp",EDGE,"E587"),sQuery(id+"F28.wireOp",EDGE,"E588"),sQuery(id+"F28.wireOp",EDGE,"E589"),sQuery(id+"F28.wireOp",EDGE,"E590")])],"isStart":true})]});}
            var sketch = newSketch(context, id + "F30", { "sketchPlane" : qUnion([Q0])});
            skLineSegment(sketch, "E592.bottom", {"start": v(-4.99, -7.13) * mm, "end": v(-0.55, -7.13) * mm});
            skLineSegment(sketch, "E592.top", {"start": v(-4.99, -7.74) * mm, "end": v(-0.55, -7.74) * mm});
            skLineSegment(sketch, "E592.left", {"start": v(-4.99, -7.13) * mm, "end": v(-4.99, -7.74) * mm});
            skLineSegment(sketch, "E592.right", {"start": v(-0.55, -7.13) * mm, "end": v(-0.55, -7.74) * mm});
            skSolve(sketch);
        }
        {
            var Q0;
            Q0 = qSketchRegion(id + "F30", true);
            extrude(context, id + "F31", {"entities" : qUnion([Q0]), "operationType" : NewBodyOperationType.ADD, "oppositeDirection" : true, "depth" : 1 * mm, "offsetDistance" : 25 * mm});
        }
        {
            var Q0;
            Q0=makeQuery(id+"F27.opExtrude","SWEPT_BODY",BODY,{"disambiguationData":[OSD([sQuery(id+"F26.wireOp",EDGE,"E92"),sQuery(id+"F26.wireOp",EDGE,"E93"),sQuery(id+"F26.wireOp",EDGE,"E94"),sQuery(id+"F26.wireOp",EDGE,"E95"),sQuery(id+"F26.wireOp",EDGE,"E96"),sQuery(id+"F26.wireOp",EDGE,"E97"),sQuery(id+"F26.wireOp",EDGE,"E98"),sQuery(id+"F26.wireOp",EDGE,"E99"),sQuery(id+"F26.wireOp",EDGE,"E100"),sQuery(id+"F26.wireOp",EDGE,"E101"),sQuery(id+"F26.wireOp",EDGE,"E102"),sQuery(id+"F26.wireOp",EDGE,"E103"),sQuery(id+"F26.wireOp",EDGE,"E104"),sQuery(id+"F26.wireOp",EDGE,"E105"),sQuery(id+"F26.wireOp",EDGE,"E106"),sQuery(id+"F26.wireOp",EDGE,"E107"),sQuery(id+"F26.wireOp",EDGE,"E108.trimOffspring"),sQuery(id+"F26.wireOp",EDGE,"E109.trimOffspring"),sQuery(id+"F26.wireOp",EDGE,"E110.trimOffspring"),sQuery(id+"F26.wireOp",EDGE,"E111.trimOffspring"),sQuery(id+"F26.wireOp",EDGE,"E112.trimOffspring"),sQuery(id+"F26.wireOp",EDGE,"E113.trimOffspring"),sQuery(id+"F26.wireOp",EDGE,"E114.trimOffspring"),sQuery(id+"F26.wireOp",EDGE,"E115.trimOffspring"),sQuery(id+"F26.wireOp",EDGE,"E116.trimOffspring"),sQuery(id+"F26.wireOp",EDGE,"E117"),sQuery(id+"F26.wireOp",EDGE,"E118"),sQuery(id+"F26.wireOp",EDGE,"E119"),sQuery(id+"F26.wireOp",EDGE,"E120"),sQuery(id+"F26.wireOp",EDGE,"E121"),sQuery(id+"F26.wireOp",EDGE,"E122"),sQuery(id+"F26.wireOp",EDGE,"E123"),sQuery(id+"F26.wireOp",EDGE,"E124"),sQuery(id+"F26.wireOp",EDGE,"E125"),sQuery(id+"F26.wireOp",EDGE,"E126"),sQuery(id+"F26.wireOp",EDGE,"E127"),sQuery(id+"F26.wireOp",EDGE,"E128"),sQuery(id+"F26.wireOp",EDGE,"E129"),sQuery(id+"F26.wireOp",EDGE,"E130"),sQuery(id+"F26.wireOp",EDGE,"E131"),sQuery(id+"F26.wireOp",EDGE,"E132"),sQuery(id+"F26.wireOp",EDGE,"E133"),sQuery(id+"F26.wireOp",EDGE,"E134"),sQuery(id+"F26.wireOp",EDGE,"E135"),sQuery(id+"F26.wireOp",EDGE,"E136"),sQuery(id+"F26.wireOp",EDGE,"E137"),sQuery(id+"F26.wireOp",EDGE,"E138"),sQuery(id+"F26.wireOp",EDGE,"E139"),sQuery(id+"F26.wireOp",EDGE,"E140"),sQuery(id+"F26.wireOp",EDGE,"E141"),sQuery(id+"F26.wireOp",EDGE,"E142"),sQuery(id+"F26.wireOp",EDGE,"E143"),sQuery(id+"F26.wireOp",EDGE,"E144"),sQuery(id+"F26.wireOp",EDGE,"E145"),sQuery(id+"F26.wireOp",EDGE,"E146"),sQuery(id+"F26.wireOp",EDGE,"E147"),sQuery(id+"F26.wireOp",EDGE,"E148"),sQuery(id+"F26.wireOp",EDGE,"E149"),sQuery(id+"F26.wireOp",EDGE,"E150"),sQuery(id+"F26.wireOp",EDGE,"E151"),sQuery(id+"F26.wireOp",EDGE,"E152"),sQuery(id+"F26.wireOp",EDGE,"E153"),sQuery(id+"F26.wireOp",EDGE,"E154"),sQuery(id+"F26.wireOp",EDGE,"E155"),sQuery(id+"F26.wireOp",EDGE,"E156"),sQuery(id+"F26.wireOp",EDGE,"E157.trimOffspring"),sQuery(id+"F26.wireOp",EDGE,"E158"),sQuery(id+"F26.wireOp",EDGE,"E159"),sQuery(id+"F26.wireOp",EDGE,"E160"),sQuery(id+"F26.wireOp",EDGE,"E161"),sQuery(id+"F26.wireOp",EDGE,"E162"),sQuery(id+"F26.wireOp",EDGE,"E163"),sQuery(id+"F26.wireOp",EDGE,"E164"),sQuery(id+"F26.wireOp",EDGE,"E165"),sQuery(id+"F26.wireOp",EDGE,"E166"),sQuery(id+"F26.wireOp",EDGE,"E167"),sQuery(id+"F26.wireOp",EDGE,"E168"),sQuery(id+"F26.wireOp",EDGE,"E169"),sQuery(id+"F26.wireOp",EDGE,"E170"),sQuery(id+"F26.wireOp",EDGE,"E171"),sQuery(id+"F26.wireOp",EDGE,"E172"),sQuery(id+"F26.wireOp",EDGE,"E173"),sQuery(id+"F26.wireOp",EDGE,"E174"),sQuery(id+"F26.wireOp",EDGE,"E175"),sQuery(id+"F26.wireOp",EDGE,"E176"),sQuery(id+"F26.wireOp",EDGE,"E177"),sQuery(id+"F26.wireOp",EDGE,"E178"),sQuery(id+"F26.wireOp",EDGE,"E179"),sQuery(id+"F26.wireOp",EDGE,"E180"),sQuery(id+"F26.wireOp",EDGE,"E181"),sQuery(id+"F26.wireOp",EDGE,"E182"),sQuery(id+"F26.wireOp",EDGE,"E183"),sQuery(id+"F26.wireOp",EDGE,"E184"),sQuery(id+"F26.wireOp",EDGE,"E185"),sQuery(id+"F26.wireOp",EDGE,"E186"),sQuery(id+"F26.wireOp",EDGE,"E187"),sQuery(id+"F26.wireOp",EDGE,"E188.trimOffspring"),sQuery(id+"F26.wireOp",EDGE,"E189.trimOffspring"),sQuery(id+"F26.wireOp",EDGE,"E190"),sQuery(id+"F26.wireOp",EDGE,"E191"),sQuery(id+"F26.wireOp",EDGE,"E192"),sQuery(id+"F26.wireOp",EDGE,"E193"),sQuery(id+"F26.wireOp",EDGE,"E198"),sQuery(id+"F26.wireOp",EDGE,"E199"),sQuery(id+"F26.wireOp",EDGE,"E200"),sQuery(id+"F26.wireOp",EDGE,"E201"),sQuery(id+"F26.wireOp",EDGE,"E225"),sQuery(id+"F26.wireOp",EDGE,"E226"),sQuery(id+"F26.wireOp",EDGE,"E227"),sQuery(id+"F26.wireOp",EDGE,"E228"),sQuery(id+"F26.wireOp",EDGE,"E229"),sQuery(id+"F26.wireOp",EDGE,"E230"),sQuery(id+"F26.wireOp",EDGE,"E231"),sQuery(id+"F26.wireOp",EDGE,"E232"),sQuery(id+"F26.wireOp",EDGE,"E233"),sQuery(id+"F26.wireOp",EDGE,"E234"),sQuery(id+"F26.wireOp",EDGE,"E235"),sQuery(id+"F26.wireOp",EDGE,"E236"),sQuery(id+"F26.wireOp",EDGE,"E237"),sQuery(id+"F26.wireOp",EDGE,"E238"),sQuery(id+"F26.wireOp",EDGE,"E239"),sQuery(id+"F26.wireOp",EDGE,"E240"),sQuery(id+"F26.wireOp",EDGE,"E241"),sQuery(id+"F26.wireOp",EDGE,"E242"),sQuery(id+"F26.wireOp",EDGE,"E243"),sQuery(id+"F26.wireOp",EDGE,"E244"),sQuery(id+"F26.wireOp",EDGE,"E245"),sQuery(id+"F26.wireOp",EDGE,"E246"),sQuery(id+"F26.wireOp",EDGE,"E247"),sQuery(id+"F26.wireOp",EDGE,"E248"),sQuery(id+"F26.wireOp",EDGE,"E249"),sQuery(id+"F26.wireOp",EDGE,"E250"),sQuery(id+"F26.wireOp",EDGE,"E251"),sQuery(id+"F26.wireOp",EDGE,"E252"),sQuery(id+"F26.wireOp",EDGE,"E253"),sQuery(id+"F26.wireOp",EDGE,"E254"),sQuery(id+"F26.wireOp",EDGE,"E255"),sQuery(id+"F26.wireOp",EDGE,"E256"),sQuery(id+"F26.wireOp",EDGE,"E257"),sQuery(id+"F26.wireOp",EDGE,"E258"),sQuery(id+"F26.wireOp",EDGE,"E259"),sQuery(id+"F26.wireOp",EDGE,"E260"),sQuery(id+"F26.wireOp",EDGE,"E261"),sQuery(id+"F26.wireOp",EDGE,"E262"),sQuery(id+"F26.wireOp",EDGE,"E263"),sQuery(id+"F26.wireOp",EDGE,"E264"),sQuery(id+"F26.wireOp",EDGE,"E265"),sQuery(id+"F26.wireOp",EDGE,"E266"),sQuery(id+"F26.wireOp",EDGE,"E267"),sQuery(id+"F26.wireOp",EDGE,"E268"),sQuery(id+"F26.wireOp",EDGE,"E269"),sQuery(id+"F26.wireOp",EDGE,"E270"),sQuery(id+"F26.wireOp",EDGE,"E271"),sQuery(id+"F26.wireOp",EDGE,"E272"),sQuery(id+"F26.wireOp",EDGE,"E273"),sQuery(id+"F26.wireOp",EDGE,"E274"),sQuery(id+"F26.wireOp",EDGE,"E275"),sQuery(id+"F26.wireOp",EDGE,"E276"),sQuery(id+"F26.wireOp",EDGE,"E277"),sQuery(id+"F26.wireOp",EDGE,"E278"),sQuery(id+"F26.wireOp",EDGE,"E279"),sQuery(id+"F26.wireOp",EDGE,"E280"),sQuery(id+"F26.wireOp",EDGE,"E281"),sQuery(id+"F26.wireOp",EDGE,"E282"),sQuery(id+"F26.wireOp",EDGE,"E283"),sQuery(id+"F26.wireOp",EDGE,"E284"),sQuery(id+"F26.wireOp",EDGE,"E285"),sQuery(id+"F26.wireOp",EDGE,"E286"),sQuery(id+"F26.wireOp",EDGE,"E287"),sQuery(id+"F26.wireOp",EDGE,"E288"),sQuery(id+"F26.wireOp",EDGE,"E289.trimOffspring"),sQuery(id+"F26.wireOp",EDGE,"E291"),sQuery(id+"F26.wireOp",EDGE,"E292"),sQuery(id+"F26.wireOp",EDGE,"E293"),sQuery(id+"F26.wireOp",EDGE,"E294"),sQuery(id+"F26.wireOp",EDGE,"E295"),sQuery(id+"F26.wireOp",EDGE,"E296"),sQuery(id+"F26.wireOp",EDGE,"E297"),sQuery(id+"F26.wireOp",EDGE,"E298"),sQuery(id+"F26.wireOp",EDGE,"E299"),sQuery(id+"F26.wireOp",EDGE,"E300"),sQuery(id+"F26.wireOp",EDGE,"E301"),sQuery(id+"F26.wireOp",EDGE,"E302"),sQuery(id+"F26.wireOp",EDGE,"E303"),sQuery(id+"F26.wireOp",EDGE,"E304"),sQuery(id+"F26.wireOp",EDGE,"E305"),sQuery(id+"F26.wireOp",EDGE,"E306"),sQuery(id+"F26.wireOp",EDGE,"E307"),sQuery(id+"F26.wireOp",EDGE,"E308"),sQuery(id+"F26.wireOp",EDGE,"E309"),sQuery(id+"F26.wireOp",EDGE,"E310"),sQuery(id+"F26.wireOp",EDGE,"E311"),sQuery(id+"F26.wireOp",EDGE,"E424"),sQuery(id+"F26.wireOp",EDGE,"E425"),sQuery(id+"F26.wireOp",EDGE,"E426"),sQuery(id+"F26.wireOp",EDGE,"E427"),sQuery(id+"F26.wireOp",EDGE,"E428"),sQuery(id+"F26.wireOp",EDGE,"E429"),sQuery(id+"F26.wireOp",EDGE,"E430"),sQuery(id+"F26.wireOp",EDGE,"E431"),sQuery(id+"F26.wireOp",EDGE,"E432"),sQuery(id+"F26.wireOp",EDGE,"E433"),sQuery(id+"F26.wireOp",EDGE,"E434"),sQuery(id+"F26.wireOp",EDGE,"E435"),sQuery(id+"F26.wireOp",EDGE,"E436"),sQuery(id+"F26.wireOp",EDGE,"E437"),sQuery(id+"F26.wireOp",EDGE,"E438"),sQuery(id+"F26.wireOp",EDGE,"E439"),sQuery(id+"F26.wireOp",EDGE,"E440"),sQuery(id+"F26.wireOp",EDGE,"E441"),sQuery(id+"F26.wireOp",EDGE,"E442"),sQuery(id+"F26.wireOp",EDGE,"E443"),sQuery(id+"F26.wireOp",EDGE,"E444"),sQuery(id+"F26.wireOp",EDGE,"E445"),sQuery(id+"F26.wireOp",EDGE,"E446"),sQuery(id+"F26.wireOp",EDGE,"E447"),sQuery(id+"F26.wireOp",EDGE,"E448"),sQuery(id+"F26.wireOp",EDGE,"E449"),sQuery(id+"F26.wireOp",EDGE,"E450"),sQuery(id+"F26.wireOp",EDGE,"E451"),sQuery(id+"F26.wireOp",EDGE,"E452"),sQuery(id+"F26.wireOp",EDGE,"E453"),sQuery(id+"F26.wireOp",EDGE,"E454"),sQuery(id+"F26.wireOp",EDGE,"E455"),sQuery(id+"F26.wireOp",EDGE,"E456"),sQuery(id+"F26.wireOp",EDGE,"E457"),sQuery(id+"F26.wireOp",EDGE,"E458"),sQuery(id+"F26.wireOp",EDGE,"E459"),sQuery(id+"F26.wireOp",EDGE,"E460"),sQuery(id+"F26.wireOp",EDGE,"E461"),sQuery(id+"F26.wireOp",EDGE,"E462"),sQuery(id+"F26.wireOp",EDGE,"E463"),sQuery(id+"F26.wireOp",EDGE,"E464"),sQuery(id+"F26.wireOp",EDGE,"E465"),sQuery(id+"F26.wireOp",EDGE,"E466"),sQuery(id+"F26.wireOp",EDGE,"E467"),sQuery(id+"F26.wireOp",EDGE,"E468"),sQuery(id+"F26.wireOp",EDGE,"E469"),sQuery(id+"F26.wireOp",EDGE,"E470"),sQuery(id+"F26.wireOp",EDGE,"E471"),sQuery(id+"F26.wireOp",EDGE,"E472"),sQuery(id+"F26.wireOp",EDGE,"E473"),sQuery(id+"F26.wireOp",EDGE,"E474"),sQuery(id+"F26.wireOp",EDGE,"E475"),sQuery(id+"F26.wireOp",EDGE,"E476"),sQuery(id+"F26.wireOp",EDGE,"E477"),sQuery(id+"F26.wireOp",EDGE,"E478"),sQuery(id+"F26.wireOp",EDGE,"E479"),sQuery(id+"F26.wireOp",EDGE,"E480"),sQuery(id+"F26.wireOp",EDGE,"E481"),sQuery(id+"F26.wireOp",EDGE,"E482"),sQuery(id+"F26.wireOp",EDGE,"E483"),sQuery(id+"F26.wireOp",EDGE,"E484"),sQuery(id+"F26.wireOp",EDGE,"E485"),sQuery(id+"F26.wireOp",EDGE,"E486"),sQuery(id+"F26.wireOp",EDGE,"E487"),sQuery(id+"F26.wireOp",EDGE,"E488"),sQuery(id+"F26.wireOp",EDGE,"E489"),sQuery(id+"F26.wireOp",EDGE,"E490"),sQuery(id+"F26.wireOp",EDGE,"E491"),sQuery(id+"F26.wireOp",EDGE,"E492"),sQuery(id+"F26.wireOp",EDGE,"E493"),sQuery(id+"F26.wireOp",EDGE,"E494"),sQuery(id+"F26.wireOp",EDGE,"E495"),sQuery(id+"F26.wireOp",EDGE,"E496"),sQuery(id+"F26.wireOp",EDGE,"E497"),sQuery(id+"F26.wireOp",EDGE,"E498"),sQuery(id+"F26.wireOp",EDGE,"E499"),sQuery(id+"F26.wireOp",EDGE,"E500"),sQuery(id+"F26.wireOp",EDGE,"E501"),sQuery(id+"F26.wireOp",EDGE,"E502"),sQuery(id+"F26.wireOp",EDGE,"E503"),sQuery(id+"F26.wireOp",EDGE,"E504"),sQuery(id+"F26.wireOp",EDGE,"E505")])]});
            var Q1;
            Q1=qCreatedBy(makeId("Front.planeOp"),FACE);
            mirror(context, id + "F32", {"entities" : qUnion([Q0]), "mirrorPlane" : qUnion([Q1])});
        }
        {
            var Q0;
            Q0=makeQuery(id+"F4.opExtrude","CAP_FACE",FACE,{"disambiguationData":[OSD([sQuery(id+"F3.wireOp",EDGE,"E6"),sQuery(id+"F3.wireOp",EDGE,"E7"),sQuery(id+"F3.wireOp",EDGE,"E8"),sQuery(id+"F3.wireOp",EDGE,"E17"),sQuery(id+"F3.wireOp",EDGE,"E19"),sQuery(id+"F3.wireOp",EDGE,"E20"),sQuery(id+"F3.wireOp",EDGE,"E21"),sQuery(id+"F3.wireOp",EDGE,"E22.MirrorCS"),sQuery(id+"F3.wireOp",EDGE,"E23.MirrorCS"),sQuery(id+"F3.wireOp",EDGE,"E24.MirrorCS"),sQuery(id+"F3.wireOp",EDGE,"E25.MirrorCS"),sQuery(id+"F3.wireOp",EDGE,"E26"),sQuery(id+"F3.wireOp",EDGE,"E27"),sQuery(id+"F3.wireOp",EDGE,"E28"),sQuery(id+"F3.wireOp",EDGE,"E29"),sQuery(id+"F3.wireOp",EDGE,"E30"),sQuery(id+"F3.wireOp",EDGE,"E32"),sQuery(id+"F3.wireOp",EDGE,"E33"),sQuery(id+"F3.wireOp",EDGE,"E34"),sQuery(id+"F3.wireOp",EDGE,"E36"),sQuery(id+"F3.wireOp",EDGE,"E37"),sQuery(id+"F3.wireOp",EDGE,"E38"),sQuery(id+"F3.wireOp",EDGE,"E40"),sQuery(id+"F3.wireOp",EDGE,"E41"),sQuery(id+"F3.wireOp",EDGE,"E42"),sQuery(id+"F3.wireOp",EDGE,"E43"),sQuery(id+"F3.wireOp",EDGE,"E44"),sQuery(id+"F3.wireOp",EDGE,"E45"),sQuery(id+"F3.wireOp",EDGE,"E46.MirrorCS"),sQuery(id+"F3.wireOp",EDGE,"E47.MirrorCS"),sQuery(id+"F3.wireOp",EDGE,"E48.MirrorCS")])],"isStart":true});
            fillet(context, id + "F33", {"entities" : qUnion([Q0]), "radius" : .2 * mm, "tangentPropagation" : true, "allowEdgeOverflow" : false});
        }
        {
            var Q0;
            Q0=makeQuery(id+"F27.opExtrude","SWEPT_BODY",BODY,{"disambiguationData":[OSD([sQuery(id+"F26.wireOp",EDGE,"E92"),sQuery(id+"F26.wireOp",EDGE,"E93"),sQuery(id+"F26.wireOp",EDGE,"E94"),sQuery(id+"F26.wireOp",EDGE,"E95"),sQuery(id+"F26.wireOp",EDGE,"E96"),sQuery(id+"F26.wireOp",EDGE,"E97"),sQuery(id+"F26.wireOp",EDGE,"E98"),sQuery(id+"F26.wireOp",EDGE,"E99"),sQuery(id+"F26.wireOp",EDGE,"E100"),sQuery(id+"F26.wireOp",EDGE,"E101"),sQuery(id+"F26.wireOp",EDGE,"E102"),sQuery(id+"F26.wireOp",EDGE,"E103"),sQuery(id+"F26.wireOp",EDGE,"E104"),sQuery(id+"F26.wireOp",EDGE,"E105"),sQuery(id+"F26.wireOp",EDGE,"E106"),sQuery(id+"F26.wireOp",EDGE,"E107"),sQuery(id+"F26.wireOp",EDGE,"E108.trimOffspring"),sQuery(id+"F26.wireOp",EDGE,"E109.trimOffspring"),sQuery(id+"F26.wireOp",EDGE,"E110.trimOffspring"),sQuery(id+"F26.wireOp",EDGE,"E111.trimOffspring"),sQuery(id+"F26.wireOp",EDGE,"E112.trimOffspring"),sQuery(id+"F26.wireOp",EDGE,"E113.trimOffspring"),sQuery(id+"F26.wireOp",EDGE,"E114.trimOffspring"),sQuery(id+"F26.wireOp",EDGE,"E115.trimOffspring"),sQuery(id+"F26.wireOp",EDGE,"E116.trimOffspring"),sQuery(id+"F26.wireOp",EDGE,"E117"),sQuery(id+"F26.wireOp",EDGE,"E118"),sQuery(id+"F26.wireOp",EDGE,"E119"),sQuery(id+"F26.wireOp",EDGE,"E120"),sQuery(id+"F26.wireOp",EDGE,"E121"),sQuery(id+"F26.wireOp",EDGE,"E122"),sQuery(id+"F26.wireOp",EDGE,"E123"),sQuery(id+"F26.wireOp",EDGE,"E124"),sQuery(id+"F26.wireOp",EDGE,"E125"),sQuery(id+"F26.wireOp",EDGE,"E126"),sQuery(id+"F26.wireOp",EDGE,"E127"),sQuery(id+"F26.wireOp",EDGE,"E128"),sQuery(id+"F26.wireOp",EDGE,"E129"),sQuery(id+"F26.wireOp",EDGE,"E130"),sQuery(id+"F26.wireOp",EDGE,"E131"),sQuery(id+"F26.wireOp",EDGE,"E132"),sQuery(id+"F26.wireOp",EDGE,"E133"),sQuery(id+"F26.wireOp",EDGE,"E134"),sQuery(id+"F26.wireOp",EDGE,"E135"),sQuery(id+"F26.wireOp",EDGE,"E136"),sQuery(id+"F26.wireOp",EDGE,"E137"),sQuery(id+"F26.wireOp",EDGE,"E138"),sQuery(id+"F26.wireOp",EDGE,"E139"),sQuery(id+"F26.wireOp",EDGE,"E140"),sQuery(id+"F26.wireOp",EDGE,"E141"),sQuery(id+"F26.wireOp",EDGE,"E142"),sQuery(id+"F26.wireOp",EDGE,"E143"),sQuery(id+"F26.wireOp",EDGE,"E144"),sQuery(id+"F26.wireOp",EDGE,"E145"),sQuery(id+"F26.wireOp",EDGE,"E146"),sQuery(id+"F26.wireOp",EDGE,"E147"),sQuery(id+"F26.wireOp",EDGE,"E148"),sQuery(id+"F26.wireOp",EDGE,"E149"),sQuery(id+"F26.wireOp",EDGE,"E150"),sQuery(id+"F26.wireOp",EDGE,"E151"),sQuery(id+"F26.wireOp",EDGE,"E152"),sQuery(id+"F26.wireOp",EDGE,"E153"),sQuery(id+"F26.wireOp",EDGE,"E154"),sQuery(id+"F26.wireOp",EDGE,"E155"),sQuery(id+"F26.wireOp",EDGE,"E156"),sQuery(id+"F26.wireOp",EDGE,"E157.trimOffspring"),sQuery(id+"F26.wireOp",EDGE,"E158"),sQuery(id+"F26.wireOp",EDGE,"E159"),sQuery(id+"F26.wireOp",EDGE,"E160"),sQuery(id+"F26.wireOp",EDGE,"E161"),sQuery(id+"F26.wireOp",EDGE,"E162"),sQuery(id+"F26.wireOp",EDGE,"E163"),sQuery(id+"F26.wireOp",EDGE,"E164"),sQuery(id+"F26.wireOp",EDGE,"E165"),sQuery(id+"F26.wireOp",EDGE,"E166"),sQuery(id+"F26.wireOp",EDGE,"E167"),sQuery(id+"F26.wireOp",EDGE,"E168"),sQuery(id+"F26.wireOp",EDGE,"E169"),sQuery(id+"F26.wireOp",EDGE,"E170"),sQuery(id+"F26.wireOp",EDGE,"E171"),sQuery(id+"F26.wireOp",EDGE,"E172"),sQuery(id+"F26.wireOp",EDGE,"E173"),sQuery(id+"F26.wireOp",EDGE,"E174"),sQuery(id+"F26.wireOp",EDGE,"E175"),sQuery(id+"F26.wireOp",EDGE,"E176"),sQuery(id+"F26.wireOp",EDGE,"E177"),sQuery(id+"F26.wireOp",EDGE,"E178"),sQuery(id+"F26.wireOp",EDGE,"E179"),sQuery(id+"F26.wireOp",EDGE,"E180"),sQuery(id+"F26.wireOp",EDGE,"E181"),sQuery(id+"F26.wireOp",EDGE,"E182"),sQuery(id+"F26.wireOp",EDGE,"E183"),sQuery(id+"F26.wireOp",EDGE,"E184"),sQuery(id+"F26.wireOp",EDGE,"E185"),sQuery(id+"F26.wireOp",EDGE,"E186"),sQuery(id+"F26.wireOp",EDGE,"E187"),sQuery(id+"F26.wireOp",EDGE,"E188.trimOffspring"),sQuery(id+"F26.wireOp",EDGE,"E189.trimOffspring"),sQuery(id+"F26.wireOp",EDGE,"E190"),sQuery(id+"F26.wireOp",EDGE,"E191"),sQuery(id+"F26.wireOp",EDGE,"E192"),sQuery(id+"F26.wireOp",EDGE,"E193"),sQuery(id+"F26.wireOp",EDGE,"E198"),sQuery(id+"F26.wireOp",EDGE,"E199"),sQuery(id+"F26.wireOp",EDGE,"E200"),sQuery(id+"F26.wireOp",EDGE,"E201"),sQuery(id+"F26.wireOp",EDGE,"E225"),sQuery(id+"F26.wireOp",EDGE,"E226"),sQuery(id+"F26.wireOp",EDGE,"E227"),sQuery(id+"F26.wireOp",EDGE,"E228"),sQuery(id+"F26.wireOp",EDGE,"E229"),sQuery(id+"F26.wireOp",EDGE,"E230"),sQuery(id+"F26.wireOp",EDGE,"E231"),sQuery(id+"F26.wireOp",EDGE,"E232"),sQuery(id+"F26.wireOp",EDGE,"E233"),sQuery(id+"F26.wireOp",EDGE,"E234"),sQuery(id+"F26.wireOp",EDGE,"E235"),sQuery(id+"F26.wireOp",EDGE,"E236"),sQuery(id+"F26.wireOp",EDGE,"E237"),sQuery(id+"F26.wireOp",EDGE,"E238"),sQuery(id+"F26.wireOp",EDGE,"E239"),sQuery(id+"F26.wireOp",EDGE,"E240"),sQuery(id+"F26.wireOp",EDGE,"E241"),sQuery(id+"F26.wireOp",EDGE,"E242"),sQuery(id+"F26.wireOp",EDGE,"E243"),sQuery(id+"F26.wireOp",EDGE,"E244"),sQuery(id+"F26.wireOp",EDGE,"E245"),sQuery(id+"F26.wireOp",EDGE,"E246"),sQuery(id+"F26.wireOp",EDGE,"E247"),sQuery(id+"F26.wireOp",EDGE,"E248"),sQuery(id+"F26.wireOp",EDGE,"E249"),sQuery(id+"F26.wireOp",EDGE,"E250"),sQuery(id+"F26.wireOp",EDGE,"E251"),sQuery(id+"F26.wireOp",EDGE,"E252"),sQuery(id+"F26.wireOp",EDGE,"E253"),sQuery(id+"F26.wireOp",EDGE,"E254"),sQuery(id+"F26.wireOp",EDGE,"E255"),sQuery(id+"F26.wireOp",EDGE,"E256"),sQuery(id+"F26.wireOp",EDGE,"E257"),sQuery(id+"F26.wireOp",EDGE,"E258"),sQuery(id+"F26.wireOp",EDGE,"E259"),sQuery(id+"F26.wireOp",EDGE,"E260"),sQuery(id+"F26.wireOp",EDGE,"E261"),sQuery(id+"F26.wireOp",EDGE,"E262"),sQuery(id+"F26.wireOp",EDGE,"E263"),sQuery(id+"F26.wireOp",EDGE,"E264"),sQuery(id+"F26.wireOp",EDGE,"E265"),sQuery(id+"F26.wireOp",EDGE,"E266"),sQuery(id+"F26.wireOp",EDGE,"E267"),sQuery(id+"F26.wireOp",EDGE,"E268"),sQuery(id+"F26.wireOp",EDGE,"E269"),sQuery(id+"F26.wireOp",EDGE,"E270"),sQuery(id+"F26.wireOp",EDGE,"E271"),sQuery(id+"F26.wireOp",EDGE,"E272"),sQuery(id+"F26.wireOp",EDGE,"E273"),sQuery(id+"F26.wireOp",EDGE,"E274"),sQuery(id+"F26.wireOp",EDGE,"E275"),sQuery(id+"F26.wireOp",EDGE,"E276"),sQuery(id+"F26.wireOp",EDGE,"E277"),sQuery(id+"F26.wireOp",EDGE,"E278"),sQuery(id+"F26.wireOp",EDGE,"E279"),sQuery(id+"F26.wireOp",EDGE,"E280"),sQuery(id+"F26.wireOp",EDGE,"E281"),sQuery(id+"F26.wireOp",EDGE,"E282"),sQuery(id+"F26.wireOp",EDGE,"E283"),sQuery(id+"F26.wireOp",EDGE,"E284"),sQuery(id+"F26.wireOp",EDGE,"E285"),sQuery(id+"F26.wireOp",EDGE,"E286"),sQuery(id+"F26.wireOp",EDGE,"E287"),sQuery(id+"F26.wireOp",EDGE,"E288"),sQuery(id+"F26.wireOp",EDGE,"E289.trimOffspring"),sQuery(id+"F26.wireOp",EDGE,"E291"),sQuery(id+"F26.wireOp",EDGE,"E292"),sQuery(id+"F26.wireOp",EDGE,"E293"),sQuery(id+"F26.wireOp",EDGE,"E294"),sQuery(id+"F26.wireOp",EDGE,"E295"),sQuery(id+"F26.wireOp",EDGE,"E296"),sQuery(id+"F26.wireOp",EDGE,"E297"),sQuery(id+"F26.wireOp",EDGE,"E298"),sQuery(id+"F26.wireOp",EDGE,"E299"),sQuery(id+"F26.wireOp",EDGE,"E300"),sQuery(id+"F26.wireOp",EDGE,"E301"),sQuery(id+"F26.wireOp",EDGE,"E302"),sQuery(id+"F26.wireOp",EDGE,"E303"),sQuery(id+"F26.wireOp",EDGE,"E304"),sQuery(id+"F26.wireOp",EDGE,"E305"),sQuery(id+"F26.wireOp",EDGE,"E306"),sQuery(id+"F26.wireOp",EDGE,"E307"),sQuery(id+"F26.wireOp",EDGE,"E308"),sQuery(id+"F26.wireOp",EDGE,"E309"),sQuery(id+"F26.wireOp",EDGE,"E310"),sQuery(id+"F26.wireOp",EDGE,"E311"),sQuery(id+"F26.wireOp",EDGE,"E424"),sQuery(id+"F26.wireOp",EDGE,"E425"),sQuery(id+"F26.wireOp",EDGE,"E426"),sQuery(id+"F26.wireOp",EDGE,"E427"),sQuery(id+"F26.wireOp",EDGE,"E428"),sQuery(id+"F26.wireOp",EDGE,"E429"),sQuery(id+"F26.wireOp",EDGE,"E430"),sQuery(id+"F26.wireOp",EDGE,"E431"),sQuery(id+"F26.wireOp",EDGE,"E432"),sQuery(id+"F26.wireOp",EDGE,"E433"),sQuery(id+"F26.wireOp",EDGE,"E434"),sQuery(id+"F26.wireOp",EDGE,"E435"),sQuery(id+"F26.wireOp",EDGE,"E436"),sQuery(id+"F26.wireOp",EDGE,"E437"),sQuery(id+"F26.wireOp",EDGE,"E438"),sQuery(id+"F26.wireOp",EDGE,"E439"),sQuery(id+"F26.wireOp",EDGE,"E440"),sQuery(id+"F26.wireOp",EDGE,"E441"),sQuery(id+"F26.wireOp",EDGE,"E442"),sQuery(id+"F26.wireOp",EDGE,"E443"),sQuery(id+"F26.wireOp",EDGE,"E444"),sQuery(id+"F26.wireOp",EDGE,"E445"),sQuery(id+"F26.wireOp",EDGE,"E446"),sQuery(id+"F26.wireOp",EDGE,"E447"),sQuery(id+"F26.wireOp",EDGE,"E448"),sQuery(id+"F26.wireOp",EDGE,"E449"),sQuery(id+"F26.wireOp",EDGE,"E450"),sQuery(id+"F26.wireOp",EDGE,"E451"),sQuery(id+"F26.wireOp",EDGE,"E452"),sQuery(id+"F26.wireOp",EDGE,"E453"),sQuery(id+"F26.wireOp",EDGE,"E454"),sQuery(id+"F26.wireOp",EDGE,"E455"),sQuery(id+"F26.wireOp",EDGE,"E456"),sQuery(id+"F26.wireOp",EDGE,"E457"),sQuery(id+"F26.wireOp",EDGE,"E458"),sQuery(id+"F26.wireOp",EDGE,"E459"),sQuery(id+"F26.wireOp",EDGE,"E460"),sQuery(id+"F26.wireOp",EDGE,"E461"),sQuery(id+"F26.wireOp",EDGE,"E462"),sQuery(id+"F26.wireOp",EDGE,"E463"),sQuery(id+"F26.wireOp",EDGE,"E464"),sQuery(id+"F26.wireOp",EDGE,"E465"),sQuery(id+"F26.wireOp",EDGE,"E466"),sQuery(id+"F26.wireOp",EDGE,"E467"),sQuery(id+"F26.wireOp",EDGE,"E468"),sQuery(id+"F26.wireOp",EDGE,"E469"),sQuery(id+"F26.wireOp",EDGE,"E470"),sQuery(id+"F26.wireOp",EDGE,"E471"),sQuery(id+"F26.wireOp",EDGE,"E472"),sQuery(id+"F26.wireOp",EDGE,"E473"),sQuery(id+"F26.wireOp",EDGE,"E474"),sQuery(id+"F26.wireOp",EDGE,"E475"),sQuery(id+"F26.wireOp",EDGE,"E476"),sQuery(id+"F26.wireOp",EDGE,"E477"),sQuery(id+"F26.wireOp",EDGE,"E478"),sQuery(id+"F26.wireOp",EDGE,"E479"),sQuery(id+"F26.wireOp",EDGE,"E480"),sQuery(id+"F26.wireOp",EDGE,"E481"),sQuery(id+"F26.wireOp",EDGE,"E482"),sQuery(id+"F26.wireOp",EDGE,"E483"),sQuery(id+"F26.wireOp",EDGE,"E484"),sQuery(id+"F26.wireOp",EDGE,"E485"),sQuery(id+"F26.wireOp",EDGE,"E486"),sQuery(id+"F26.wireOp",EDGE,"E487"),sQuery(id+"F26.wireOp",EDGE,"E488"),sQuery(id+"F26.wireOp",EDGE,"E489"),sQuery(id+"F26.wireOp",EDGE,"E490"),sQuery(id+"F26.wireOp",EDGE,"E491"),sQuery(id+"F26.wireOp",EDGE,"E492"),sQuery(id+"F26.wireOp",EDGE,"E493"),sQuery(id+"F26.wireOp",EDGE,"E494"),sQuery(id+"F26.wireOp",EDGE,"E495"),sQuery(id+"F26.wireOp",EDGE,"E496"),sQuery(id+"F26.wireOp",EDGE,"E497"),sQuery(id+"F26.wireOp",EDGE,"E498"),sQuery(id+"F26.wireOp",EDGE,"E499"),sQuery(id+"F26.wireOp",EDGE,"E500"),sQuery(id+"F26.wireOp",EDGE,"E501"),sQuery(id+"F26.wireOp",EDGE,"E502"),sQuery(id+"F26.wireOp",EDGE,"E503"),sQuery(id+"F26.wireOp",EDGE,"E504"),sQuery(id+"F26.wireOp",EDGE,"E505")])]});
            var Q1;
            Q1=makeQuery(id+"F32.opPattern","COPY",BODY,{"derivedFrom":makeQuery(id+"F27.opExtrude","SWEPT_BODY",BODY,{"disambiguationData":[OSD([sQuery(id+"F26.wireOp",EDGE,"E92"),sQuery(id+"F26.wireOp",EDGE,"E93"),sQuery(id+"F26.wireOp",EDGE,"E94"),sQuery(id+"F26.wireOp",EDGE,"E95"),sQuery(id+"F26.wireOp",EDGE,"E96"),sQuery(id+"F26.wireOp",EDGE,"E97"),sQuery(id+"F26.wireOp",EDGE,"E98"),sQuery(id+"F26.wireOp",EDGE,"E99"),sQuery(id+"F26.wireOp",EDGE,"E100"),sQuery(id+"F26.wireOp",EDGE,"E101"),sQuery(id+"F26.wireOp",EDGE,"E102"),sQuery(id+"F26.wireOp",EDGE,"E103"),sQuery(id+"F26.wireOp",EDGE,"E104"),sQuery(id+"F26.wireOp",EDGE,"E105"),sQuery(id+"F26.wireOp",EDGE,"E106"),sQuery(id+"F26.wireOp",EDGE,"E107"),sQuery(id+"F26.wireOp",EDGE,"E108.trimOffspring"),sQuery(id+"F26.wireOp",EDGE,"E109.trimOffspring"),sQuery(id+"F26.wireOp",EDGE,"E110.trimOffspring"),sQuery(id+"F26.wireOp",EDGE,"E111.trimOffspring"),sQuery(id+"F26.wireOp",EDGE,"E112.trimOffspring"),sQuery(id+"F26.wireOp",EDGE,"E113.trimOffspring"),sQuery(id+"F26.wireOp",EDGE,"E114.trimOffspring"),sQuery(id+"F26.wireOp",EDGE,"E115.trimOffspring"),sQuery(id+"F26.wireOp",EDGE,"E116.trimOffspring"),sQuery(id+"F26.wireOp",EDGE,"E117"),sQuery(id+"F26.wireOp",EDGE,"E118"),sQuery(id+"F26.wireOp",EDGE,"E119"),sQuery(id+"F26.wireOp",EDGE,"E120"),sQuery(id+"F26.wireOp",EDGE,"E121"),sQuery(id+"F26.wireOp",EDGE,"E122"),sQuery(id+"F26.wireOp",EDGE,"E123"),sQuery(id+"F26.wireOp",EDGE,"E124"),sQuery(id+"F26.wireOp",EDGE,"E125"),sQuery(id+"F26.wireOp",EDGE,"E126"),sQuery(id+"F26.wireOp",EDGE,"E127"),sQuery(id+"F26.wireOp",EDGE,"E128"),sQuery(id+"F26.wireOp",EDGE,"E129"),sQuery(id+"F26.wireOp",EDGE,"E130"),sQuery(id+"F26.wireOp",EDGE,"E131"),sQuery(id+"F26.wireOp",EDGE,"E132"),sQuery(id+"F26.wireOp",EDGE,"E133"),sQuery(id+"F26.wireOp",EDGE,"E134"),sQuery(id+"F26.wireOp",EDGE,"E135"),sQuery(id+"F26.wireOp",EDGE,"E136"),sQuery(id+"F26.wireOp",EDGE,"E137"),sQuery(id+"F26.wireOp",EDGE,"E138"),sQuery(id+"F26.wireOp",EDGE,"E139"),sQuery(id+"F26.wireOp",EDGE,"E140"),sQuery(id+"F26.wireOp",EDGE,"E141"),sQuery(id+"F26.wireOp",EDGE,"E142"),sQuery(id+"F26.wireOp",EDGE,"E143"),sQuery(id+"F26.wireOp",EDGE,"E144"),sQuery(id+"F26.wireOp",EDGE,"E145"),sQuery(id+"F26.wireOp",EDGE,"E146"),sQuery(id+"F26.wireOp",EDGE,"E147"),sQuery(id+"F26.wireOp",EDGE,"E148"),sQuery(id+"F26.wireOp",EDGE,"E149"),sQuery(id+"F26.wireOp",EDGE,"E150"),sQuery(id+"F26.wireOp",EDGE,"E151"),sQuery(id+"F26.wireOp",EDGE,"E152"),sQuery(id+"F26.wireOp",EDGE,"E153"),sQuery(id+"F26.wireOp",EDGE,"E154"),sQuery(id+"F26.wireOp",EDGE,"E155"),sQuery(id+"F26.wireOp",EDGE,"E156"),sQuery(id+"F26.wireOp",EDGE,"E157.trimOffspring"),sQuery(id+"F26.wireOp",EDGE,"E158"),sQuery(id+"F26.wireOp",EDGE,"E159"),sQuery(id+"F26.wireOp",EDGE,"E160"),sQuery(id+"F26.wireOp",EDGE,"E161"),sQuery(id+"F26.wireOp",EDGE,"E162"),sQuery(id+"F26.wireOp",EDGE,"E163"),sQuery(id+"F26.wireOp",EDGE,"E164"),sQuery(id+"F26.wireOp",EDGE,"E165"),sQuery(id+"F26.wireOp",EDGE,"E166"),sQuery(id+"F26.wireOp",EDGE,"E167"),sQuery(id+"F26.wireOp",EDGE,"E168"),sQuery(id+"F26.wireOp",EDGE,"E169"),sQuery(id+"F26.wireOp",EDGE,"E170"),sQuery(id+"F26.wireOp",EDGE,"E171"),sQuery(id+"F26.wireOp",EDGE,"E172"),sQuery(id+"F26.wireOp",EDGE,"E173"),sQuery(id+"F26.wireOp",EDGE,"E174"),sQuery(id+"F26.wireOp",EDGE,"E175"),sQuery(id+"F26.wireOp",EDGE,"E176"),sQuery(id+"F26.wireOp",EDGE,"E177"),sQuery(id+"F26.wireOp",EDGE,"E178"),sQuery(id+"F26.wireOp",EDGE,"E179"),sQuery(id+"F26.wireOp",EDGE,"E180"),sQuery(id+"F26.wireOp",EDGE,"E181"),sQuery(id+"F26.wireOp",EDGE,"E182"),sQuery(id+"F26.wireOp",EDGE,"E183"),sQuery(id+"F26.wireOp",EDGE,"E184"),sQuery(id+"F26.wireOp",EDGE,"E185"),sQuery(id+"F26.wireOp",EDGE,"E186"),sQuery(id+"F26.wireOp",EDGE,"E187"),sQuery(id+"F26.wireOp",EDGE,"E188.trimOffspring"),sQuery(id+"F26.wireOp",EDGE,"E189.trimOffspring"),sQuery(id+"F26.wireOp",EDGE,"E190"),sQuery(id+"F26.wireOp",EDGE,"E191"),sQuery(id+"F26.wireOp",EDGE,"E192"),sQuery(id+"F26.wireOp",EDGE,"E193"),sQuery(id+"F26.wireOp",EDGE,"E198"),sQuery(id+"F26.wireOp",EDGE,"E199"),sQuery(id+"F26.wireOp",EDGE,"E200"),sQuery(id+"F26.wireOp",EDGE,"E201"),sQuery(id+"F26.wireOp",EDGE,"E225"),sQuery(id+"F26.wireOp",EDGE,"E226"),sQuery(id+"F26.wireOp",EDGE,"E227"),sQuery(id+"F26.wireOp",EDGE,"E228"),sQuery(id+"F26.wireOp",EDGE,"E229"),sQuery(id+"F26.wireOp",EDGE,"E230"),sQuery(id+"F26.wireOp",EDGE,"E231"),sQuery(id+"F26.wireOp",EDGE,"E232"),sQuery(id+"F26.wireOp",EDGE,"E233"),sQuery(id+"F26.wireOp",EDGE,"E234"),sQuery(id+"F26.wireOp",EDGE,"E235"),sQuery(id+"F26.wireOp",EDGE,"E236"),sQuery(id+"F26.wireOp",EDGE,"E237"),sQuery(id+"F26.wireOp",EDGE,"E238"),sQuery(id+"F26.wireOp",EDGE,"E239"),sQuery(id+"F26.wireOp",EDGE,"E240"),sQuery(id+"F26.wireOp",EDGE,"E241"),sQuery(id+"F26.wireOp",EDGE,"E242"),sQuery(id+"F26.wireOp",EDGE,"E243"),sQuery(id+"F26.wireOp",EDGE,"E244"),sQuery(id+"F26.wireOp",EDGE,"E245"),sQuery(id+"F26.wireOp",EDGE,"E246"),sQuery(id+"F26.wireOp",EDGE,"E247"),sQuery(id+"F26.wireOp",EDGE,"E248"),sQuery(id+"F26.wireOp",EDGE,"E249"),sQuery(id+"F26.wireOp",EDGE,"E250"),sQuery(id+"F26.wireOp",EDGE,"E251"),sQuery(id+"F26.wireOp",EDGE,"E252"),sQuery(id+"F26.wireOp",EDGE,"E253"),sQuery(id+"F26.wireOp",EDGE,"E254"),sQuery(id+"F26.wireOp",EDGE,"E255"),sQuery(id+"F26.wireOp",EDGE,"E256"),sQuery(id+"F26.wireOp",EDGE,"E257"),sQuery(id+"F26.wireOp",EDGE,"E258"),sQuery(id+"F26.wireOp",EDGE,"E259"),sQuery(id+"F26.wireOp",EDGE,"E260"),sQuery(id+"F26.wireOp",EDGE,"E261"),sQuery(id+"F26.wireOp",EDGE,"E262"),sQuery(id+"F26.wireOp",EDGE,"E263"),sQuery(id+"F26.wireOp",EDGE,"E264"),sQuery(id+"F26.wireOp",EDGE,"E265"),sQuery(id+"F26.wireOp",EDGE,"E266"),sQuery(id+"F26.wireOp",EDGE,"E267"),sQuery(id+"F26.wireOp",EDGE,"E268"),sQuery(id+"F26.wireOp",EDGE,"E269"),sQuery(id+"F26.wireOp",EDGE,"E270"),sQuery(id+"F26.wireOp",EDGE,"E271"),sQuery(id+"F26.wireOp",EDGE,"E272"),sQuery(id+"F26.wireOp",EDGE,"E273"),sQuery(id+"F26.wireOp",EDGE,"E274"),sQuery(id+"F26.wireOp",EDGE,"E275"),sQuery(id+"F26.wireOp",EDGE,"E276"),sQuery(id+"F26.wireOp",EDGE,"E277"),sQuery(id+"F26.wireOp",EDGE,"E278"),sQuery(id+"F26.wireOp",EDGE,"E279"),sQuery(id+"F26.wireOp",EDGE,"E280"),sQuery(id+"F26.wireOp",EDGE,"E281"),sQuery(id+"F26.wireOp",EDGE,"E282"),sQuery(id+"F26.wireOp",EDGE,"E283"),sQuery(id+"F26.wireOp",EDGE,"E284"),sQuery(id+"F26.wireOp",EDGE,"E285"),sQuery(id+"F26.wireOp",EDGE,"E286"),sQuery(id+"F26.wireOp",EDGE,"E287"),sQuery(id+"F26.wireOp",EDGE,"E288"),sQuery(id+"F26.wireOp",EDGE,"E289.trimOffspring"),sQuery(id+"F26.wireOp",EDGE,"E291"),sQuery(id+"F26.wireOp",EDGE,"E292"),sQuery(id+"F26.wireOp",EDGE,"E293"),sQuery(id+"F26.wireOp",EDGE,"E294"),sQuery(id+"F26.wireOp",EDGE,"E295"),sQuery(id+"F26.wireOp",EDGE,"E296"),sQuery(id+"F26.wireOp",EDGE,"E297"),sQuery(id+"F26.wireOp",EDGE,"E298"),sQuery(id+"F26.wireOp",EDGE,"E299"),sQuery(id+"F26.wireOp",EDGE,"E300"),sQuery(id+"F26.wireOp",EDGE,"E301"),sQuery(id+"F26.wireOp",EDGE,"E302"),sQuery(id+"F26.wireOp",EDGE,"E303"),sQuery(id+"F26.wireOp",EDGE,"E304"),sQuery(id+"F26.wireOp",EDGE,"E305"),sQuery(id+"F26.wireOp",EDGE,"E306"),sQuery(id+"F26.wireOp",EDGE,"E307"),sQuery(id+"F26.wireOp",EDGE,"E308"),sQuery(id+"F26.wireOp",EDGE,"E309"),sQuery(id+"F26.wireOp",EDGE,"E310"),sQuery(id+"F26.wireOp",EDGE,"E311"),sQuery(id+"F26.wireOp",EDGE,"E424"),sQuery(id+"F26.wireOp",EDGE,"E425"),sQuery(id+"F26.wireOp",EDGE,"E426"),sQuery(id+"F26.wireOp",EDGE,"E427"),sQuery(id+"F26.wireOp",EDGE,"E428"),sQuery(id+"F26.wireOp",EDGE,"E429"),sQuery(id+"F26.wireOp",EDGE,"E430"),sQuery(id+"F26.wireOp",EDGE,"E431"),sQuery(id+"F26.wireOp",EDGE,"E432"),sQuery(id+"F26.wireOp",EDGE,"E433"),sQuery(id+"F26.wireOp",EDGE,"E434"),sQuery(id+"F26.wireOp",EDGE,"E435"),sQuery(id+"F26.wireOp",EDGE,"E436"),sQuery(id+"F26.wireOp",EDGE,"E437"),sQuery(id+"F26.wireOp",EDGE,"E438"),sQuery(id+"F26.wireOp",EDGE,"E439"),sQuery(id+"F26.wireOp",EDGE,"E440"),sQuery(id+"F26.wireOp",EDGE,"E441"),sQuery(id+"F26.wireOp",EDGE,"E442"),sQuery(id+"F26.wireOp",EDGE,"E443"),sQuery(id+"F26.wireOp",EDGE,"E444"),sQuery(id+"F26.wireOp",EDGE,"E445"),sQuery(id+"F26.wireOp",EDGE,"E446"),sQuery(id+"F26.wireOp",EDGE,"E447"),sQuery(id+"F26.wireOp",EDGE,"E448"),sQuery(id+"F26.wireOp",EDGE,"E449"),sQuery(id+"F26.wireOp",EDGE,"E450"),sQuery(id+"F26.wireOp",EDGE,"E451"),sQuery(id+"F26.wireOp",EDGE,"E452"),sQuery(id+"F26.wireOp",EDGE,"E453"),sQuery(id+"F26.wireOp",EDGE,"E454"),sQuery(id+"F26.wireOp",EDGE,"E455"),sQuery(id+"F26.wireOp",EDGE,"E456"),sQuery(id+"F26.wireOp",EDGE,"E457"),sQuery(id+"F26.wireOp",EDGE,"E458"),sQuery(id+"F26.wireOp",EDGE,"E459"),sQuery(id+"F26.wireOp",EDGE,"E460"),sQuery(id+"F26.wireOp",EDGE,"E461"),sQuery(id+"F26.wireOp",EDGE,"E462"),sQuery(id+"F26.wireOp",EDGE,"E463"),sQuery(id+"F26.wireOp",EDGE,"E464"),sQuery(id+"F26.wireOp",EDGE,"E465"),sQuery(id+"F26.wireOp",EDGE,"E466"),sQuery(id+"F26.wireOp",EDGE,"E467"),sQuery(id+"F26.wireOp",EDGE,"E468"),sQuery(id+"F26.wireOp",EDGE,"E469"),sQuery(id+"F26.wireOp",EDGE,"E470"),sQuery(id+"F26.wireOp",EDGE,"E471"),sQuery(id+"F26.wireOp",EDGE,"E472"),sQuery(id+"F26.wireOp",EDGE,"E473"),sQuery(id+"F26.wireOp",EDGE,"E474"),sQuery(id+"F26.wireOp",EDGE,"E475"),sQuery(id+"F26.wireOp",EDGE,"E476"),sQuery(id+"F26.wireOp",EDGE,"E477"),sQuery(id+"F26.wireOp",EDGE,"E478"),sQuery(id+"F26.wireOp",EDGE,"E479"),sQuery(id+"F26.wireOp",EDGE,"E480"),sQuery(id+"F26.wireOp",EDGE,"E481"),sQuery(id+"F26.wireOp",EDGE,"E482"),sQuery(id+"F26.wireOp",EDGE,"E483"),sQuery(id+"F26.wireOp",EDGE,"E484"),sQuery(id+"F26.wireOp",EDGE,"E485"),sQuery(id+"F26.wireOp",EDGE,"E486"),sQuery(id+"F26.wireOp",EDGE,"E487"),sQuery(id+"F26.wireOp",EDGE,"E488"),sQuery(id+"F26.wireOp",EDGE,"E489"),sQuery(id+"F26.wireOp",EDGE,"E490"),sQuery(id+"F26.wireOp",EDGE,"E491"),sQuery(id+"F26.wireOp",EDGE,"E492"),sQuery(id+"F26.wireOp",EDGE,"E493"),sQuery(id+"F26.wireOp",EDGE,"E494"),sQuery(id+"F26.wireOp",EDGE,"E495"),sQuery(id+"F26.wireOp",EDGE,"E496"),sQuery(id+"F26.wireOp",EDGE,"E497"),sQuery(id+"F26.wireOp",EDGE,"E498"),sQuery(id+"F26.wireOp",EDGE,"E499"),sQuery(id+"F26.wireOp",EDGE,"E500"),sQuery(id+"F26.wireOp",EDGE,"E501"),sQuery(id+"F26.wireOp",EDGE,"E502"),sQuery(id+"F26.wireOp",EDGE,"E503"),sQuery(id+"F26.wireOp",EDGE,"E504"),sQuery(id+"F26.wireOp",EDGE,"E505")])]}),"instanceName":"1"});
            var Q2;
            Q2=sQuery(id+"F0.wireOp",EDGE,"E3");
            circularPattern(context, id + "F34", {"entities" : qUnion([Q0, Q1]), "axis" : qUnion([Q2]), "angle" : 360 * degree, "instanceCount" : 4, "equalSpace" : true});
        }
        {
            var Q0;
            Q0=qCreatedBy(makeId("Front.planeOp"),FACE);
            var sketch = newSketch(context, id + "F35", { "sketchPlane" : qUnion([Q0])});
            skLineSegment(sketch, "E593.bottom", {"start": v(2.72, 49.3) * mm, "end": v(-2.88, 49.3) * mm});
            skLineSegment(sketch, "E593.top", {"start": v(2.72, 33.99) * mm, "end": v(-2.88, 33.99) * mm});
            skLineSegment(sketch, "E593.left", {"start": v(2.72, 49.3) * mm, "end": v(2.72, 33.99) * mm});
            skLineSegment(sketch, "E593.right", {"start": v(-2.88, 49.3) * mm, "end": v(-2.88, 33.99) * mm});
            skSolve(sketch);
        }
        {
            var Q0;
            Q0 = qSketchRegion(id + "F35", true);
            extrude(context, id + "F36", {"entities" : qUnion([Q0]), "endBound" : BoundingType.SYMMETRIC, "depth" : 5 * mm, "offsetDistance" : 25 * mm});
        }
        {
            var Q0;
            Q0=makeQuery(id+"F36.opExtrude","SWEPT_FACE",FACE,{"disambiguationData":[OSD([sQuery(id+"F35.wireOp",EDGE,"E593.bottom")])]});
            var sketch = newSketch(context, id + "F37", { "sketchPlane" : qUnion([Q0])});
            skLineSegment(sketch, "E594.0.0", {"start": v(2.72, 2.5) * mm, "end": v(-2.88, 2.5) * mm});
            skLineSegment(sketch, "E594.0.1", {"start": v(-2.88, 2.5) * mm, "end": v(-2.88, -2.5) * mm});
            skLineSegment(sketch, "E594.0.2", {"start": v(-2.88, -2.5) * mm, "end": v(2.72, -2.5) * mm});
            skLineSegment(sketch, "E594.0.3", {"start": v(2.72, -2.5) * mm, "end": v(2.72, 2.5) * mm});
            skSolve(sketch);
        }
        {
            var Q0;
            Q0 = qSketchRegion(id + "F37", true);
            extrude(context, id + "F38", {"entities" : qUnion([Q0]), "operationType" : NewBodyOperationType.ADD, "depth" : 25 * mm, "offsetDistance" : 25 * mm, "hasDraft" : true, "draftAngle" : 30 * degree, "draftPullDirection" : true});
        }
        {
            var Q0;
            Q0=makeQuery(id+"F36.opExtrude","SWEPT_FACE",FACE,{"disambiguationData":[OSD([sQuery(id+"F35.wireOp",EDGE,"E593.top")])]});
            var sketch = newSketch(context, id + "F39", { "sketchPlane" : qUnion([Q0])});
            skLineSegment(sketch, "E595.0.0", {"start": v(-2.88, -2.5) * mm, "end": v(2.72, -2.5) * mm});
            skLineSegment(sketch, "E595.0.1", {"start": v(2.72, -2.5) * mm, "end": v(2.72, 2.5) * mm});
            skLineSegment(sketch, "E595.0.2", {"start": v(2.72, 2.5) * mm, "end": v(-2.88, 2.5) * mm});
            skLineSegment(sketch, "E595.0.3", {"start": v(-2.88, 2.5) * mm, "end": v(-2.88, -2.5) * mm});
            skSolve(sketch);
        }
        {
            var Q0;
            Q0 = qSketchRegion(id + "F39", true);
            extrude(context, id + "F40", {"entities" : qUnion([Q0]), "operationType" : NewBodyOperationType.ADD, "depth" : 25 * mm, "offsetDistance" : 25 * mm, "hasDraft" : true, "draftAngle" : 30 * degree, "draftPullDirection" : true});
        }
    });
